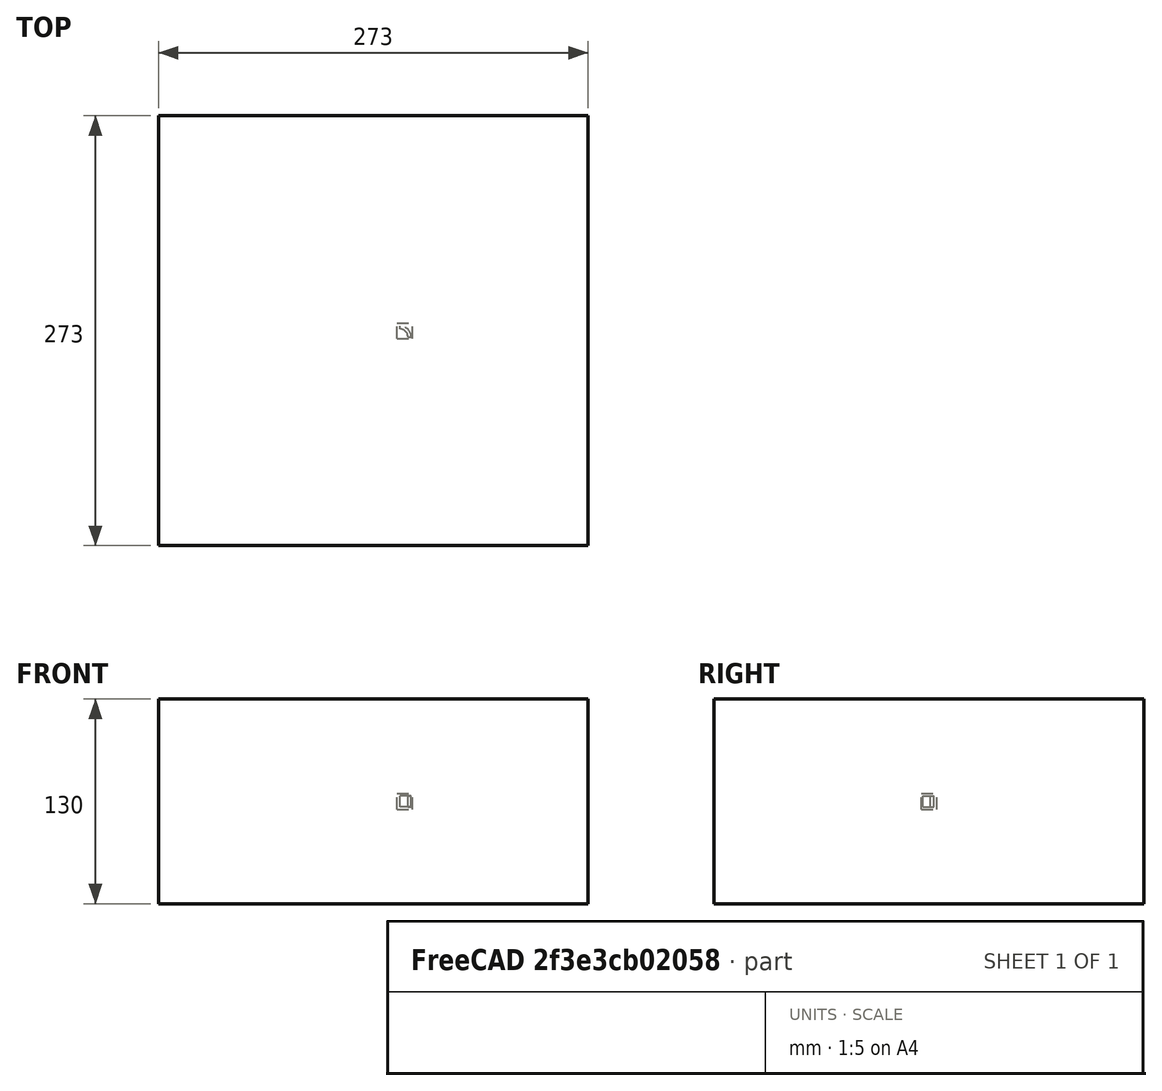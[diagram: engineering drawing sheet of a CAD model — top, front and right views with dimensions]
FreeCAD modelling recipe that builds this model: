
FCSTD DOCUMENT  (FreeCAD 1.0R39109 (Git))
Label: polarArray-of-Part
License: All rights reserved
LicenseURL: http://en.wikipedia.org/wiki/All_rights_reserved
objects: App::DocumentObjectGroupPython×1251, Part::FeaturePython×4, App::Part×4
note: 3 computed .brp shape members not serialized (recipe doc carries the construction recipe); baked Part::Feature solids carry a one-line shape summary decoded from their .brp

FEATURE [App::DocumentObjectGroupPython] HALFPI  # scripted group (container) (typed FeaturePython)
  name = HALFPI
  value = pi/2.
FEATURE [App::DocumentObjectGroupPython] PI  # scripted group (container) (typed FeaturePython)
  name = PI
  value = 1.*pi
FEATURE [App::DocumentObjectGroupPython] TWOPI  # scripted group (container) (typed FeaturePython)
  name = TWOPI
  value = 2.*pi
FEATURE [App::DocumentObjectGroupPython] Constants  # scripted group (container) (typed FeaturePython)
  Group = -> [HALFPI,PI,TWOPI]
FEATURE [App::DocumentObjectGroupPython] Variables  # scripted group (container) (typed FeaturePython)
FEATURE [App::DocumentObjectGroupPython] Quantities  # scripted group (container) (typed FeaturePython)
FEATURE [App::DocumentObjectGroupPython] Isotopes  # scripted group (container) (typed FeaturePython)
FEATURE [App::DocumentObjectGroupPython] Elements  # scripted group (container) (typed FeaturePython)
FEATURE [App::DocumentObjectGroupPython] Matrix  # scripted group (container) (typed FeaturePython)
FEATURE [App::DocumentObjectGroupPython] Surfaces  # scripted group (container) (typed FeaturePython)
FEATURE [App::DocumentObjectGroupPython] Opticals  # scripted group (container) (typed FeaturePython)
  Group = -> [Matrix,Surfaces]
FEATURE [App::DocumentObjectGroupPython] G4Isotopes  # scripted group (container) (typed FeaturePython)
FEATURE [App::DocumentObjectGroupPython] H_element  # scripted group (container) (typed FeaturePython)
  Z = 1
  atom_value = 1.008
  formula = H
  name = H_element
FEATURE [App::DocumentObjectGroupPython] He_element  # scripted group (container) (typed FeaturePython)
  Z = 2
  atom_value = 4.0026
  formula = He
  name = He_element
FEATURE [App::DocumentObjectGroupPython] Li_element  # scripted group (container) (typed FeaturePython)
  Z = 3
  atom_value = 6.94
  formula = Li
  name = Li_element
FEATURE [App::DocumentObjectGroupPython] Be_element  # scripted group (container) (typed FeaturePython)
  Z = 4
  atom_value = 9.01218
  formula = Be
  name = Be_element
FEATURE [App::DocumentObjectGroupPython] B_element  # scripted group (container) (typed FeaturePython)
  Z = 5
  atom_value = 10.81
  formula = B
  name = B_element
FEATURE [App::DocumentObjectGroupPython] C_element  # scripted group (container) (typed FeaturePython)
  Z = 6
  atom_value = 12.011
  formula = C
  name = C_element
FEATURE [App::DocumentObjectGroupPython] N_element  # scripted group (container) (typed FeaturePython)
  Z = 7
  atom_value = 14.007
  formula = N
  name = N_element
FEATURE [App::DocumentObjectGroupPython] O_element  # scripted group (container) (typed FeaturePython)
  Z = 8
  atom_value = 15.999
  formula = O
  name = O_element
FEATURE [App::DocumentObjectGroupPython] F_element  # scripted group (container) (typed FeaturePython)
  Z = 9
  atom_value = 18.9984
  formula = F
  name = F_element
FEATURE [App::DocumentObjectGroupPython] Ne_element  # scripted group (container) (typed FeaturePython)
  Z = 10
  atom_value = 20.1797
  formula = Ne
  name = Ne_element
FEATURE [App::DocumentObjectGroupPython] Na_element  # scripted group (container) (typed FeaturePython)
  Z = 11
  atom_value = 22.9898
  formula = Na
  name = Na_element
FEATURE [App::DocumentObjectGroupPython] Mg_element  # scripted group (container) (typed FeaturePython)
  Z = 12
  atom_value = 24.305
  formula = Mg
  name = Mg_element
FEATURE [App::DocumentObjectGroupPython] Al_element  # scripted group (container) (typed FeaturePython)
  Z = 13
  atom_value = 26.9815
  formula = Al
  name = Al_element
FEATURE [App::DocumentObjectGroupPython] Si_element  # scripted group (container) (typed FeaturePython)
  Z = 14
  atom_value = 28.085
  formula = Si
  name = Si_element
FEATURE [App::DocumentObjectGroupPython] P_element  # scripted group (container) (typed FeaturePython)
  Z = 15
  atom_value = 30.9738
  formula = P
  name = P_element
FEATURE [App::DocumentObjectGroupPython] S_element  # scripted group (container) (typed FeaturePython)
  Z = 16
  atom_value = 32.06
  formula = S
  name = S_element
FEATURE [App::DocumentObjectGroupPython] Cl_element  # scripted group (container) (typed FeaturePython)
  Z = 17
  atom_value = 35.45
  formula = Cl
  name = Cl_element
FEATURE [App::DocumentObjectGroupPython] Ar_element  # scripted group (container) (typed FeaturePython)
  Z = 18
  atom_value = 39.95
  formula = Ar
  name = Ar_element
FEATURE [App::DocumentObjectGroupPython] K_element  # scripted group (container) (typed FeaturePython)
  Z = 19
  atom_value = 39.0983
  formula = K
  name = K_element
FEATURE [App::DocumentObjectGroupPython] Ca_element  # scripted group (container) (typed FeaturePython)
  Z = 20
  atom_value = 40.078
  formula = Ca
  name = Ca_element
FEATURE [App::DocumentObjectGroupPython] Sc_element  # scripted group (container) (typed FeaturePython)
  Z = 21
  atom_value = 44.9559
  formula = Sc
  name = Sc_element
FEATURE [App::DocumentObjectGroupPython] Ti_element  # scripted group (container) (typed FeaturePython)
  Z = 22
  atom_value = 47.867
  formula = Ti
  name = Ti_element
FEATURE [App::DocumentObjectGroupPython] V_element  # scripted group (container) (typed FeaturePython)
  Z = 23
  atom_value = 50.9415
  formula = V
  name = V_element
FEATURE [App::DocumentObjectGroupPython] Cr_element  # scripted group (container) (typed FeaturePython)
  Z = 24
  atom_value = 51.9961
  formula = Cr
  name = Cr_element
FEATURE [App::DocumentObjectGroupPython] Mn_element  # scripted group (container) (typed FeaturePython)
  Z = 25
  atom_value = 54.938
  formula = Mn
  name = Mn_element
FEATURE [App::DocumentObjectGroupPython] Fe_element  # scripted group (container) (typed FeaturePython)
  Z = 26
  atom_value = 55.845
  formula = Fe
  name = Fe_element
FEATURE [App::DocumentObjectGroupPython] Co_element  # scripted group (container) (typed FeaturePython)
  Z = 27
  atom_value = 58.9332
  formula = Co
  name = Co_element
FEATURE [App::DocumentObjectGroupPython] Ni_element  # scripted group (container) (typed FeaturePython)
  Z = 28
  atom_value = 58.6934
  formula = Ni
  name = Ni_element
FEATURE [App::DocumentObjectGroupPython] Cu_element  # scripted group (container) (typed FeaturePython)
  Z = 29
  atom_value = 63.546
  formula = Cu
  name = Cu_element
FEATURE [App::DocumentObjectGroupPython] Zn_element  # scripted group (container) (typed FeaturePython)
  Z = 30
  atom_value = 65.38
  formula = Zn
  name = Zn_element
FEATURE [App::DocumentObjectGroupPython] Ga_element  # scripted group (container) (typed FeaturePython)
  Z = 31
  atom_value = 69.723
  formula = Ga
  name = Ga_element
FEATURE [App::DocumentObjectGroupPython] Ge_element  # scripted group (container) (typed FeaturePython)
  Z = 32
  atom_value = 72.63
  formula = Ge
  name = Ge_element
FEATURE [App::DocumentObjectGroupPython] As_element  # scripted group (container) (typed FeaturePython)
  Z = 33
  atom_value = 74.9216
  formula = As
  name = As_element
FEATURE [App::DocumentObjectGroupPython] Se_element  # scripted group (container) (typed FeaturePython)
  Z = 34
  atom_value = 78.971
  formula = Se
  name = Se_element
FEATURE [App::DocumentObjectGroupPython] Br_element  # scripted group (container) (typed FeaturePython)
  Z = 35
  atom_value = 79.904
  formula = Br
  name = Br_element
FEATURE [App::DocumentObjectGroupPython] Kr_element  # scripted group (container) (typed FeaturePython)
  Z = 36
  atom_value = 83.798
  formula = Kr
  name = Kr_element
FEATURE [App::DocumentObjectGroupPython] Rb_element  # scripted group (container) (typed FeaturePython)
  Z = 37
  atom_value = 85.4678
  formula = Rb
  name = Rb_element
FEATURE [App::DocumentObjectGroupPython] Sr_element  # scripted group (container) (typed FeaturePython)
  Z = 38
  atom_value = 87.62
  formula = Sr
  name = Sr_element
FEATURE [App::DocumentObjectGroupPython] Y_element  # scripted group (container) (typed FeaturePython)
  Z = 39
  atom_value = 88.9058
  formula = Y
  name = Y_element
FEATURE [App::DocumentObjectGroupPython] Zr_element  # scripted group (container) (typed FeaturePython)
  Z = 40
  atom_value = 91.224
  formula = Zr
  name = Zr_element
FEATURE [App::DocumentObjectGroupPython] Nb_element  # scripted group (container) (typed FeaturePython)
  Z = 41
  atom_value = 92.9064
  formula = Nb
  name = Nb_element
FEATURE [App::DocumentObjectGroupPython] Mo_element  # scripted group (container) (typed FeaturePython)
  Z = 42
  atom_value = 95.95
  formula = Mo
  name = Mo_element
FEATURE [App::DocumentObjectGroupPython] Tc_element  # scripted group (container) (typed FeaturePython)
  Z = 43
  atom_value = 97
  formula = Tc
  name = Tc_element
FEATURE [App::DocumentObjectGroupPython] Ru_element  # scripted group (container) (typed FeaturePython)
  Z = 44
  atom_value = 101.07
  formula = Ru
  name = Ru_element
FEATURE [App::DocumentObjectGroupPython] Rh_element  # scripted group (container) (typed FeaturePython)
  Z = 45
  atom_value = 102.905
  formula = Rh
  name = Rh_element
FEATURE [App::DocumentObjectGroupPython] Pd_element  # scripted group (container) (typed FeaturePython)
  Z = 46
  atom_value = 106.42
  formula = Pd
  name = Pd_element
FEATURE [App::DocumentObjectGroupPython] Ag_element  # scripted group (container) (typed FeaturePython)
  Z = 47
  atom_value = 107.868
  formula = Ag
  name = Ag_element
FEATURE [App::DocumentObjectGroupPython] Cd_element  # scripted group (container) (typed FeaturePython)
  Z = 48
  atom_value = 112.414
  formula = Cd
  name = Cd_element
FEATURE [App::DocumentObjectGroupPython] In_element  # scripted group (container) (typed FeaturePython)
  Z = 49
  atom_value = 114.818
  formula = In
  name = In_element
FEATURE [App::DocumentObjectGroupPython] Sn_element  # scripted group (container) (typed FeaturePython)
  Z = 50
  atom_value = 118.71
  formula = Sn
  name = Sn_element
FEATURE [App::DocumentObjectGroupPython] Sb_element  # scripted group (container) (typed FeaturePython)
  Z = 51
  atom_value = 121.76
  formula = Sb
  name = Sb_element
FEATURE [App::DocumentObjectGroupPython] Te_element  # scripted group (container) (typed FeaturePython)
  Z = 52
  atom_value = 127.6
  formula = Te
  name = Te_element
FEATURE [App::DocumentObjectGroupPython] I_element  # scripted group (container) (typed FeaturePython)
  Z = 53
  atom_value = 126.904
  formula = I
  name = I_element
FEATURE [App::DocumentObjectGroupPython] Xe_element  # scripted group (container) (typed FeaturePython)
  Z = 54
  atom_value = 131.293
  formula = Xe
  name = Xe_element
FEATURE [App::DocumentObjectGroupPython] Cs_element  # scripted group (container) (typed FeaturePython)
  Z = 55
  atom_value = 132.905
  formula = Cs
  name = Cs_element
FEATURE [App::DocumentObjectGroupPython] Ba_element  # scripted group (container) (typed FeaturePython)
  Z = 56
  atom_value = 137.327
  formula = Ba
  name = Ba_element
FEATURE [App::DocumentObjectGroupPython] La_element  # scripted group (container) (typed FeaturePython)
  Z = 57
  atom_value = 138.905
  formula = La
  name = La_element
FEATURE [App::DocumentObjectGroupPython] Ce_element  # scripted group (container) (typed FeaturePython)
  Z = 58
  atom_value = 140.116
  formula = Ce
  name = Ce_element
FEATURE [App::DocumentObjectGroupPython] Pr_element  # scripted group (container) (typed FeaturePython)
  Z = 59
  atom_value = 140.908
  formula = Pr
  name = Pr_element
FEATURE [App::DocumentObjectGroupPython] Nd_element  # scripted group (container) (typed FeaturePython)
  Z = 60
  atom_value = 144.242
  formula = Nd
  name = Nd_element
FEATURE [App::DocumentObjectGroupPython] Pm_element  # scripted group (container) (typed FeaturePython)
  Z = 61
  atom_value = 145
  formula = Pm
  name = Pm_element
FEATURE [App::DocumentObjectGroupPython] Sm_element  # scripted group (container) (typed FeaturePython)
  Z = 62
  atom_value = 150.36
  formula = Sm
  name = Sm_element
FEATURE [App::DocumentObjectGroupPython] Eu_element  # scripted group (container) (typed FeaturePython)
  Z = 63
  atom_value = 151.964
  formula = Eu
  name = Eu_element
FEATURE [App::DocumentObjectGroupPython] Gd_element  # scripted group (container) (typed FeaturePython)
  Z = 64
  atom_value = 157.25
  formula = Gd
  name = Gd_element
FEATURE [App::DocumentObjectGroupPython] Tb_element  # scripted group (container) (typed FeaturePython)
  Z = 65
  atom_value = 158.925
  formula = Tb
  name = Tb_element
FEATURE [App::DocumentObjectGroupPython] Dy_element  # scripted group (container) (typed FeaturePython)
  Z = 66
  atom_value = 162.5
  formula = Dy
  name = Dy_element
FEATURE [App::DocumentObjectGroupPython] Ho_element  # scripted group (container) (typed FeaturePython)
  Z = 67
  atom_value = 164.93
  formula = Ho
  name = Ho_element
FEATURE [App::DocumentObjectGroupPython] Er_element  # scripted group (container) (typed FeaturePython)
  Z = 68
  atom_value = 167.259
  formula = Er
  name = Er_element
FEATURE [App::DocumentObjectGroupPython] Tm_element  # scripted group (container) (typed FeaturePython)
  Z = 69
  atom_value = 168.934
  formula = Tm
  name = Tm_element
FEATURE [App::DocumentObjectGroupPython] Yb_element  # scripted group (container) (typed FeaturePython)
  Z = 70
  atom_value = 173.045
  formula = Yb
  name = Yb_element
FEATURE [App::DocumentObjectGroupPython] Lu_element  # scripted group (container) (typed FeaturePython)
  Z = 71
  atom_value = 174.967
  formula = Lu
  name = Lu_element
FEATURE [App::DocumentObjectGroupPython] Hf_element  # scripted group (container) (typed FeaturePython)
  Z = 72
  atom_value = 178.49
  formula = Hf
  name = Hf_element
FEATURE [App::DocumentObjectGroupPython] Ta_element  # scripted group (container) (typed FeaturePython)
  Z = 73
  atom_value = 180.948
  formula = Ta
  name = Ta_element
FEATURE [App::DocumentObjectGroupPython] W_element  # scripted group (container) (typed FeaturePython)
  Z = 74
  atom_value = 183.84
  formula = W
  name = W_element
FEATURE [App::DocumentObjectGroupPython] Re_element  # scripted group (container) (typed FeaturePython)
  Z = 75
  atom_value = 186.207
  formula = Re
  name = Re_element
FEATURE [App::DocumentObjectGroupPython] Os_element  # scripted group (container) (typed FeaturePython)
  Z = 76
  atom_value = 190.23
  formula = Os
  name = Os_element
FEATURE [App::DocumentObjectGroupPython] Ir_element  # scripted group (container) (typed FeaturePython)
  Z = 77
  atom_value = 192.217
  formula = Ir
  name = Ir_element
FEATURE [App::DocumentObjectGroupPython] Pt_element  # scripted group (container) (typed FeaturePython)
  Z = 78
  atom_value = 195.084
  formula = Pt
  name = Pt_element
FEATURE [App::DocumentObjectGroupPython] Au_element  # scripted group (container) (typed FeaturePython)
  Z = 79
  atom_value = 196.967
  formula = Au
  name = Au_element
FEATURE [App::DocumentObjectGroupPython] Hg_element  # scripted group (container) (typed FeaturePython)
  Z = 80
  atom_value = 200.592
  formula = Hg
  name = Hg_element
FEATURE [App::DocumentObjectGroupPython] Tl_element  # scripted group (container) (typed FeaturePython)
  Z = 81
  atom_value = 204.38
  formula = Tl
  name = Tl_element
FEATURE [App::DocumentObjectGroupPython] Pb_element  # scripted group (container) (typed FeaturePython)
  Z = 82
  atom_value = 207.2
  formula = Pb
  name = Pb_element
FEATURE [App::DocumentObjectGroupPython] Bi_element  # scripted group (container) (typed FeaturePython)
  Z = 83
  atom_value = 208.98
  formula = Bi
  name = Bi_element
FEATURE [App::DocumentObjectGroupPython] Po_element  # scripted group (container) (typed FeaturePython)
  Z = 84
  atom_value = 209
  formula = Po
  name = Po_element
FEATURE [App::DocumentObjectGroupPython] At_element  # scripted group (container) (typed FeaturePython)
  Z = 85
  atom_value = 210
  formula = At
  name = At_element
FEATURE [App::DocumentObjectGroupPython] Rn_element  # scripted group (container) (typed FeaturePython)
  Z = 86
  atom_value = 222
  formula = Rn
  name = Rn_element
FEATURE [App::DocumentObjectGroupPython] Fr_element  # scripted group (container) (typed FeaturePython)
  Z = 87
  atom_value = 223
  formula = Fr
  name = Fr_element
FEATURE [App::DocumentObjectGroupPython] Ra_element  # scripted group (container) (typed FeaturePython)
  Z = 88
  atom_value = 226
  formula = Ra
  name = Ra_element
FEATURE [App::DocumentObjectGroupPython] Ac_element  # scripted group (container) (typed FeaturePython)
  Z = 89
  atom_value = 227
  formula = Ac
  name = Ac_element
FEATURE [App::DocumentObjectGroupPython] Th_element  # scripted group (container) (typed FeaturePython)
  Z = 90
  atom_value = 232.038
  formula = Th
  name = Th_element
FEATURE [App::DocumentObjectGroupPython] Pa_element  # scripted group (container) (typed FeaturePython)
  Z = 91
  atom_value = 231.036
  formula = Pa
  name = Pa_element
FEATURE [App::DocumentObjectGroupPython] U_element  # scripted group (container) (typed FeaturePython)
  Z = 92
  atom_value = 238.029
  formula = U
  name = U_element
FEATURE [App::DocumentObjectGroupPython] Np_element  # scripted group (container) (typed FeaturePython)
  Z = 93
  atom_value = 237
  formula = Np
  name = Np_element
FEATURE [App::DocumentObjectGroupPython] Pu_element  # scripted group (container) (typed FeaturePython)
  Z = 94
  atom_value = 244
  formula = Pu
  name = Pu_element
FEATURE [App::DocumentObjectGroupPython] Am_element  # scripted group (container) (typed FeaturePython)
  Z = 95
  atom_value = 243
  formula = Am
  name = Am_element
FEATURE [App::DocumentObjectGroupPython] Cm_element  # scripted group (container) (typed FeaturePython)
  Z = 96
  atom_value = 247
  formula = Cm
  name = Cm_element
FEATURE [App::DocumentObjectGroupPython] Bk_element  # scripted group (container) (typed FeaturePython)
  Z = 97
  atom_value = 247
  formula = Bk
  name = Bk_element
FEATURE [App::DocumentObjectGroupPython] Cf_element  # scripted group (container) (typed FeaturePython)
  Z = 98
  atom_value = 251
  formula = Cf
  name = Cf_element
FEATURE [App::DocumentObjectGroupPython] G4Elements  # scripted group (container) (typed FeaturePython)
  Group = -> [H_element,He_element,Li_element,Be_element,B_element,C_element,N_element,O_element,F_element,Ne_element,Na_element,Mg_element,Al_element,Si_element,P_element,S_element,Cl_element,Ar_element,K_element,Ca_element,Sc_element,Ti_element,V_element,Cr_element,Mn_element,Fe_element,Co_element,Ni_element,Cu_element,Zn_element,Ga_element,Ge_element,As_element,Se_element,Br_element,Kr_element,Rb_element,+61 more]
FEATURE [App::DocumentObjectGroupPython] H_element001  label="H_element : 0.101"  # scripted group (container) (typed FeaturePython)
  n = 0.101327
FEATURE [App::DocumentObjectGroupPython] C_element001  label="C_element : 0.775"  # scripted group (container) (typed FeaturePython)
  n = 0.7755
FEATURE [App::DocumentObjectGroupPython] N_element001  label="N_element : 0.035"  # scripted group (container) (typed FeaturePython)
  n = 0.035057
FEATURE [App::DocumentObjectGroupPython] O_element001  label="O_element : 0.052"  # scripted group (container) (typed FeaturePython)
  n = 0.0523159
FEATURE [App::DocumentObjectGroupPython] F_element001  label="F_element : 0.017"  # scripted group (container) (typed FeaturePython)
  n = 0.017422
FEATURE [App::DocumentObjectGroupPython] Ca_element001  label="Ca_element : 0.018"  # scripted group (container) (typed FeaturePython)
  n = 0.018378
FEATURE [App::DocumentObjectGroupPython] G4_A_150_TISSUE  label="G4_A-150_TISSUE"  # scripted group (container) (typed FeaturePython)
  Dunit = g/cm3
  Dvalue = 1.127
  Group = -> [H_element001,C_element001,N_element001,O_element001,F_element001,Ca_element001]
  conduct = 2
  density = 1
  expand = 3
  formula = G4_A-150_TISSUE
  name = G4_A-150_TISSUE
  specific = 4
FEATURE [App::DocumentObjectGroupPython] C_element002  label="C_element : 3"  # scripted group (container) (typed FeaturePython)
  n = 3
  ref = C_element
FEATURE [App::DocumentObjectGroupPython] H_element002  label="H_element : 6"  # scripted group (container) (typed FeaturePython)
  n = 6
  ref = H_element
FEATURE [App::DocumentObjectGroupPython] O_element002  label="O_element : 1"  # scripted group (container) (typed FeaturePython)
  n = 1
  ref = O_element
FEATURE [App::DocumentObjectGroupPython] G4_ACETONE  # scripted group (container) (typed FeaturePython)
  Dunit = g/cm3
  Dvalue = 0.7899
  Group = -> [C_element002,H_element002,O_element002]
  conduct = 2
  density = 1
  expand = 3
  formula = G4_ACETONE
  name = G4_ACETONE
  specific = 4
FEATURE [App::DocumentObjectGroupPython] C_element003  label="C_element : 2"  # scripted group (container) (typed FeaturePython)
  n = 2
  ref = C_element
FEATURE [App::DocumentObjectGroupPython] H_element003  label="H_element : 2"  # scripted group (container) (typed FeaturePython)
  n = 2
  ref = H_element
FEATURE [App::DocumentObjectGroupPython] G4_ACETYLENE  # scripted group (container) (typed FeaturePython)
  Dunit = g/cm3
  Dvalue = 0.0010967
  Group = -> [C_element003,H_element003]
  conduct = 2
  density = 1
  expand = 3
  formula = G4_ACETYLENE
  name = G4_ACETYLENE
  specific = 4
FEATURE [App::DocumentObjectGroupPython] C_element004  label="C_element : 5"  # scripted group (container) (typed FeaturePython)
  n = 5
  ref = C_element
FEATURE [App::DocumentObjectGroupPython] H_element004  label="H_element : 5"  # scripted group (container) (typed FeaturePython)
  n = 5
  ref = H_element
FEATURE [App::DocumentObjectGroupPython] N_element002  label="N_element : 5"  # scripted group (container) (typed FeaturePython)
  n = 5
  ref = N_element
FEATURE [App::DocumentObjectGroupPython] G4_ADENINE  # scripted group (container) (typed FeaturePython)
  Dunit = g/cm3
  Dvalue = 1.6
  Group = -> [C_element004,H_element004,N_element002]
  conduct = 2
  density = 1
  expand = 3
  formula = G4_ADENINE
  name = G4_ADENINE
  specific = 4
FEATURE [App::DocumentObjectGroupPython] H_element005  label="H_element : 0.114"  # scripted group (container) (typed FeaturePython)
  n = 0.114
FEATURE [App::DocumentObjectGroupPython] C_element005  label="C_element : 0.598"  # scripted group (container) (typed FeaturePython)
  n = 0.598
FEATURE [App::DocumentObjectGroupPython] N_element003  label="N_element : 0.007"  # scripted group (container) (typed FeaturePython)
  n = 0.007
FEATURE [App::DocumentObjectGroupPython] O_element003  label="O_element : 0.278"  # scripted group (container) (typed FeaturePython)
  n = 0.278
FEATURE [App::DocumentObjectGroupPython] Na_element001  label="Na_element : 0.001"  # scripted group (container) (typed FeaturePython)
  n = 0.001
FEATURE [App::DocumentObjectGroupPython] S_element001  label="S_element : 0.001"  # scripted group (container) (typed FeaturePython)
  n = 0.001
FEATURE [App::DocumentObjectGroupPython] Cl_element001  label="Cl_element : 0.001"  # scripted group (container) (typed FeaturePython)
  n = 0.001
FEATURE [App::DocumentObjectGroupPython] G4_ADIPOSE_TISSUE_ICRP  # scripted group (container) (typed FeaturePython)
  Dunit = g/cm3
  Dvalue = 0.95
  Group = -> [H_element005,C_element005,N_element003,O_element003,Na_element001,S_element001,Cl_element001]
  conduct = 2
  density = 1
  expand = 3
  formula = G4_ADIPOSE_TISSUE_ICRP
  name = G4_ADIPOSE_TISSUE_ICRP
  specific = 4
FEATURE [App::DocumentObjectGroupPython] C_element006  label="C_element : 0.000"  # scripted group (container) (typed FeaturePython)
  n = 0.000124
FEATURE [App::DocumentObjectGroupPython] N_element004  label="N_element : 0.755"  # scripted group (container) (typed FeaturePython)
  n = 0.755268
FEATURE [App::DocumentObjectGroupPython] O_element004  label="O_element : 0.232"  # scripted group (container) (typed FeaturePython)
  n = 0.231781
FEATURE [App::DocumentObjectGroupPython] Ar_element001  label="Ar_element : 0.013"  # scripted group (container) (typed FeaturePython)
  n = 0.012827
FEATURE [App::DocumentObjectGroupPython] G4_AIR  # scripted group (container) (typed FeaturePython)
  Dunit = g/cm3
  Dvalue = 0.00120479
  Group = -> [C_element006,N_element004,O_element004,Ar_element001]
  conduct = 2
  density = 1
  expand = 3
  formula = G4_AIR
  name = G4_AIR
  specific = 4
FEATURE [App::DocumentObjectGroupPython] C_element007  label="C_element : 006"  # scripted group (container) (typed FeaturePython)
  n = 3
  ref = C_element
FEATURE [App::DocumentObjectGroupPython] H_element006  label="H_element : 7"  # scripted group (container) (typed FeaturePython)
  n = 7
  ref = H_element
FEATURE [App::DocumentObjectGroupPython] N_element005  label="N_element : 1"  # scripted group (container) (typed FeaturePython)
  n = 1
  ref = N_element
FEATURE [App::DocumentObjectGroupPython] O_element005  label="O_element : 2"  # scripted group (container) (typed FeaturePython)
  n = 2
  ref = O_element
FEATURE [App::DocumentObjectGroupPython] G4_ALANINE  # scripted group (container) (typed FeaturePython)
  Dunit = g/cm3
  Dvalue = 1.42
  Group = -> [C_element007,H_element006,N_element005,O_element005]
  conduct = 2
  density = 1
  expand = 3
  formula = G4_ALANINE
  name = G4_ALANINE
  specific = 4
FEATURE [App::DocumentObjectGroupPython] Al_element001  label="Al_element : 2"  # scripted group (container) (typed FeaturePython)
  n = 2
  ref = Al_element
FEATURE [App::DocumentObjectGroupPython] O_element006  label="O_element : 3"  # scripted group (container) (typed FeaturePython)
  n = 3
  ref = O_element
FEATURE [App::DocumentObjectGroupPython] G4_ALUMINUM_OXIDE  # scripted group (container) (typed FeaturePython)
  Dunit = g/cm3
  Dvalue = 3.97
  Group = -> [Al_element001,O_element006]
  conduct = 2
  density = 1
  expand = 3
  formula = G4_ALUMINUM_OXIDE
  name = G4_ALUMINUM_OXIDE
  specific = 4
FEATURE [App::DocumentObjectGroupPython] H_element007  label="H_element : 0.106"  # scripted group (container) (typed FeaturePython)
  n = 0.10593
FEATURE [App::DocumentObjectGroupPython] C_element008  label="C_element : 0.789"  # scripted group (container) (typed FeaturePython)
  n = 0.788974
FEATURE [App::DocumentObjectGroupPython] O_element007  label="O_element : 0.105"  # scripted group (container) (typed FeaturePython)
  n = 0.105096
FEATURE [App::DocumentObjectGroupPython] G4_AMBER  # scripted group (container) (typed FeaturePython)
  Dunit = g/cm3
  Dvalue = 1.1
  Group = -> [H_element007,C_element008,O_element007]
  conduct = 2
  density = 1
  expand = 3
  formula = G4_AMBER
  name = G4_AMBER
  specific = 4
FEATURE [App::DocumentObjectGroupPython] N_element006  label="N_element : 006"  # scripted group (container) (typed FeaturePython)
  n = 1
  ref = N_element
FEATURE [App::DocumentObjectGroupPython] H_element008  label="H_element : 3"  # scripted group (container) (typed FeaturePython)
  n = 3
  ref = H_element
FEATURE [App::DocumentObjectGroupPython] G4_AMMONIA  # scripted group (container) (typed FeaturePython)
  Dunit = g/cm3
  Dvalue = 0.000826019
  Group = -> [N_element006,H_element008]
  conduct = 2
  density = 1
  expand = 3
  formula = G4_AMMONIA
  name = G4_AMMONIA
  specific = 4
FEATURE [App::DocumentObjectGroupPython] C_element009  label="C_element : 6"  # scripted group (container) (typed FeaturePython)
  n = 6
  ref = C_element
FEATURE [App::DocumentObjectGroupPython] H_element009  label="H_element : 008"  # scripted group (container) (typed FeaturePython)
  n = 7
  ref = H_element
FEATURE [App::DocumentObjectGroupPython] N_element007  label="N_element : 007"  # scripted group (container) (typed FeaturePython)
  n = 1
  ref = N_element
FEATURE [App::DocumentObjectGroupPython] G4_ANILINE  # scripted group (container) (typed FeaturePython)
  Dunit = g/cm3
  Dvalue = 1.0235
  Group = -> [C_element009,H_element009,N_element007]
  conduct = 2
  density = 1
  expand = 3
  formula = G4_ANILINE
  name = G4_ANILINE
  specific = 4
FEATURE [App::DocumentObjectGroupPython] C_element010  label="C_element : 14"  # scripted group (container) (typed FeaturePython)
  n = 14
  ref = C_element
FEATURE [App::DocumentObjectGroupPython] H_element010  label="H_element : 10"  # scripted group (container) (typed FeaturePython)
  n = 10
  ref = H_element
FEATURE [App::DocumentObjectGroupPython] G4_ANTHRACENE  # scripted group (container) (typed FeaturePython)
  Dunit = g/cm3
  Dvalue = 1.283
  Group = -> [C_element010,H_element010]
  conduct = 2
  density = 1
  expand = 3
  formula = G4_ANTHRACENE
  name = G4_ANTHRACENE
  specific = 4
FEATURE [App::DocumentObjectGroupPython] H_element011  label="H_element : 0.065"  # scripted group (container) (typed FeaturePython)
  n = 0.0654709
FEATURE [App::DocumentObjectGroupPython] C_element011  label="C_element : 0.537"  # scripted group (container) (typed FeaturePython)
  n = 0.536944
FEATURE [App::DocumentObjectGroupPython] N_element008  label="N_element : 0.021"  # scripted group (container) (typed FeaturePython)
  n = 0.0215
FEATURE [App::DocumentObjectGroupPython] O_element008  label="O_element : 0.032"  # scripted group (container) (typed FeaturePython)
  n = 0.032085
FEATURE [App::DocumentObjectGroupPython] F_element002  label="F_element : 0.167"  # scripted group (container) (typed FeaturePython)
  n = 0.167411
FEATURE [App::DocumentObjectGroupPython] Ca_element002  label="Ca_element : 0.177"  # scripted group (container) (typed FeaturePython)
  n = 0.176589
FEATURE [App::DocumentObjectGroupPython] G4_B_100_BONE  label="G4_B-100_BONE"  # scripted group (container) (typed FeaturePython)
  Dunit = g/cm3
  Dvalue = 1.45
  Group = -> [H_element011,C_element011,N_element008,O_element008,F_element002,Ca_element002]
  conduct = 2
  density = 1
  expand = 3
  formula = G4_B-100_BONE
  name = G4_B-100_BONE
  specific = 4
FEATURE [App::DocumentObjectGroupPython] H_element012  label="H_element : 0.057"  # scripted group (container) (typed FeaturePython)
  n = 0.057441
FEATURE [App::DocumentObjectGroupPython] C_element012  label="C_element : 0.790"  # scripted group (container) (typed FeaturePython)
  n = 0.774591
FEATURE [App::DocumentObjectGroupPython] O_element009  label="O_element : 0.168"  # scripted group (container) (typed FeaturePython)
  n = 0.167968
FEATURE [App::DocumentObjectGroupPython] G4_BAKELITE  # scripted group (container) (typed FeaturePython)
  Dunit = g/cm3
  Dvalue = 1.25
  Group = -> [H_element012,C_element012,O_element009]
  conduct = 2
  density = 1
  expand = 3
  formula = G4_BAKELITE
  name = G4_BAKELITE
  specific = 4
FEATURE [App::DocumentObjectGroupPython] Ba_element001  label="Ba_element : 1"  # scripted group (container) (typed FeaturePython)
  n = 1
  ref = Ba_element
FEATURE [App::DocumentObjectGroupPython] F_element003  label="F_element : 2"  # scripted group (container) (typed FeaturePython)
  n = 2
  ref = F_element
FEATURE [App::DocumentObjectGroupPython] G4_BARIUM_FLUORIDE  # scripted group (container) (typed FeaturePython)
  Dunit = g/cm3
  Dvalue = 4.89
  Group = -> [Ba_element001,F_element003]
  conduct = 2
  density = 1
  expand = 3
  formula = G4_BARIUM_FLUORIDE
  name = G4_BARIUM_FLUORIDE
  specific = 4
FEATURE [App::DocumentObjectGroupPython] Ba_element002  label="Ba_element : 002"  # scripted group (container) (typed FeaturePython)
  n = 1
  ref = Ba_element
FEATURE [App::DocumentObjectGroupPython] S_element002  label="S_element : 1"  # scripted group (container) (typed FeaturePython)
  n = 1
  ref = S_element
FEATURE [App::DocumentObjectGroupPython] O_element010  label="O_element : 4"  # scripted group (container) (typed FeaturePython)
  n = 4
  ref = O_element
FEATURE [App::DocumentObjectGroupPython] G4_BARIUM_SULFATE  # scripted group (container) (typed FeaturePython)
  Dunit = g/cm3
  Dvalue = 4.5
  Group = -> [Ba_element002,S_element002,O_element010]
  conduct = 2
  density = 1
  expand = 3
  formula = G4_BARIUM_SULFATE
  name = G4_BARIUM_SULFATE
  specific = 4
FEATURE [App::DocumentObjectGroupPython] C_element013  label="C_element : 007"  # scripted group (container) (typed FeaturePython)
  n = 6
  ref = C_element
FEATURE [App::DocumentObjectGroupPython] H_element013  label="H_element : 009"  # scripted group (container) (typed FeaturePython)
  n = 6
  ref = H_element
FEATURE [App::DocumentObjectGroupPython] G4_BENZENE  # scripted group (container) (typed FeaturePython)
  Dunit = g/cm3
  Dvalue = 0.87865
  Group = -> [C_element013,H_element013]
  conduct = 2
  density = 1
  expand = 3
  formula = G4_BENZENE
  name = G4_BENZENE
  specific = 4
FEATURE [App::DocumentObjectGroupPython] Be_element001  label="Be_element : 1"  # scripted group (container) (typed FeaturePython)
  n = 1
  ref = Be_element
FEATURE [App::DocumentObjectGroupPython] O_element011  label="O_element : 005"  # scripted group (container) (typed FeaturePython)
  n = 1
  ref = O_element
FEATURE [App::DocumentObjectGroupPython] G4_BERYLLIUM_OXIDE  # scripted group (container) (typed FeaturePython)
  Dunit = g/cm3
  Dvalue = 3.01
  Group = -> [Be_element001,O_element011]
  conduct = 2
  density = 1
  expand = 3
  formula = G4_BERYLLIUM_OXIDE
  name = G4_BERYLLIUM_OXIDE
  specific = 4
FEATURE [App::DocumentObjectGroupPython] Bi_element001  label="Bi_element : 4"  # scripted group (container) (typed FeaturePython)
  n = 4
  ref = Bi_element
FEATURE [App::DocumentObjectGroupPython] Ge_element001  label="Ge_element : 3"  # scripted group (container) (typed FeaturePython)
  n = 3
  ref = Ge_element
FEATURE [App::DocumentObjectGroupPython] O_element012  label="O_element : 12"  # scripted group (container) (typed FeaturePython)
  n = 12
  ref = O_element
FEATURE [App::DocumentObjectGroupPython] G4_BGO  # scripted group (container) (typed FeaturePython)
  Dunit = g/cm3
  Dvalue = 7.13
  Group = -> [Bi_element001,Ge_element001,O_element012]
  conduct = 2
  density = 1
  expand = 3
  formula = G4_BGO
  name = G4_BGO
  specific = 4
FEATURE [App::DocumentObjectGroupPython] H_element014  label="H_element : 0.102"  # scripted group (container) (typed FeaturePython)
  n = 0.102
FEATURE [App::DocumentObjectGroupPython] C_element014  label="C_element : 0.110"  # scripted group (container) (typed FeaturePython)
  n = 0.11
FEATURE [App::DocumentObjectGroupPython] N_element009  label="N_element : 0.033"  # scripted group (container) (typed FeaturePython)
  n = 0.033
FEATURE [App::DocumentObjectGroupPython] O_element013  label="O_element : 0.745"  # scripted group (container) (typed FeaturePython)
  n = 0.745
FEATURE [App::DocumentObjectGroupPython] Na_element002  label="Na_element : 0.002"  # scripted group (container) (typed FeaturePython)
  n = 0.001
FEATURE [App::DocumentObjectGroupPython] P_element001  label="P_element : 0.001"  # scripted group (container) (typed FeaturePython)
  n = 0.001
FEATURE [App::DocumentObjectGroupPython] S_element003  label="S_element : 0.002"  # scripted group (container) (typed FeaturePython)
  n = 0.002
FEATURE [App::DocumentObjectGroupPython] Cl_element002  label="Cl_element : 0.003"  # scripted group (container) (typed FeaturePython)
  n = 0.003
FEATURE [App::DocumentObjectGroupPython] K_element001  label="K_element : 0.002"  # scripted group (container) (typed FeaturePython)
  n = 0.002
FEATURE [App::DocumentObjectGroupPython] Fe_element001  label="Fe_element : 0.001"  # scripted group (container) (typed FeaturePython)
  n = 0.001
FEATURE [App::DocumentObjectGroupPython] G4_BLOOD_ICRP  # scripted group (container) (typed FeaturePython)
  Dunit = g/cm3
  Dvalue = 1.06
  Group = -> [H_element014,C_element014,N_element009,O_element013,Na_element002,P_element001,S_element003,Cl_element002,K_element001,Fe_element001]
  conduct = 2
  density = 1
  expand = 3
  formula = G4_BLOOD_ICRP
  name = G4_BLOOD_ICRP
  specific = 4
FEATURE [App::DocumentObjectGroupPython] H_element015  label="H_element : 0.064"  # scripted group (container) (typed FeaturePython)
  n = 0.064
FEATURE [App::DocumentObjectGroupPython] C_element015  label="C_element : 0.278"  # scripted group (container) (typed FeaturePython)
  n = 0.278
FEATURE [App::DocumentObjectGroupPython] N_element010  label="N_element : 0.027"  # scripted group (container) (typed FeaturePython)
  n = 0.027
FEATURE [App::DocumentObjectGroupPython] O_element014  label="O_element : 0.410"  # scripted group (container) (typed FeaturePython)
  n = 0.41
FEATURE [App::DocumentObjectGroupPython] Mg_element001  label="Mg_element : 0.002"  # scripted group (container) (typed FeaturePython)
  n = 0.002
FEATURE [App::DocumentObjectGroupPython] P_element002  label="P_element : 0.070"  # scripted group (container) (typed FeaturePython)
  n = 0.07
FEATURE [App::DocumentObjectGroupPython] S_element004  label="S_element : 0.003"  # scripted group (container) (typed FeaturePython)
  n = 0.002
FEATURE [App::DocumentObjectGroupPython] Ca_element003  label="Ca_element : 0.147"  # scripted group (container) (typed FeaturePython)
  n = 0.147
FEATURE [App::DocumentObjectGroupPython] G4_BONE_COMPACT_ICRU  # scripted group (container) (typed FeaturePython)
  Dunit = g/cm3
  Dvalue = 1.85
  Group = -> [H_element015,C_element015,N_element010,O_element014,Mg_element001,P_element002,S_element004,Ca_element003]
  conduct = 2
  density = 1
  expand = 3
  formula = G4_BONE_COMPACT_ICRU
  name = G4_BONE_COMPACT_ICRU
  specific = 4
FEATURE [App::DocumentObjectGroupPython] H_element016  label="H_element : 0.034"  # scripted group (container) (typed FeaturePython)
  n = 0.034
FEATURE [App::DocumentObjectGroupPython] C_element016  label="C_element : 0.155"  # scripted group (container) (typed FeaturePython)
  n = 0.155
FEATURE [App::DocumentObjectGroupPython] N_element011  label="N_element : 0.042"  # scripted group (container) (typed FeaturePython)
  n = 0.042
FEATURE [App::DocumentObjectGroupPython] O_element015  label="O_element : 0.435"  # scripted group (container) (typed FeaturePython)
  n = 0.435
FEATURE [App::DocumentObjectGroupPython] Na_element003  label="Na_element : 0.003"  # scripted group (container) (typed FeaturePython)
  n = 0.001
FEATURE [App::DocumentObjectGroupPython] Mg_element002  label="Mg_element : 0.003"  # scripted group (container) (typed FeaturePython)
  n = 0.002
FEATURE [App::DocumentObjectGroupPython] P_element003  label="P_element : 0.103"  # scripted group (container) (typed FeaturePython)
  n = 0.103
FEATURE [App::DocumentObjectGroupPython] S_element005  label="S_element : 0.004"  # scripted group (container) (typed FeaturePython)
  n = 0.003
FEATURE [App::DocumentObjectGroupPython] Ca_element004  label="Ca_element : 0.225"  # scripted group (container) (typed FeaturePython)
  n = 0.225
FEATURE [App::DocumentObjectGroupPython] G4_BONE_CORTICAL_ICRP  # scripted group (container) (typed FeaturePython)
  Dunit = g/cm3
  Dvalue = 1.92
  Group = -> [H_element016,C_element016,N_element011,O_element015,Na_element003,Mg_element002,P_element003,S_element005,Ca_element004]
  conduct = 2
  density = 1
  expand = 3
  formula = G4_BONE_CORTICAL_ICRP
  name = G4_BONE_CORTICAL_ICRP
  specific = 4
FEATURE [App::DocumentObjectGroupPython] B_element001  label="B_element : 4"  # scripted group (container) (typed FeaturePython)
  n = 4
  ref = B_element
FEATURE [App::DocumentObjectGroupPython] C_element017  label="C_element : 1"  # scripted group (container) (typed FeaturePython)
  n = 1
  ref = C_element
FEATURE [App::DocumentObjectGroupPython] G4_BORON_CARBIDE  # scripted group (container) (typed FeaturePython)
  Dunit = g/cm3
  Dvalue = 2.52
  Group = -> [B_element001,C_element017]
  conduct = 2
  density = 1
  expand = 3
  formula = G4_BORON_CARBIDE
  name = G4_BORON_CARBIDE
  specific = 4
FEATURE [App::DocumentObjectGroupPython] B_element002  label="B_element : 2"  # scripted group (container) (typed FeaturePython)
  n = 2
  ref = B_element
FEATURE [App::DocumentObjectGroupPython] O_element016  label="O_element : 006"  # scripted group (container) (typed FeaturePython)
  n = 3
  ref = O_element
FEATURE [App::DocumentObjectGroupPython] G4_BORON_OXIDE  # scripted group (container) (typed FeaturePython)
  Dunit = g/cm3
  Dvalue = 1.812
  Group = -> [B_element002,O_element016]
  conduct = 2
  density = 1
  expand = 3
  formula = G4_BORON_OXIDE
  name = G4_BORON_OXIDE
  specific = 4
FEATURE [App::DocumentObjectGroupPython] H_element017  label="H_element : 0.107"  # scripted group (container) (typed FeaturePython)
  n = 0.107
FEATURE [App::DocumentObjectGroupPython] C_element018  label="C_element : 0.145"  # scripted group (container) (typed FeaturePython)
  n = 0.145
FEATURE [App::DocumentObjectGroupPython] N_element012  label="N_element : 0.022"  # scripted group (container) (typed FeaturePython)
  n = 0.022
FEATURE [App::DocumentObjectGroupPython] O_element017  label="O_element : 0.712"  # scripted group (container) (typed FeaturePython)
  n = 0.712
FEATURE [App::DocumentObjectGroupPython] Na_element004  label="Na_element : 0.004"  # scripted group (container) (typed FeaturePython)
  n = 0.002
FEATURE [App::DocumentObjectGroupPython] P_element004  label="P_element : 0.004"  # scripted group (container) (typed FeaturePython)
  n = 0.004
FEATURE [App::DocumentObjectGroupPython] S_element006  label="S_element : 0.005"  # scripted group (container) (typed FeaturePython)
  n = 0.002
FEATURE [App::DocumentObjectGroupPython] Cl_element003  label="Cl_element : 0.004"  # scripted group (container) (typed FeaturePython)
  n = 0.003
FEATURE [App::DocumentObjectGroupPython] K_element002  label="K_element : 0.003"  # scripted group (container) (typed FeaturePython)
  n = 0.003
FEATURE [App::DocumentObjectGroupPython] G4_BRAIN_ICRP  # scripted group (container) (typed FeaturePython)
  Dunit = g/cm3
  Dvalue = 1.04
  Group = -> [H_element017,C_element018,N_element012,O_element017,Na_element004,P_element004,S_element006,Cl_element003,K_element002]
  conduct = 2
  density = 1
  expand = 3
  formula = G4_BRAIN_ICRP
  name = G4_BRAIN_ICRP
  specific = 4
FEATURE [App::DocumentObjectGroupPython] C_element019  label="C_element : 4"  # scripted group (container) (typed FeaturePython)
  n = 4
  ref = C_element
FEATURE [App::DocumentObjectGroupPython] H_element018  label="H_element : 010"  # scripted group (container) (typed FeaturePython)
  n = 10
  ref = H_element
FEATURE [App::DocumentObjectGroupPython] G4_BUTANE  # scripted group (container) (typed FeaturePython)
  Dunit = g/cm3
  Dvalue = 0.00249343
  Group = -> [C_element019,H_element018]
  conduct = 2
  density = 1
  expand = 3
  formula = G4_BUTANE
  name = G4_BUTANE
  specific = 4
FEATURE [App::DocumentObjectGroupPython] C_element020  label="C_element : 008"  # scripted group (container) (typed FeaturePython)
  n = 4
  ref = C_element
FEATURE [App::DocumentObjectGroupPython] H_element019  label="H_element : 011"  # scripted group (container) (typed FeaturePython)
  n = 10
  ref = H_element
FEATURE [App::DocumentObjectGroupPython] O_element018  label="O_element : 007"  # scripted group (container) (typed FeaturePython)
  n = 1
  ref = O_element
FEATURE [App::DocumentObjectGroupPython] G4_N_BUTYL_ALCOHOL  label="G4_N-BUTYL_ALCOHOL"  # scripted group (container) (typed FeaturePython)
  Dunit = g/cm3
  Dvalue = 0.8098
  Group = -> [C_element020,H_element019,O_element018]
  conduct = 2
  density = 1
  expand = 3
  formula = G4_N-BUTYL_ALCOHOL
  name = G4_N-BUTYL_ALCOHOL
  specific = 4
FEATURE [App::DocumentObjectGroupPython] H_element020  label="H_element : 0.025"  # scripted group (container) (typed FeaturePython)
  n = 0.02468
FEATURE [App::DocumentObjectGroupPython] C_element021  label="C_element : 0.502"  # scripted group (container) (typed FeaturePython)
  n = 0.501611
FEATURE [App::DocumentObjectGroupPython] O_element019  label="O_element : 0.005"  # scripted group (container) (typed FeaturePython)
  n = 0.004527
FEATURE [App::DocumentObjectGroupPython] F_element004  label="F_element : 0.465"  # scripted group (container) (typed FeaturePython)
  n = 0.465209
FEATURE [App::DocumentObjectGroupPython] Si_element001  label="Si_element : 0.004"  # scripted group (container) (typed FeaturePython)
  n = 0.003973
FEATURE [App::DocumentObjectGroupPython] G4_C_552  label="G4_C-552"  # scripted group (container) (typed FeaturePython)
  Dunit = g/cm3
  Dvalue = 1.76
  Group = -> [H_element020,C_element021,O_element019,F_element004,Si_element001]
  conduct = 2
  density = 1
  expand = 3
  formula = G4_C-552
  name = G4_C-552
  specific = 4
FEATURE [App::DocumentObjectGroupPython] Cd_element001  label="Cd_element : 1"  # scripted group (container) (typed FeaturePython)
  n = 1
  ref = Cd_element
FEATURE [App::DocumentObjectGroupPython] Te_element001  label="Te_element : 1"  # scripted group (container) (typed FeaturePython)
  n = 1
  ref = Te_element
FEATURE [App::DocumentObjectGroupPython] G4_CADMIUM_TELLURIDE  # scripted group (container) (typed FeaturePython)
  Dunit = g/cm3
  Dvalue = 6.2
  Group = -> [Cd_element001,Te_element001]
  conduct = 2
  density = 1
  expand = 3
  formula = G4_CADMIUM_TELLURIDE
  name = G4_CADMIUM_TELLURIDE
  specific = 4
FEATURE [App::DocumentObjectGroupPython] Cd_element002  label="Cd_element : 002"  # scripted group (container) (typed FeaturePython)
  n = 1
  ref = Cd_element
FEATURE [App::DocumentObjectGroupPython] W_element001  label="W_element : 1"  # scripted group (container) (typed FeaturePython)
  n = 1
  ref = W_element
FEATURE [App::DocumentObjectGroupPython] O_element020  label="O_element : 008"  # scripted group (container) (typed FeaturePython)
  n = 4
  ref = O_element
FEATURE [App::DocumentObjectGroupPython] G4_CADMIUM_TUNGSTATE  # scripted group (container) (typed FeaturePython)
  Dunit = g/cm3
  Dvalue = 7.9
  Group = -> [Cd_element002,W_element001,O_element020]
  conduct = 2
  density = 1
  expand = 3
  formula = G4_CADMIUM_TUNGSTATE
  name = G4_CADMIUM_TUNGSTATE
  specific = 4
FEATURE [App::DocumentObjectGroupPython] Ca_element005  label="Ca_element : 1"  # scripted group (container) (typed FeaturePython)
  n = 1
  ref = Ca_element
FEATURE [App::DocumentObjectGroupPython] C_element022  label="C_element : 009"  # scripted group (container) (typed FeaturePython)
  n = 1
  ref = C_element
FEATURE [App::DocumentObjectGroupPython] O_element021  label="O_element : 009"  # scripted group (container) (typed FeaturePython)
  n = 3
  ref = O_element
FEATURE [App::DocumentObjectGroupPython] G4_CALCIUM_CARBONATE  # scripted group (container) (typed FeaturePython)
  Dunit = g/cm3
  Dvalue = 2.8
  Group = -> [Ca_element005,C_element022,O_element021]
  conduct = 2
  density = 1
  expand = 3
  formula = G4_CALCIUM_CARBONATE
  name = G4_CALCIUM_CARBONATE
  specific = 4
FEATURE [App::DocumentObjectGroupPython] Ca_element006  label="Ca_element : 002"  # scripted group (container) (typed FeaturePython)
  n = 1
  ref = Ca_element
FEATURE [App::DocumentObjectGroupPython] F_element005  label="F_element : 003"  # scripted group (container) (typed FeaturePython)
  n = 2
  ref = F_element
FEATURE [App::DocumentObjectGroupPython] G4_CALCIUM_FLUORIDE  # scripted group (container) (typed FeaturePython)
  Dunit = g/cm3
  Dvalue = 3.18
  Group = -> [Ca_element006,F_element005]
  conduct = 2
  density = 1
  expand = 3
  formula = G4_CALCIUM_FLUORIDE
  name = G4_CALCIUM_FLUORIDE
  specific = 4
FEATURE [App::DocumentObjectGroupPython] Ca_element007  label="Ca_element : 003"  # scripted group (container) (typed FeaturePython)
  n = 1
  ref = Ca_element
FEATURE [App::DocumentObjectGroupPython] O_element022  label="O_element : 010"  # scripted group (container) (typed FeaturePython)
  n = 1
  ref = O_element
FEATURE [App::DocumentObjectGroupPython] G4_CALCIUM_OXIDE  # scripted group (container) (typed FeaturePython)
  Dunit = g/cm3
  Dvalue = 3.3
  Group = -> [Ca_element007,O_element022]
  conduct = 2
  density = 1
  expand = 3
  formula = G4_CALCIUM_OXIDE
  name = G4_CALCIUM_OXIDE
  specific = 4
FEATURE [App::DocumentObjectGroupPython] Ca_element008  label="Ca_element : 004"  # scripted group (container) (typed FeaturePython)
  n = 1
  ref = Ca_element
FEATURE [App::DocumentObjectGroupPython] S_element007  label="S_element : 002"  # scripted group (container) (typed FeaturePython)
  n = 1
  ref = S_element
FEATURE [App::DocumentObjectGroupPython] O_element023  label="O_element : 011"  # scripted group (container) (typed FeaturePython)
  n = 4
  ref = O_element
FEATURE [App::DocumentObjectGroupPython] G4_CALCIUM_SULFATE  # scripted group (container) (typed FeaturePython)
  Dunit = g/cm3
  Dvalue = 2.96
  Group = -> [Ca_element008,S_element007,O_element023]
  conduct = 2
  density = 1
  expand = 3
  formula = G4_CALCIUM_SULFATE
  name = G4_CALCIUM_SULFATE
  specific = 4
FEATURE [App::DocumentObjectGroupPython] Ca_element009  label="Ca_element : 005"  # scripted group (container) (typed FeaturePython)
  n = 1
  ref = Ca_element
FEATURE [App::DocumentObjectGroupPython] W_element002  label="W_element : 002"  # scripted group (container) (typed FeaturePython)
  n = 1
  ref = W_element
FEATURE [App::DocumentObjectGroupPython] O_element024  label="O_element : 012"  # scripted group (container) (typed FeaturePython)
  n = 4
  ref = O_element
FEATURE [App::DocumentObjectGroupPython] G4_CALCIUM_TUNGSTATE  # scripted group (container) (typed FeaturePython)
  Dunit = g/cm3
  Dvalue = 6.062
  Group = -> [Ca_element009,W_element002,O_element024]
  conduct = 2
  density = 1
  expand = 3
  formula = G4_CALCIUM_TUNGSTATE
  name = G4_CALCIUM_TUNGSTATE
  specific = 4
FEATURE [App::DocumentObjectGroupPython] C_element023  label="C_element : 010"  # scripted group (container) (typed FeaturePython)
  n = 1
  ref = C_element
FEATURE [App::DocumentObjectGroupPython] O_element025  label="O_element : 013"  # scripted group (container) (typed FeaturePython)
  n = 2
  ref = O_element
FEATURE [App::DocumentObjectGroupPython] G4_CARBON_DIOXIDE  # scripted group (container) (typed FeaturePython)
  Dunit = g/cm3
  Dvalue = 0.00184212
  Group = -> [C_element023,O_element025]
  conduct = 2
  density = 1
  expand = 3
  formula = G4_CARBON_DIOXIDE
  name = G4_CARBON_DIOXIDE
  specific = 4
FEATURE [App::DocumentObjectGroupPython] C_element024  label="C_element : 011"  # scripted group (container) (typed FeaturePython)
  n = 1
  ref = C_element
FEATURE [App::DocumentObjectGroupPython] Cl_element004  label="Cl_element : 4"  # scripted group (container) (typed FeaturePython)
  n = 4
  ref = Cl_element
FEATURE [App::DocumentObjectGroupPython] G4_CARBON_TETRACHLORIDE  # scripted group (container) (typed FeaturePython)
  Dunit = g/cm3
  Dvalue = 1.594
  Group = -> [C_element024,Cl_element004]
  conduct = 2
  density = 1
  expand = 3
  formula = G4_CARBON_TETRACHLORIDE
  name = G4_CARBON_TETRACHLORIDE
  specific = 4
FEATURE [App::DocumentObjectGroupPython] C_element025  label="C_element : 012"  # scripted group (container) (typed FeaturePython)
  n = 6
  ref = C_element
FEATURE [App::DocumentObjectGroupPython] H_element021  label="H_element : 012"  # scripted group (container) (typed FeaturePython)
  n = 10
  ref = H_element
FEATURE [App::DocumentObjectGroupPython] O_element026  label="O_element : 5"  # scripted group (container) (typed FeaturePython)
  n = 5
  ref = O_element
FEATURE [App::DocumentObjectGroupPython] G4_CELLULOSE_CELLOPHANE  # scripted group (container) (typed FeaturePython)
  Dunit = g/cm3
  Dvalue = 1.42
  Group = -> [C_element025,H_element021,O_element026]
  conduct = 2
  density = 1
  expand = 3
  formula = G4_CELLULOSE_CELLOPHANE
  name = G4_CELLULOSE_CELLOPHANE
  specific = 4
FEATURE [App::DocumentObjectGroupPython] H_element022  label="H_element : 0.067"  # scripted group (container) (typed FeaturePython)
  n = 0.067125
FEATURE [App::DocumentObjectGroupPython] C_element026  label="C_element : 0.545"  # scripted group (container) (typed FeaturePython)
  n = 0.545403
FEATURE [App::DocumentObjectGroupPython] O_element027  label="O_element : 0.387"  # scripted group (container) (typed FeaturePython)
  n = 0.387472
FEATURE [App::DocumentObjectGroupPython] G4_CELLULOSE_BUTYRATE  # scripted group (container) (typed FeaturePython)
  Dunit = g/cm3
  Dvalue = 1.2
  Group = -> [H_element022,C_element026,O_element027]
  conduct = 2
  density = 1
  expand = 3
  formula = G4_CELLULOSE_BUTYRATE
  name = G4_CELLULOSE_BUTYRATE
  specific = 4
FEATURE [App::DocumentObjectGroupPython] H_element023  label="H_element : 0.029"  # scripted group (container) (typed FeaturePython)
  n = 0.029216
FEATURE [App::DocumentObjectGroupPython] C_element027  label="C_element : 0.271"  # scripted group (container) (typed FeaturePython)
  n = 0.271296
FEATURE [App::DocumentObjectGroupPython] N_element013  label="N_element : 0.121"  # scripted group (container) (typed FeaturePython)
  n = 0.121276
FEATURE [App::DocumentObjectGroupPython] O_element028  label="O_element : 0.578"  # scripted group (container) (typed FeaturePython)
  n = 0.578212
FEATURE [App::DocumentObjectGroupPython] G4_CELLULOSE_NITRATE  # scripted group (container) (typed FeaturePython)
  Dunit = g/cm3
  Dvalue = 1.49
  Group = -> [H_element023,C_element027,N_element013,O_element028]
  conduct = 2
  density = 1
  expand = 3
  formula = G4_CELLULOSE_NITRATE
  name = G4_CELLULOSE_NITRATE
  specific = 4
FEATURE [App::DocumentObjectGroupPython] H_element024  label="H_element : 0.108"  # scripted group (container) (typed FeaturePython)
  n = 0.107596
FEATURE [App::DocumentObjectGroupPython] N_element014  label="N_element : 0.001"  # scripted group (container) (typed FeaturePython)
  n = 0.0008
FEATURE [App::DocumentObjectGroupPython] O_element029  label="O_element : 0.875"  # scripted group (container) (typed FeaturePython)
  n = 0.874976
FEATURE [App::DocumentObjectGroupPython] S_element008  label="S_element : 0.015"  # scripted group (container) (typed FeaturePython)
  n = 0.014627
FEATURE [App::DocumentObjectGroupPython] Ce_element001  label="Ce_element : 0.002"  # scripted group (container) (typed FeaturePython)
  n = 0.002001
FEATURE [App::DocumentObjectGroupPython] G4_CERIC_SULFATE  # scripted group (container) (typed FeaturePython)
  Dunit = g/cm3
  Dvalue = 1.03
  Group = -> [H_element024,N_element014,O_element029,S_element008,Ce_element001]
  conduct = 2
  density = 1
  expand = 3
  formula = G4_CERIC_SULFATE
  name = G4_CERIC_SULFATE
  specific = 4
FEATURE [App::DocumentObjectGroupPython] Cs_element001  label="Cs_element : 1"  # scripted group (container) (typed FeaturePython)
  n = 1
  ref = Cs_element
FEATURE [App::DocumentObjectGroupPython] F_element006  label="F_element : 1"  # scripted group (container) (typed FeaturePython)
  n = 1
  ref = F_element
FEATURE [App::DocumentObjectGroupPython] G4_CESIUM_FLUORIDE  # scripted group (container) (typed FeaturePython)
  Dunit = g/cm3
  Dvalue = 4.115
  Group = -> [Cs_element001,F_element006]
  conduct = 2
  density = 1
  expand = 3
  formula = G4_CESIUM_FLUORIDE
  name = G4_CESIUM_FLUORIDE
  specific = 4
FEATURE [App::DocumentObjectGroupPython] Cs_element002  label="Cs_element : 002"  # scripted group (container) (typed FeaturePython)
  n = 1
  ref = Cs_element
FEATURE [App::DocumentObjectGroupPython] I_element001  label="I_element : 1"  # scripted group (container) (typed FeaturePython)
  n = 1
  ref = I_element
FEATURE [App::DocumentObjectGroupPython] G4_CESIUM_IODIDE  # scripted group (container) (typed FeaturePython)
  Dunit = g/cm3
  Dvalue = 4.51
  Group = -> [Cs_element002,I_element001]
  conduct = 2
  density = 1
  expand = 3
  formula = G4_CESIUM_IODIDE
  name = G4_CESIUM_IODIDE
  specific = 4
FEATURE [App::DocumentObjectGroupPython] C_element028  label="C_element : 013"  # scripted group (container) (typed FeaturePython)
  n = 6
  ref = C_element
FEATURE [App::DocumentObjectGroupPython] H_element025  label="H_element : 013"  # scripted group (container) (typed FeaturePython)
  n = 5
  ref = H_element
FEATURE [App::DocumentObjectGroupPython] Cl_element005  label="Cl_element : 1"  # scripted group (container) (typed FeaturePython)
  n = 1
  ref = Cl_element
FEATURE [App::DocumentObjectGroupPython] G4_CHLOROBENZENE  # scripted group (container) (typed FeaturePython)
  Dunit = g/cm3
  Dvalue = 1.1058
  Group = -> [C_element028,H_element025,Cl_element005]
  conduct = 2
  density = 1
  expand = 3
  formula = G4_CHLOROBENZENE
  name = G4_CHLOROBENZENE
  specific = 4
FEATURE [App::DocumentObjectGroupPython] C_element029  label="C_element : 014"  # scripted group (container) (typed FeaturePython)
  n = 1
  ref = C_element
FEATURE [App::DocumentObjectGroupPython] H_element026  label="H_element : 1"  # scripted group (container) (typed FeaturePython)
  n = 1
  ref = H_element
FEATURE [App::DocumentObjectGroupPython] Cl_element006  label="Cl_element : 3"  # scripted group (container) (typed FeaturePython)
  n = 3
  ref = Cl_element
FEATURE [App::DocumentObjectGroupPython] G4_CHLOROFORM  # scripted group (container) (typed FeaturePython)
  Dunit = g/cm3
  Dvalue = 1.4832
  Group = -> [C_element029,H_element026,Cl_element006]
  conduct = 2
  density = 1
  expand = 3
  formula = G4_CHLOROFORM
  name = G4_CHLOROFORM
  specific = 4
FEATURE [App::DocumentObjectGroupPython] H_element027  label="H_element : 0.010"  # scripted group (container) (typed FeaturePython)
  n = 0.01
FEATURE [App::DocumentObjectGroupPython] C_element030  label="C_element : 0.001"  # scripted group (container) (typed FeaturePython)
  n = 0.001
FEATURE [App::DocumentObjectGroupPython] O_element030  label="O_element : 0.529"  # scripted group (container) (typed FeaturePython)
  n = 0.529107
FEATURE [App::DocumentObjectGroupPython] Na_element005  label="Na_element : 0.016"  # scripted group (container) (typed FeaturePython)
  n = 0.016
FEATURE [App::DocumentObjectGroupPython] Mg_element003  label="Mg_element : 0.004"  # scripted group (container) (typed FeaturePython)
  n = 0.002
FEATURE [App::DocumentObjectGroupPython] Al_element002  label="Al_element : 0.034"  # scripted group (container) (typed FeaturePython)
  n = 0.033872
FEATURE [App::DocumentObjectGroupPython] Si_element002  label="Si_element : 0.337"  # scripted group (container) (typed FeaturePython)
  n = 0.337021
FEATURE [App::DocumentObjectGroupPython] K_element003  label="K_element : 0.013"  # scripted group (container) (typed FeaturePython)
  n = 0.013
FEATURE [App::DocumentObjectGroupPython] Ca_element010  label="Ca_element : 0.044"  # scripted group (container) (typed FeaturePython)
  n = 0.044
FEATURE [App::DocumentObjectGroupPython] Fe_element002  label="Fe_element : 0.014"  # scripted group (container) (typed FeaturePython)
  n = 0.014
FEATURE [App::DocumentObjectGroupPython] G4_CONCRETE  # scripted group (container) (typed FeaturePython)
  Dunit = g/cm3
  Dvalue = 2.3
  Group = -> [H_element027,C_element030,O_element030,Na_element005,Mg_element003,Al_element002,Si_element002,K_element003,Ca_element010,Fe_element002]
  conduct = 2
  density = 1
  expand = 3
  formula = G4_CONCRETE
  name = G4_CONCRETE
  specific = 4
FEATURE [App::DocumentObjectGroupPython] C_element031  label="C_element : 015"  # scripted group (container) (typed FeaturePython)
  n = 6
  ref = C_element
FEATURE [App::DocumentObjectGroupPython] H_element028  label="H_element : 12"  # scripted group (container) (typed FeaturePython)
  n = 12
  ref = H_element
FEATURE [App::DocumentObjectGroupPython] G4_CYCLOHEXANE  # scripted group (container) (typed FeaturePython)
  Dunit = g/cm3
  Dvalue = 0.779
  Group = -> [C_element031,H_element028]
  conduct = 2
  density = 1
  expand = 3
  formula = G4_CYCLOHEXANE
  name = G4_CYCLOHEXANE
  specific = 4
FEATURE [App::DocumentObjectGroupPython] C_element032  label="C_element : 016"  # scripted group (container) (typed FeaturePython)
  n = 6
  ref = C_element
FEATURE [App::DocumentObjectGroupPython] H_element029  label="H_element : 4"  # scripted group (container) (typed FeaturePython)
  n = 4
  ref = H_element
FEATURE [App::DocumentObjectGroupPython] Cl_element007  label="Cl_element : 2"  # scripted group (container) (typed FeaturePython)
  n = 2
  ref = Cl_element
FEATURE [App::DocumentObjectGroupPython] G4_1_2_DICHLOROBENZENE  label="G4_1.2-DICHLOROBENZENE"  # scripted group (container) (typed FeaturePython)
  Dunit = g/cm3
  Dvalue = 1.3048
  Group = -> [C_element032,H_element029,Cl_element007]
  conduct = 2
  density = 1
  expand = 3
  formula = G4_1.2-DICHLOROBENZENE
  name = G4_1.2-DICHLOROBENZENE
  specific = 4
FEATURE [App::DocumentObjectGroupPython] C_element033  label="C_element : 017"  # scripted group (container) (typed FeaturePython)
  n = 4
  ref = C_element
FEATURE [App::DocumentObjectGroupPython] H_element030  label="H_element : 8"  # scripted group (container) (typed FeaturePython)
  n = 8
  ref = H_element
FEATURE [App::DocumentObjectGroupPython] O_element031  label="O_element : 014"  # scripted group (container) (typed FeaturePython)
  n = 1
  ref = O_element
FEATURE [App::DocumentObjectGroupPython] Cl_element008  label="Cl_element : 005"  # scripted group (container) (typed FeaturePython)
  n = 2
  ref = Cl_element
FEATURE [App::DocumentObjectGroupPython] G4_DICHLORODIETHYL_ETHER  # scripted group (container) (typed FeaturePython)
  Dunit = g/cm3
  Dvalue = 1.2199
  Group = -> [C_element033,H_element030,O_element031,Cl_element008]
  conduct = 2
  density = 1
  expand = 3
  formula = G4_DICHLORODIETHYL_ETHER
  name = G4_DICHLORODIETHYL_ETHER
  specific = 4
FEATURE [App::DocumentObjectGroupPython] C_element034  label="C_element : 018"  # scripted group (container) (typed FeaturePython)
  n = 2
  ref = C_element
FEATURE [App::DocumentObjectGroupPython] H_element031  label="H_element : 014"  # scripted group (container) (typed FeaturePython)
  n = 4
  ref = H_element
FEATURE [App::DocumentObjectGroupPython] Cl_element009  label="Cl_element : 006"  # scripted group (container) (typed FeaturePython)
  n = 2
  ref = Cl_element
FEATURE [App::DocumentObjectGroupPython] G4_1_2_DICHLOROETHANE  label="G4_1.2-DICHLOROETHANE"  # scripted group (container) (typed FeaturePython)
  Dunit = g/cm3
  Dvalue = 1.2351
  Group = -> [C_element034,H_element031,Cl_element009]
  conduct = 2
  density = 1
  expand = 3
  formula = G4_1.2-DICHLOROETHANE
  name = G4_1.2-DICHLOROETHANE
  specific = 4
FEATURE [App::DocumentObjectGroupPython] C_element035  label="C_element : 019"  # scripted group (container) (typed FeaturePython)
  n = 4
  ref = C_element
FEATURE [App::DocumentObjectGroupPython] H_element032  label="H_element : 015"  # scripted group (container) (typed FeaturePython)
  n = 10
  ref = H_element
FEATURE [App::DocumentObjectGroupPython] O_element032  label="O_element : 015"  # scripted group (container) (typed FeaturePython)
  n = 1
  ref = O_element
FEATURE [App::DocumentObjectGroupPython] G4_DIETHYL_ETHER  # scripted group (container) (typed FeaturePython)
  Dunit = g/cm3
  Dvalue = 0.71378
  Group = -> [C_element035,H_element032,O_element032]
  conduct = 2
  density = 1
  expand = 3
  formula = G4_DIETHYL_ETHER
  name = G4_DIETHYL_ETHER
  specific = 4
FEATURE [App::DocumentObjectGroupPython] C_element036  label="C_element : 020"  # scripted group (container) (typed FeaturePython)
  n = 3
  ref = C_element
FEATURE [App::DocumentObjectGroupPython] H_element033  label="H_element : 016"  # scripted group (container) (typed FeaturePython)
  n = 7
  ref = H_element
FEATURE [App::DocumentObjectGroupPython] N_element015  label="N_element : 008"  # scripted group (container) (typed FeaturePython)
  n = 1
  ref = N_element
FEATURE [App::DocumentObjectGroupPython] O_element033  label="O_element : 016"  # scripted group (container) (typed FeaturePython)
  n = 1
  ref = O_element
FEATURE [App::DocumentObjectGroupPython] G4_N_N_DIMETHYL_FORMAMIDE  label="G4_N.N-DIMETHYL_FORMAMIDE"  # scripted group (container) (typed FeaturePython)
  Dunit = g/cm3
  Dvalue = 0.9487
  Group = -> [C_element036,H_element033,N_element015,O_element033]
  conduct = 2
  density = 1
  expand = 3
  formula = G4_N.N-DIMETHYL_FORMAMIDE
  name = G4_N.N-DIMETHYL_FORMAMIDE
  specific = 4
FEATURE [App::DocumentObjectGroupPython] C_element037  label="C_element : 021"  # scripted group (container) (typed FeaturePython)
  n = 2
  ref = C_element
FEATURE [App::DocumentObjectGroupPython] H_element034  label="H_element : 017"  # scripted group (container) (typed FeaturePython)
  n = 6
  ref = H_element
FEATURE [App::DocumentObjectGroupPython] O_element034  label="O_element : 017"  # scripted group (container) (typed FeaturePython)
  n = 1
  ref = O_element
FEATURE [App::DocumentObjectGroupPython] S_element009  label="S_element : 003"  # scripted group (container) (typed FeaturePython)
  n = 1
  ref = S_element
FEATURE [App::DocumentObjectGroupPython] G4_DIMETHYL_SULFOXIDE  # scripted group (container) (typed FeaturePython)
  Dunit = g/cm3
  Dvalue = 1.1014
  Group = -> [C_element037,H_element034,O_element034,S_element009]
  conduct = 2
  density = 1
  expand = 3
  formula = G4_DIMETHYL_SULFOXIDE
  name = G4_DIMETHYL_SULFOXIDE
  specific = 4
FEATURE [App::DocumentObjectGroupPython] C_element038  label="C_element : 022"  # scripted group (container) (typed FeaturePython)
  n = 2
  ref = C_element
FEATURE [App::DocumentObjectGroupPython] H_element035  label="H_element : 018"  # scripted group (container) (typed FeaturePython)
  n = 6
  ref = H_element
FEATURE [App::DocumentObjectGroupPython] G4_ETHANE  # scripted group (container) (typed FeaturePython)
  Dunit = g/cm3
  Dvalue = 0.00125324
  Group = -> [C_element038,H_element035]
  conduct = 2
  density = 1
  expand = 3
  formula = G4_ETHANE
  name = G4_ETHANE
  specific = 4
FEATURE [App::DocumentObjectGroupPython] C_element039  label="C_element : 023"  # scripted group (container) (typed FeaturePython)
  n = 2
  ref = C_element
FEATURE [App::DocumentObjectGroupPython] H_element036  label="H_element : 019"  # scripted group (container) (typed FeaturePython)
  n = 6
  ref = H_element
FEATURE [App::DocumentObjectGroupPython] O_element035  label="O_element : 018"  # scripted group (container) (typed FeaturePython)
  n = 1
  ref = O_element
FEATURE [App::DocumentObjectGroupPython] G4_ETHYL_ALCOHOL  # scripted group (container) (typed FeaturePython)
  Dunit = g/cm3
  Dvalue = 0.7893
  Group = -> [C_element039,H_element036,O_element035]
  conduct = 2
  density = 1
  expand = 3
  formula = G4_ETHYL_ALCOHOL
  name = G4_ETHYL_ALCOHOL
  specific = 4
FEATURE [App::DocumentObjectGroupPython] H_element037  label="H_element : 0.090"  # scripted group (container) (typed FeaturePython)
  n = 0.090027
FEATURE [App::DocumentObjectGroupPython] C_element040  label="C_element : 0.585"  # scripted group (container) (typed FeaturePython)
  n = 0.585182
FEATURE [App::DocumentObjectGroupPython] O_element036  label="O_element : 0.325"  # scripted group (container) (typed FeaturePython)
  n = 0.324791
FEATURE [App::DocumentObjectGroupPython] G4_ETHYL_CELLULOSE  # scripted group (container) (typed FeaturePython)
  Dunit = g/cm3
  Dvalue = 1.13
  Group = -> [H_element037,C_element040,O_element036]
  conduct = 2
  density = 1
  expand = 3
  formula = G4_ETHYL_CELLULOSE
  name = G4_ETHYL_CELLULOSE
  specific = 4
FEATURE [App::DocumentObjectGroupPython] C_element041  label="C_element : 024"  # scripted group (container) (typed FeaturePython)
  n = 2
  ref = C_element
FEATURE [App::DocumentObjectGroupPython] H_element038  label="H_element : 020"  # scripted group (container) (typed FeaturePython)
  n = 4
  ref = H_element
FEATURE [App::DocumentObjectGroupPython] G4_ETHYLENE  # scripted group (container) (typed FeaturePython)
  Dunit = g/cm3
  Dvalue = 0.00117497
  Group = -> [C_element041,H_element038]
  conduct = 2
  density = 1
  expand = 3
  formula = G4_ETHYLENE
  name = G4_ETHYLENE
  specific = 4
FEATURE [App::DocumentObjectGroupPython] H_element039  label="H_element : 0.096"  # scripted group (container) (typed FeaturePython)
  n = 0.096
FEATURE [App::DocumentObjectGroupPython] C_element042  label="C_element : 0.195"  # scripted group (container) (typed FeaturePython)
  n = 0.195
FEATURE [App::DocumentObjectGroupPython] N_element016  label="N_element : 0.057"  # scripted group (container) (typed FeaturePython)
  n = 0.057
FEATURE [App::DocumentObjectGroupPython] O_element037  label="O_element : 0.646"  # scripted group (container) (typed FeaturePython)
  n = 0.646
FEATURE [App::DocumentObjectGroupPython] Na_element006  label="Na_element : 0.017"  # scripted group (container) (typed FeaturePython)
  n = 0.001
FEATURE [App::DocumentObjectGroupPython] P_element005  label="P_element : 0.104"  # scripted group (container) (typed FeaturePython)
  n = 0.001
FEATURE [App::DocumentObjectGroupPython] S_element010  label="S_element : 0.016"  # scripted group (container) (typed FeaturePython)
  n = 0.003
FEATURE [App::DocumentObjectGroupPython] Cl_element010  label="Cl_element : 0.005"  # scripted group (container) (typed FeaturePython)
  n = 0.001
FEATURE [App::DocumentObjectGroupPython] G4_EYE_LENS_ICRP  # scripted group (container) (typed FeaturePython)
  Dunit = g/cm3
  Dvalue = 1.07
  Group = -> [H_element039,C_element042,N_element016,O_element037,Na_element006,P_element005,S_element010,Cl_element010]
  conduct = 2
  density = 1
  expand = 3
  formula = G4_EYE_LENS_ICRP
  name = G4_EYE_LENS_ICRP
  specific = 4
FEATURE [App::DocumentObjectGroupPython] Fe_element003  label="Fe_element : 2"  # scripted group (container) (typed FeaturePython)
  n = 2
  ref = Fe_element
FEATURE [App::DocumentObjectGroupPython] O_element038  label="O_element : 019"  # scripted group (container) (typed FeaturePython)
  n = 3
  ref = O_element
FEATURE [App::DocumentObjectGroupPython] G4_FERRIC_OXIDE  # scripted group (container) (typed FeaturePython)
  Dunit = g/cm3
  Dvalue = 5.2
  Group = -> [Fe_element003,O_element038]
  conduct = 2
  density = 1
  expand = 3
  formula = G4_FERRIC_OXIDE
  name = G4_FERRIC_OXIDE
  specific = 4
FEATURE [App::DocumentObjectGroupPython] Fe_element004  label="Fe_element : 1"  # scripted group (container) (typed FeaturePython)
  n = 1
  ref = Fe_element
FEATURE [App::DocumentObjectGroupPython] B_element003  label="B_element : 1"  # scripted group (container) (typed FeaturePython)
  n = 1
  ref = B_element
FEATURE [App::DocumentObjectGroupPython] G4_FERROBORIDE  # scripted group (container) (typed FeaturePython)
  Dunit = g/cm3
  Dvalue = 7.15
  Group = -> [Fe_element004,B_element003]
  conduct = 2
  density = 1
  expand = 3
  formula = G4_FERROBORIDE
  name = G4_FERROBORIDE
  specific = 4
FEATURE [App::DocumentObjectGroupPython] Fe_element005  label="Fe_element : 003"  # scripted group (container) (typed FeaturePython)
  n = 1
  ref = Fe_element
FEATURE [App::DocumentObjectGroupPython] O_element039  label="O_element : 020"  # scripted group (container) (typed FeaturePython)
  n = 1
  ref = O_element
FEATURE [App::DocumentObjectGroupPython] G4_FERROUS_OXIDE  # scripted group (container) (typed FeaturePython)
  Dunit = g/cm3
  Dvalue = 5.7
  Group = -> [Fe_element005,O_element039]
  conduct = 2
  density = 1
  expand = 3
  formula = G4_FERROUS_OXIDE
  name = G4_FERROUS_OXIDE
  specific = 4
FEATURE [App::DocumentObjectGroupPython] H_element040  label="H_element : 0.115"  # scripted group (container) (typed FeaturePython)
  n = 0.108259
FEATURE [App::DocumentObjectGroupPython] N_element017  label="N_element : 0.000"  # scripted group (container) (typed FeaturePython)
  n = 2.7e-05
FEATURE [App::DocumentObjectGroupPython] O_element040  label="O_element : 0.879"  # scripted group (container) (typed FeaturePython)
  n = 0.878636
FEATURE [App::DocumentObjectGroupPython] Na_element007  label="Na_element : 0.000"  # scripted group (container) (typed FeaturePython)
  n = 2.2e-05
FEATURE [App::DocumentObjectGroupPython] S_element011  label="S_element : 0.013"  # scripted group (container) (typed FeaturePython)
  n = 0.012968
FEATURE [App::DocumentObjectGroupPython] Cl_element011  label="Cl_element : 0.000"  # scripted group (container) (typed FeaturePython)
  n = 3.4e-05
FEATURE [App::DocumentObjectGroupPython] Fe_element006  label="Fe_element : 0.000"  # scripted group (container) (typed FeaturePython)
  n = 5.4e-05
FEATURE [App::DocumentObjectGroupPython] G4_FERROUS_SULFATE  # scripted group (container) (typed FeaturePython)
  Dunit = g/cm3
  Dvalue = 1.024
  Group = -> [H_element040,N_element017,O_element040,Na_element007,S_element011,Cl_element011,Fe_element006]
  conduct = 2
  density = 1
  expand = 3
  formula = G4_FERROUS_SULFATE
  name = G4_FERROUS_SULFATE
  specific = 4
FEATURE [App::DocumentObjectGroupPython] C_element043  label="C_element : 0.099"  # scripted group (container) (typed FeaturePython)
  n = 0.099335
FEATURE [App::DocumentObjectGroupPython] F_element007  label="F_element : 0.314"  # scripted group (container) (typed FeaturePython)
  n = 0.314247
FEATURE [App::DocumentObjectGroupPython] Cl_element012  label="Cl_element : 0.586"  # scripted group (container) (typed FeaturePython)
  n = 0.586418
FEATURE [App::DocumentObjectGroupPython] G4_FREON_12  label="G4_FREON-12"  # scripted group (container) (typed FeaturePython)
  Dunit = g/cm3
  Dvalue = 1.12
  Group = -> [C_element043,F_element007,Cl_element012]
  conduct = 2
  density = 1
  expand = 3
  formula = G4_FREON-12
  name = G4_FREON-12
  specific = 4
FEATURE [App::DocumentObjectGroupPython] C_element044  label="C_element : 0.057"  # scripted group (container) (typed FeaturePython)
  n = 0.057245
FEATURE [App::DocumentObjectGroupPython] F_element008  label="F_element : 0.181"  # scripted group (container) (typed FeaturePython)
  n = 0.181096
FEATURE [App::DocumentObjectGroupPython] Br_element001  label="Br_element : 0.762"  # scripted group (container) (typed FeaturePython)
  n = 0.761659
FEATURE [App::DocumentObjectGroupPython] G4_FREON_12B2  label="G4_FREON-12B2"  # scripted group (container) (typed FeaturePython)
  Dunit = g/cm3
  Dvalue = 1.8
  Group = -> [C_element044,F_element008,Br_element001]
  conduct = 2
  density = 1
  expand = 3
  formula = G4_FREON-12B2
  name = G4_FREON-12B2
  specific = 4
FEATURE [App::DocumentObjectGroupPython] C_element045  label="C_element : 0.115"  # scripted group (container) (typed FeaturePython)
  n = 0.114983
FEATURE [App::DocumentObjectGroupPython] F_element009  label="F_element : 0.546"  # scripted group (container) (typed FeaturePython)
  n = 0.545621
FEATURE [App::DocumentObjectGroupPython] Cl_element013  label="Cl_element : 0.339"  # scripted group (container) (typed FeaturePython)
  n = 0.339396
FEATURE [App::DocumentObjectGroupPython] G4_FREON_13  label="G4_FREON-13"  # scripted group (container) (typed FeaturePython)
  Dunit = g/cm3
  Dvalue = 0.95
  Group = -> [C_element045,F_element009,Cl_element013]
  conduct = 2
  density = 1
  expand = 3
  formula = G4_FREON-13
  name = G4_FREON-13
  specific = 4
FEATURE [App::DocumentObjectGroupPython] C_element046  label="C_element : 025"  # scripted group (container) (typed FeaturePython)
  n = 1
  ref = C_element
FEATURE [App::DocumentObjectGroupPython] F_element010  label="F_element : 3"  # scripted group (container) (typed FeaturePython)
  n = 3
  ref = F_element
FEATURE [App::DocumentObjectGroupPython] Br_element002  label="Br_element : 1"  # scripted group (container) (typed FeaturePython)
  n = 1
  ref = Br_element
FEATURE [App::DocumentObjectGroupPython] G4_FREON_13B1  label="G4_FREON-13B1"  # scripted group (container) (typed FeaturePython)
  Dunit = g/cm3
  Dvalue = 1.5
  Group = -> [C_element046,F_element010,Br_element002]
  conduct = 2
  density = 1
  expand = 3
  formula = G4_FREON-13B1
  name = G4_FREON-13B1
  specific = 4
FEATURE [App::DocumentObjectGroupPython] C_element047  label="C_element : 0.061"  # scripted group (container) (typed FeaturePython)
  n = 0.061309
FEATURE [App::DocumentObjectGroupPython] F_element011  label="F_element : 0.291"  # scripted group (container) (typed FeaturePython)
  n = 0.290924
FEATURE [App::DocumentObjectGroupPython] I_element002  label="I_element : 0.648"  # scripted group (container) (typed FeaturePython)
  n = 0.647767
FEATURE [App::DocumentObjectGroupPython] G4_FREON_13I1  label="G4_FREON-13I1"  # scripted group (container) (typed FeaturePython)
  Dunit = g/cm3
  Dvalue = 1.8
  Group = -> [C_element047,F_element011,I_element002]
  conduct = 2
  density = 1
  expand = 3
  formula = G4_FREON-13I1
  name = G4_FREON-13I1
  specific = 4
FEATURE [App::DocumentObjectGroupPython] Gd_element001  label="Gd_element : 2"  # scripted group (container) (typed FeaturePython)
  n = 2
  ref = Gd_element
FEATURE [App::DocumentObjectGroupPython] O_element041  label="O_element : 021"  # scripted group (container) (typed FeaturePython)
  n = 2
  ref = O_element
FEATURE [App::DocumentObjectGroupPython] S_element012  label="S_element : 004"  # scripted group (container) (typed FeaturePython)
  n = 1
  ref = S_element
FEATURE [App::DocumentObjectGroupPython] G4_GADOLINIUM_OXYSULFIDE  # scripted group (container) (typed FeaturePython)
  Dunit = g/cm3
  Dvalue = 7.44
  Group = -> [Gd_element001,O_element041,S_element012]
  conduct = 2
  density = 1
  expand = 3
  formula = G4_GADOLINIUM_OXYSULFIDE
  name = G4_GADOLINIUM_OXYSULFIDE
  specific = 4
FEATURE [App::DocumentObjectGroupPython] Ga_element001  label="Ga_element : 1"  # scripted group (container) (typed FeaturePython)
  n = 1
  ref = Ga_element
FEATURE [App::DocumentObjectGroupPython] As_element001  label="As_element : 1"  # scripted group (container) (typed FeaturePython)
  n = 1
  ref = As_element
FEATURE [App::DocumentObjectGroupPython] G4_GALLIUM_ARSENIDE  # scripted group (container) (typed FeaturePython)
  Dunit = g/cm3
  Dvalue = 5.31
  Group = -> [Ga_element001,As_element001]
  conduct = 2
  density = 1
  expand = 3
  formula = G4_GALLIUM_ARSENIDE
  name = G4_GALLIUM_ARSENIDE
  specific = 4
FEATURE [App::DocumentObjectGroupPython] H_element041  label="H_element : 0.081"  # scripted group (container) (typed FeaturePython)
  n = 0.08118
FEATURE [App::DocumentObjectGroupPython] C_element048  label="C_element : 0.416"  # scripted group (container) (typed FeaturePython)
  n = 0.41606
FEATURE [App::DocumentObjectGroupPython] N_element018  label="N_element : 0.111"  # scripted group (container) (typed FeaturePython)
  n = 0.11124
FEATURE [App::DocumentObjectGroupPython] O_element042  label="O_element : 0.381"  # scripted group (container) (typed FeaturePython)
  n = 0.38064
FEATURE [App::DocumentObjectGroupPython] S_element013  label="S_element : 0.011"  # scripted group (container) (typed FeaturePython)
  n = 0.01088
FEATURE [App::DocumentObjectGroupPython] G4_GEL_PHOTO_EMULSION  # scripted group (container) (typed FeaturePython)
  Dunit = g/cm3
  Dvalue = 1.2914
  Group = -> [H_element041,C_element048,N_element018,O_element042,S_element013]
  conduct = 2
  density = 1
  expand = 3
  formula = G4_GEL_PHOTO_EMULSION
  name = G4_GEL_PHOTO_EMULSION
  specific = 4
FEATURE [App::DocumentObjectGroupPython] B_element004  label="B_element : 0.040"  # scripted group (container) (typed FeaturePython)
  n = 0.0400639
FEATURE [App::DocumentObjectGroupPython] O_element043  label="O_element : 0.540"  # scripted group (container) (typed FeaturePython)
  n = 0.539561
FEATURE [App::DocumentObjectGroupPython] Na_element008  label="Na_element : 0.028"  # scripted group (container) (typed FeaturePython)
  n = 0.0281909
FEATURE [App::DocumentObjectGroupPython] Al_element003  label="Al_element : 0.012"  # scripted group (container) (typed FeaturePython)
  n = 0.011644
FEATURE [App::DocumentObjectGroupPython] Si_element003  label="Si_element : 0.377"  # scripted group (container) (typed FeaturePython)
  n = 0.377219
FEATURE [App::DocumentObjectGroupPython] K_element004  label="K_element : 0.014"  # scripted group (container) (typed FeaturePython)
  n = 0.00332099
FEATURE [App::DocumentObjectGroupPython] G4_Pyrex_Glass  # scripted group (container) (typed FeaturePython)
  Dunit = g/cm3
  Dvalue = 2.23
  Group = -> [B_element004,O_element043,Na_element008,Al_element003,Si_element003,K_element004]
  conduct = 2
  density = 1
  expand = 3
  formula = G4_Pyrex_Glass
  name = G4_Pyrex_Glass
  specific = 4
FEATURE [App::DocumentObjectGroupPython] O_element044  label="O_element : 0.156"  # scripted group (container) (typed FeaturePython)
  n = 0.156453
FEATURE [App::DocumentObjectGroupPython] Si_element004  label="Si_element : 0.081"  # scripted group (container) (typed FeaturePython)
  n = 0.080866
FEATURE [App::DocumentObjectGroupPython] Ti_element001  label="Ti_element : 0.008"  # scripted group (container) (typed FeaturePython)
  n = 0.008092
FEATURE [App::DocumentObjectGroupPython] As_element002  label="As_element : 0.003"  # scripted group (container) (typed FeaturePython)
  n = 0.002651
FEATURE [App::DocumentObjectGroupPython] Pb_element001  label="Pb_element : 0.752"  # scripted group (container) (typed FeaturePython)
  n = 0.751938
FEATURE [App::DocumentObjectGroupPython] G4_GLASS_LEAD  # scripted group (container) (typed FeaturePython)
  Dunit = g/cm3
  Dvalue = 6.22
  Group = -> [O_element044,Si_element004,Ti_element001,As_element002,Pb_element001]
  conduct = 2
  density = 1
  expand = 3
  formula = G4_GLASS_LEAD
  name = G4_GLASS_LEAD
  specific = 4
FEATURE [App::DocumentObjectGroupPython] O_element045  label="O_element : 0.460"  # scripted group (container) (typed FeaturePython)
  n = 0.4598
FEATURE [App::DocumentObjectGroupPython] Na_element009  label="Na_element : 0.096"  # scripted group (container) (typed FeaturePython)
  n = 0.0964411
FEATURE [App::DocumentObjectGroupPython] Si_element005  label="Si_element : 0.378"  # scripted group (container) (typed FeaturePython)
  n = 0.336553
FEATURE [App::DocumentObjectGroupPython] Ca_element011  label="Ca_element : 0.107"  # scripted group (container) (typed FeaturePython)
  n = 0.107205
FEATURE [App::DocumentObjectGroupPython] G4_GLASS_PLATE  # scripted group (container) (typed FeaturePython)
  Dunit = g/cm3
  Dvalue = 2.4
  Group = -> [O_element045,Na_element009,Si_element005,Ca_element011]
  conduct = 2
  density = 1
  expand = 3
  formula = G4_GLASS_PLATE
  name = G4_GLASS_PLATE
  specific = 4
FEATURE [App::DocumentObjectGroupPython] C_element049  label="C_element : 026"  # scripted group (container) (typed FeaturePython)
  n = 5
  ref = C_element
FEATURE [App::DocumentObjectGroupPython] H_element042  label="H_element : 021"  # scripted group (container) (typed FeaturePython)
  n = 10
  ref = H_element
FEATURE [App::DocumentObjectGroupPython] N_element019  label="N_element : 2"  # scripted group (container) (typed FeaturePython)
  n = 2
  ref = N_element
FEATURE [App::DocumentObjectGroupPython] O_element046  label="O_element : 022"  # scripted group (container) (typed FeaturePython)
  n = 3
  ref = O_element
FEATURE [App::DocumentObjectGroupPython] G4_GLUTAMINE  # scripted group (container) (typed FeaturePython)
  Dunit = g/cm3
  Dvalue = 1.46
  Group = -> [C_element049,H_element042,N_element019,O_element046]
  conduct = 2
  density = 1
  expand = 3
  formula = G4_GLUTAMINE
  name = G4_GLUTAMINE
  specific = 4
FEATURE [App::DocumentObjectGroupPython] C_element050  label="C_element : 027"  # scripted group (container) (typed FeaturePython)
  n = 3
  ref = C_element
FEATURE [App::DocumentObjectGroupPython] H_element043  label="H_element : 022"  # scripted group (container) (typed FeaturePython)
  n = 8
  ref = H_element
FEATURE [App::DocumentObjectGroupPython] O_element047  label="O_element : 023"  # scripted group (container) (typed FeaturePython)
  n = 3
  ref = O_element
FEATURE [App::DocumentObjectGroupPython] G4_GLYCEROL  # scripted group (container) (typed FeaturePython)
  Dunit = g/cm3
  Dvalue = 1.2613
  Group = -> [C_element050,H_element043,O_element047]
  conduct = 2
  density = 1
  expand = 3
  formula = G4_GLYCEROL
  name = G4_GLYCEROL
  specific = 4
FEATURE [App::DocumentObjectGroupPython] C_element051  label="C_element : 028"  # scripted group (container) (typed FeaturePython)
  n = 5
  ref = C_element
FEATURE [App::DocumentObjectGroupPython] H_element044  label="H_element : 023"  # scripted group (container) (typed FeaturePython)
  n = 5
  ref = H_element
FEATURE [App::DocumentObjectGroupPython] N_element020  label="N_element : 009"  # scripted group (container) (typed FeaturePython)
  n = 5
  ref = N_element
FEATURE [App::DocumentObjectGroupPython] O_element048  label="O_element : 024"  # scripted group (container) (typed FeaturePython)
  n = 1
  ref = O_element
FEATURE [App::DocumentObjectGroupPython] G4_GUANINE  # scripted group (container) (typed FeaturePython)
  Dunit = g/cm3
  Dvalue = 2.2
  Group = -> [C_element051,H_element044,N_element020,O_element048]
  conduct = 2
  density = 1
  expand = 3
  formula = G4_GUANINE
  name = G4_GUANINE
  specific = 4
FEATURE [App::DocumentObjectGroupPython] Ca_element012  label="Ca_element : 006"  # scripted group (container) (typed FeaturePython)
  n = 1
  ref = Ca_element
FEATURE [App::DocumentObjectGroupPython] S_element014  label="S_element : 005"  # scripted group (container) (typed FeaturePython)
  n = 1
  ref = S_element
FEATURE [App::DocumentObjectGroupPython] O_element049  label="O_element : 6"  # scripted group (container) (typed FeaturePython)
  n = 6
  ref = O_element
FEATURE [App::DocumentObjectGroupPython] H_element045  label="H_element : 024"  # scripted group (container) (typed FeaturePython)
  n = 4
  ref = H_element
FEATURE [App::DocumentObjectGroupPython] G4_GYPSUM  # scripted group (container) (typed FeaturePython)
  Dunit = g/cm3
  Dvalue = 2.32
  Group = -> [Ca_element012,S_element014,O_element049,H_element045]
  conduct = 2
  density = 1
  expand = 3
  formula = G4_GYPSUM
  name = G4_GYPSUM
  specific = 4
FEATURE [App::DocumentObjectGroupPython] C_element052  label="C_element : 7"  # scripted group (container) (typed FeaturePython)
  n = 7
  ref = C_element
FEATURE [App::DocumentObjectGroupPython] H_element046  label="H_element : 16"  # scripted group (container) (typed FeaturePython)
  n = 16
  ref = H_element
FEATURE [App::DocumentObjectGroupPython] G4_N_HEPTANE  label="G4_N-HEPTANE"  # scripted group (container) (typed FeaturePython)
  Dunit = g/cm3
  Dvalue = 0.68376
  Group = -> [C_element052,H_element046]
  conduct = 2
  density = 1
  expand = 3
  formula = G4_N-HEPTANE
  name = G4_N-HEPTANE
  specific = 4
FEATURE [App::DocumentObjectGroupPython] C_element053  label="C_element : 029"  # scripted group (container) (typed FeaturePython)
  n = 6
  ref = C_element
FEATURE [App::DocumentObjectGroupPython] H_element047  label="H_element : 14"  # scripted group (container) (typed FeaturePython)
  n = 14
  ref = H_element
FEATURE [App::DocumentObjectGroupPython] G4_N_HEXANE  label="G4_N-HEXANE"  # scripted group (container) (typed FeaturePython)
  Dunit = g/cm3
  Dvalue = 0.6603
  Group = -> [C_element053,H_element047]
  conduct = 2
  density = 1
  expand = 3
  formula = G4_N-HEXANE
  name = G4_N-HEXANE
  specific = 4
FEATURE [App::DocumentObjectGroupPython] C_element054  label="C_element : 22"  # scripted group (container) (typed FeaturePython)
  n = 22
  ref = C_element
FEATURE [App::DocumentObjectGroupPython] H_element048  label="H_element : 025"  # scripted group (container) (typed FeaturePython)
  n = 10
  ref = H_element
FEATURE [App::DocumentObjectGroupPython] N_element021  label="N_element : 010"  # scripted group (container) (typed FeaturePython)
  n = 2
  ref = N_element
FEATURE [App::DocumentObjectGroupPython] O_element050  label="O_element : 025"  # scripted group (container) (typed FeaturePython)
  n = 5
  ref = O_element
FEATURE [App::DocumentObjectGroupPython] G4_KAPTON  # scripted group (container) (typed FeaturePython)
  Dunit = g/cm3
  Dvalue = 1.42
  Group = -> [C_element054,H_element048,N_element021,O_element050]
  conduct = 2
  density = 1
  expand = 3
  formula = G4_KAPTON
  name = G4_KAPTON
  specific = 4
FEATURE [App::DocumentObjectGroupPython] La_element001  label="La_element : 1"  # scripted group (container) (typed FeaturePython)
  n = 1
  ref = La_element
FEATURE [App::DocumentObjectGroupPython] Br_element003  label="Br_element : 002"  # scripted group (container) (typed FeaturePython)
  n = 1
  ref = Br_element
FEATURE [App::DocumentObjectGroupPython] O_element051  label="O_element : 026"  # scripted group (container) (typed FeaturePython)
  n = 1
  ref = O_element
FEATURE [App::DocumentObjectGroupPython] G4_LANTHANUM_OXYBROMIDE  # scripted group (container) (typed FeaturePython)
  Dunit = g/cm3
  Dvalue = 6.28
  Group = -> [La_element001,Br_element003,O_element051]
  conduct = 2
  density = 1
  expand = 3
  formula = G4_LANTHANUM_OXYBROMIDE
  name = G4_LANTHANUM_OXYBROMIDE
  specific = 4
FEATURE [App::DocumentObjectGroupPython] La_element002  label="La_element : 2"  # scripted group (container) (typed FeaturePython)
  n = 2
  ref = La_element
FEATURE [App::DocumentObjectGroupPython] O_element052  label="O_element : 027"  # scripted group (container) (typed FeaturePython)
  n = 2
  ref = O_element
FEATURE [App::DocumentObjectGroupPython] S_element015  label="S_element : 006"  # scripted group (container) (typed FeaturePython)
  n = 1
  ref = S_element
FEATURE [App::DocumentObjectGroupPython] G4_LANTHANUM_OXYSULFIDE  # scripted group (container) (typed FeaturePython)
  Dunit = g/cm3
  Dvalue = 5.86
  Group = -> [La_element002,O_element052,S_element015]
  conduct = 2
  density = 1
  expand = 3
  formula = G4_LANTHANUM_OXYSULFIDE
  name = G4_LANTHANUM_OXYSULFIDE
  specific = 4
FEATURE [App::DocumentObjectGroupPython] O_element053  label="O_element : 0.072"  # scripted group (container) (typed FeaturePython)
  n = 0.071682
FEATURE [App::DocumentObjectGroupPython] Pb_element002  label="Pb_element : 0.928"  # scripted group (container) (typed FeaturePython)
  n = 0.928318
FEATURE [App::DocumentObjectGroupPython] G4_LEAD_OXIDE  # scripted group (container) (typed FeaturePython)
  Dunit = g/cm3
  Dvalue = 9.53
  Group = -> [O_element053,Pb_element002]
  conduct = 2
  density = 1
  expand = 3
  formula = G4_LEAD_OXIDE
  name = G4_LEAD_OXIDE
  specific = 4
FEATURE [App::DocumentObjectGroupPython] Li_element001  label="Li_element : 1"  # scripted group (container) (typed FeaturePython)
  n = 1
  ref = Li_element
FEATURE [App::DocumentObjectGroupPython] N_element022  label="N_element : 011"  # scripted group (container) (typed FeaturePython)
  n = 1
  ref = N_element
FEATURE [App::DocumentObjectGroupPython] H_element049  label="H_element : 026"  # scripted group (container) (typed FeaturePython)
  n = 2
  ref = H_element
FEATURE [App::DocumentObjectGroupPython] G4_LITHIUM_AMIDE  # scripted group (container) (typed FeaturePython)
  Dunit = g/cm3
  Dvalue = 1.178
  Group = -> [Li_element001,N_element022,H_element049]
  conduct = 2
  density = 1
  expand = 3
  formula = G4_LITHIUM_AMIDE
  name = G4_LITHIUM_AMIDE
  specific = 4
FEATURE [App::DocumentObjectGroupPython] Li_element002  label="Li_element : 2"  # scripted group (container) (typed FeaturePython)
  n = 2
  ref = Li_element
FEATURE [App::DocumentObjectGroupPython] C_element055  label="C_element : 030"  # scripted group (container) (typed FeaturePython)
  n = 1
  ref = C_element
FEATURE [App::DocumentObjectGroupPython] O_element054  label="O_element : 028"  # scripted group (container) (typed FeaturePython)
  n = 3
  ref = O_element
FEATURE [App::DocumentObjectGroupPython] G4_LITHIUM_CARBONATE  # scripted group (container) (typed FeaturePython)
  Dunit = g/cm3
  Dvalue = 2.11
  Group = -> [Li_element002,C_element055,O_element054]
  conduct = 2
  density = 1
  expand = 3
  formula = G4_LITHIUM_CARBONATE
  name = G4_LITHIUM_CARBONATE
  specific = 4
FEATURE [App::DocumentObjectGroupPython] Li_element003  label="Li_element : 003"  # scripted group (container) (typed FeaturePython)
  n = 1
  ref = Li_element
FEATURE [App::DocumentObjectGroupPython] F_element012  label="F_element : 004"  # scripted group (container) (typed FeaturePython)
  n = 1
  ref = F_element
FEATURE [App::DocumentObjectGroupPython] G4_LITHIUM_FLUORIDE  # scripted group (container) (typed FeaturePython)
  Dunit = g/cm3
  Dvalue = 2.635
  Group = -> [Li_element003,F_element012]
  conduct = 2
  density = 1
  expand = 3
  formula = G4_LITHIUM_FLUORIDE
  name = G4_LITHIUM_FLUORIDE
  specific = 4
FEATURE [App::DocumentObjectGroupPython] Li_element004  label="Li_element : 004"  # scripted group (container) (typed FeaturePython)
  n = 1
  ref = Li_element
FEATURE [App::DocumentObjectGroupPython] H_element050  label="H_element : 027"  # scripted group (container) (typed FeaturePython)
  n = 1
  ref = H_element
FEATURE [App::DocumentObjectGroupPython] G4_LITHIUM_HYDRIDE  # scripted group (container) (typed FeaturePython)
  Dunit = g/cm3
  Dvalue = 0.82
  Group = -> [Li_element004,H_element050]
  conduct = 2
  density = 1
  expand = 3
  formula = G4_LITHIUM_HYDRIDE
  name = G4_LITHIUM_HYDRIDE
  specific = 4
FEATURE [App::DocumentObjectGroupPython] Li_element005  label="Li_element : 005"  # scripted group (container) (typed FeaturePython)
  n = 1
  ref = Li_element
FEATURE [App::DocumentObjectGroupPython] I_element003  label="I_element : 002"  # scripted group (container) (typed FeaturePython)
  n = 1
  ref = I_element
FEATURE [App::DocumentObjectGroupPython] G4_LITHIUM_IODIDE  # scripted group (container) (typed FeaturePython)
  Dunit = g/cm3
  Dvalue = 3.494
  Group = -> [Li_element005,I_element003]
  conduct = 2
  density = 1
  expand = 3
  formula = G4_LITHIUM_IODIDE
  name = G4_LITHIUM_IODIDE
  specific = 4
FEATURE [App::DocumentObjectGroupPython] Li_element006  label="Li_element : 006"  # scripted group (container) (typed FeaturePython)
  n = 2
  ref = Li_element
FEATURE [App::DocumentObjectGroupPython] O_element055  label="O_element : 029"  # scripted group (container) (typed FeaturePython)
  n = 1
  ref = O_element
FEATURE [App::DocumentObjectGroupPython] G4_LITHIUM_OXIDE  # scripted group (container) (typed FeaturePython)
  Dunit = g/cm3
  Dvalue = 2.013
  Group = -> [Li_element006,O_element055]
  conduct = 2
  density = 1
  expand = 3
  formula = G4_LITHIUM_OXIDE
  name = G4_LITHIUM_OXIDE
  specific = 4
FEATURE [App::DocumentObjectGroupPython] Li_element007  label="Li_element : 007"  # scripted group (container) (typed FeaturePython)
  n = 2
  ref = Li_element
FEATURE [App::DocumentObjectGroupPython] B_element005  label="B_element : 005"  # scripted group (container) (typed FeaturePython)
  n = 4
  ref = B_element
FEATURE [App::DocumentObjectGroupPython] O_element056  label="O_element : 7"  # scripted group (container) (typed FeaturePython)
  n = 7
  ref = O_element
FEATURE [App::DocumentObjectGroupPython] G4_LITHIUM_TETRABORATE  # scripted group (container) (typed FeaturePython)
  Dunit = g/cm3
  Dvalue = 2.44
  Group = -> [Li_element007,B_element005,O_element056]
  conduct = 2
  density = 1
  expand = 3
  formula = G4_LITHIUM_TETRABORATE
  name = G4_LITHIUM_TETRABORATE
  specific = 4
FEATURE [App::DocumentObjectGroupPython] H_element051  label="H_element : 0.105"  # scripted group (container) (typed FeaturePython)
  n = 0.105
FEATURE [App::DocumentObjectGroupPython] C_element056  label="C_element : 0.083"  # scripted group (container) (typed FeaturePython)
  n = 0.083
FEATURE [App::DocumentObjectGroupPython] N_element023  label="N_element : 0.023"  # scripted group (container) (typed FeaturePython)
  n = 0.023
FEATURE [App::DocumentObjectGroupPython] O_element057  label="O_element : 0.779"  # scripted group (container) (typed FeaturePython)
  n = 0.779
FEATURE [App::DocumentObjectGroupPython] Na_element010  label="Na_element : 0.097"  # scripted group (container) (typed FeaturePython)
  n = 0.002
FEATURE [App::DocumentObjectGroupPython] P_element006  label="P_element : 0.105"  # scripted group (container) (typed FeaturePython)
  n = 0.001
FEATURE [App::DocumentObjectGroupPython] S_element016  label="S_element : 0.017"  # scripted group (container) (typed FeaturePython)
  n = 0.002
FEATURE [App::DocumentObjectGroupPython] Cl_element014  label="Cl_element : 0.587"  # scripted group (container) (typed FeaturePython)
  n = 0.003
FEATURE [App::DocumentObjectGroupPython] K_element005  label="K_element : 0.015"  # scripted group (container) (typed FeaturePython)
  n = 0.002
FEATURE [App::DocumentObjectGroupPython] G4_LUNG_ICRP  # scripted group (container) (typed FeaturePython)
  Dunit = g/cm3
  Dvalue = 1.04
  Group = -> [H_element051,C_element056,N_element023,O_element057,Na_element010,P_element006,S_element016,Cl_element014,K_element005]
  conduct = 2
  density = 1
  expand = 3
  formula = G4_LUNG_ICRP
  name = G4_LUNG_ICRP
  specific = 4
FEATURE [App::DocumentObjectGroupPython] H_element052  label="H_element : 0.116"  # scripted group (container) (typed FeaturePython)
  n = 0.114318
FEATURE [App::DocumentObjectGroupPython] C_element057  label="C_element : 0.656"  # scripted group (container) (typed FeaturePython)
  n = 0.655824
FEATURE [App::DocumentObjectGroupPython] O_element058  label="O_element : 0.092"  # scripted group (container) (typed FeaturePython)
  n = 0.0921831
FEATURE [App::DocumentObjectGroupPython] Mg_element004  label="Mg_element : 0.135"  # scripted group (container) (typed FeaturePython)
  n = 0.134792
FEATURE [App::DocumentObjectGroupPython] Ca_element013  label="Ca_element : 0.003"  # scripted group (container) (typed FeaturePython)
  n = 0.002883
FEATURE [App::DocumentObjectGroupPython] G4_M3_WAX  # scripted group (container) (typed FeaturePython)
  Dunit = g/cm3
  Dvalue = 1.05
  Group = -> [H_element052,C_element057,O_element058,Mg_element004,Ca_element013]
  conduct = 2
  density = 1
  expand = 3
  formula = G4_M3_WAX
  name = G4_M3_WAX
  specific = 4
FEATURE [App::DocumentObjectGroupPython] Mg_element005  label="Mg_element : 1"  # scripted group (container) (typed FeaturePython)
  n = 1
  ref = Mg_element
FEATURE [App::DocumentObjectGroupPython] C_element058  label="C_element : 031"  # scripted group (container) (typed FeaturePython)
  n = 1
  ref = C_element
FEATURE [App::DocumentObjectGroupPython] O_element059  label="O_element : 030"  # scripted group (container) (typed FeaturePython)
  n = 3
  ref = O_element
FEATURE [App::DocumentObjectGroupPython] G4_MAGNESIUM_CARBONATE  # scripted group (container) (typed FeaturePython)
  Dunit = g/cm3
  Dvalue = 2.958
  Group = -> [Mg_element005,C_element058,O_element059]
  conduct = 2
  density = 1
  expand = 3
  formula = G4_MAGNESIUM_CARBONATE
  name = G4_MAGNESIUM_CARBONATE
  specific = 4
FEATURE [App::DocumentObjectGroupPython] Mg_element006  label="Mg_element : 002"  # scripted group (container) (typed FeaturePython)
  n = 1
  ref = Mg_element
FEATURE [App::DocumentObjectGroupPython] F_element013  label="F_element : 005"  # scripted group (container) (typed FeaturePython)
  n = 2
  ref = F_element
FEATURE [App::DocumentObjectGroupPython] G4_MAGNESIUM_FLUORIDE  # scripted group (container) (typed FeaturePython)
  Dunit = g/cm3
  Dvalue = 3
  Group = -> [Mg_element006,F_element013]
  conduct = 2
  density = 1
  expand = 3
  formula = G4_MAGNESIUM_FLUORIDE
  name = G4_MAGNESIUM_FLUORIDE
  specific = 4
FEATURE [App::DocumentObjectGroupPython] Mg_element007  label="Mg_element : 003"  # scripted group (container) (typed FeaturePython)
  n = 1
  ref = Mg_element
FEATURE [App::DocumentObjectGroupPython] O_element060  label="O_element : 031"  # scripted group (container) (typed FeaturePython)
  n = 1
  ref = O_element
FEATURE [App::DocumentObjectGroupPython] G4_MAGNESIUM_OXIDE  # scripted group (container) (typed FeaturePython)
  Dunit = g/cm3
  Dvalue = 3.58
  Group = -> [Mg_element007,O_element060]
  conduct = 2
  density = 1
  expand = 3
  formula = G4_MAGNESIUM_OXIDE
  name = G4_MAGNESIUM_OXIDE
  specific = 4
FEATURE [App::DocumentObjectGroupPython] Mg_element008  label="Mg_element : 004"  # scripted group (container) (typed FeaturePython)
  n = 1
  ref = Mg_element
FEATURE [App::DocumentObjectGroupPython] B_element006  label="B_element : 006"  # scripted group (container) (typed FeaturePython)
  n = 4
  ref = B_element
FEATURE [App::DocumentObjectGroupPython] O_element061  label="O_element : 032"  # scripted group (container) (typed FeaturePython)
  n = 7
  ref = O_element
FEATURE [App::DocumentObjectGroupPython] G4_MAGNESIUM_TETRABORATE  # scripted group (container) (typed FeaturePython)
  Dunit = g/cm3
  Dvalue = 2.53
  Group = -> [Mg_element008,B_element006,O_element061]
  conduct = 2
  density = 1
  expand = 3
  formula = G4_MAGNESIUM_TETRABORATE
  name = G4_MAGNESIUM_TETRABORATE
  specific = 4
FEATURE [App::DocumentObjectGroupPython] Hg_element001  label="Hg_element : 1"  # scripted group (container) (typed FeaturePython)
  n = 1
  ref = Hg_element
FEATURE [App::DocumentObjectGroupPython] I_element004  label="I_element : 2"  # scripted group (container) (typed FeaturePython)
  n = 2
  ref = I_element
FEATURE [App::DocumentObjectGroupPython] G4_MERCURIC_IODIDE  # scripted group (container) (typed FeaturePython)
  Dunit = g/cm3
  Dvalue = 6.36
  Group = -> [Hg_element001,I_element004]
  conduct = 2
  density = 1
  expand = 3
  formula = G4_MERCURIC_IODIDE
  name = G4_MERCURIC_IODIDE
  specific = 4
FEATURE [App::DocumentObjectGroupPython] C_element059  label="C_element : 032"  # scripted group (container) (typed FeaturePython)
  n = 1
  ref = C_element
FEATURE [App::DocumentObjectGroupPython] H_element053  label="H_element : 028"  # scripted group (container) (typed FeaturePython)
  n = 4
  ref = H_element
FEATURE [App::DocumentObjectGroupPython] G4_METHANE  # scripted group (container) (typed FeaturePython)
  Dunit = g/cm3
  Dvalue = 0.000667151
  Group = -> [C_element059,H_element053]
  conduct = 2
  density = 1
  expand = 3
  formula = G4_METHANE
  name = G4_METHANE
  specific = 4
FEATURE [App::DocumentObjectGroupPython] C_element060  label="C_element : 033"  # scripted group (container) (typed FeaturePython)
  n = 1
  ref = C_element
FEATURE [App::DocumentObjectGroupPython] H_element054  label="H_element : 029"  # scripted group (container) (typed FeaturePython)
  n = 4
  ref = H_element
FEATURE [App::DocumentObjectGroupPython] O_element062  label="O_element : 033"  # scripted group (container) (typed FeaturePython)
  n = 1
  ref = O_element
FEATURE [App::DocumentObjectGroupPython] G4_METHANOL  # scripted group (container) (typed FeaturePython)
  Dunit = g/cm3
  Dvalue = 0.7914
  Group = -> [C_element060,H_element054,O_element062]
  conduct = 2
  density = 1
  expand = 3
  formula = G4_METHANOL
  name = G4_METHANOL
  specific = 4
FEATURE [App::DocumentObjectGroupPython] H_element055  label="H_element : 0.134"  # scripted group (container) (typed FeaturePython)
  n = 0.13404
FEATURE [App::DocumentObjectGroupPython] C_element061  label="C_element : 0.778"  # scripted group (container) (typed FeaturePython)
  n = 0.77796
FEATURE [App::DocumentObjectGroupPython] O_element063  label="O_element : 0.035"  # scripted group (container) (typed FeaturePython)
  n = 0.03502
FEATURE [App::DocumentObjectGroupPython] Mg_element009  label="Mg_element : 0.039"  # scripted group (container) (typed FeaturePython)
  n = 0.038594
FEATURE [App::DocumentObjectGroupPython] Ti_element002  label="Ti_element : 0.014"  # scripted group (container) (typed FeaturePython)
  n = 0.014386
FEATURE [App::DocumentObjectGroupPython] G4_MIX_D_WAX  # scripted group (container) (typed FeaturePython)
  Dunit = g/cm3
  Dvalue = 0.99
  Group = -> [H_element055,C_element061,O_element063,Mg_element009,Ti_element002]
  conduct = 2
  density = 1
  expand = 3
  formula = G4_MIX_D_WAX
  name = G4_MIX_D_WAX
  specific = 4
FEATURE [App::DocumentObjectGroupPython] H_element056  label="H_element : 0.135"  # scripted group (container) (typed FeaturePython)
  n = 0.081192
FEATURE [App::DocumentObjectGroupPython] C_element062  label="C_element : 0.583"  # scripted group (container) (typed FeaturePython)
  n = 0.583442
FEATURE [App::DocumentObjectGroupPython] N_element024  label="N_element : 0.018"  # scripted group (container) (typed FeaturePython)
  n = 0.017798
FEATURE [App::DocumentObjectGroupPython] O_element064  label="O_element : 0.186"  # scripted group (container) (typed FeaturePython)
  n = 0.186381
FEATURE [App::DocumentObjectGroupPython] Mg_element010  label="Mg_element : 0.130"  # scripted group (container) (typed FeaturePython)
  n = 0.130287
FEATURE [App::DocumentObjectGroupPython] Cl_element015  label="Cl_element : 0.588"  # scripted group (container) (typed FeaturePython)
  n = 0.0009
FEATURE [App::DocumentObjectGroupPython] G4_MS20_TISSUE  # scripted group (container) (typed FeaturePython)
  Dunit = g/cm3
  Dvalue = 1
  Group = -> [H_element056,C_element062,N_element024,O_element064,Mg_element010,Cl_element015]
  conduct = 2
  density = 1
  expand = 3
  formula = G4_MS20_TISSUE
  name = G4_MS20_TISSUE
  specific = 4
FEATURE [App::DocumentObjectGroupPython] H_element057  label="H_element : 0.136"  # scripted group (container) (typed FeaturePython)
  n = 0.102
FEATURE [App::DocumentObjectGroupPython] C_element063  label="C_element : 0.143"  # scripted group (container) (typed FeaturePython)
  n = 0.143
FEATURE [App::DocumentObjectGroupPython] N_element025  label="N_element : 0.034"  # scripted group (container) (typed FeaturePython)
  n = 0.034
FEATURE [App::DocumentObjectGroupPython] O_element065  label="O_element : 0.710"  # scripted group (container) (typed FeaturePython)
  n = 0.71
FEATURE [App::DocumentObjectGroupPython] Na_element011  label="Na_element : 0.098"  # scripted group (container) (typed FeaturePython)
  n = 0.001
FEATURE [App::DocumentObjectGroupPython] P_element007  label="P_element : 0.002"  # scripted group (container) (typed FeaturePython)
  n = 0.002
FEATURE [App::DocumentObjectGroupPython] S_element017  label="S_element : 0.018"  # scripted group (container) (typed FeaturePython)
  n = 0.003
FEATURE [App::DocumentObjectGroupPython] Cl_element016  label="Cl_element : 0.589"  # scripted group (container) (typed FeaturePython)
  n = 0.001
FEATURE [App::DocumentObjectGroupPython] K_element006  label="K_element : 0.004"  # scripted group (container) (typed FeaturePython)
  n = 0.004
FEATURE [App::DocumentObjectGroupPython] G4_MUSCLE_SKELETAL_ICRP  # scripted group (container) (typed FeaturePython)
  Dunit = g/cm3
  Dvalue = 1.05
  Group = -> [H_element057,C_element063,N_element025,O_element065,Na_element011,P_element007,S_element017,Cl_element016,K_element006]
  conduct = 2
  density = 1
  expand = 3
  formula = G4_MUSCLE_SKELETAL_ICRP
  name = G4_MUSCLE_SKELETAL_ICRP
  specific = 4
FEATURE [App::DocumentObjectGroupPython] H_element058  label="H_element : 0.137"  # scripted group (container) (typed FeaturePython)
  n = 0.102102
FEATURE [App::DocumentObjectGroupPython] C_element064  label="C_element : 0.123"  # scripted group (container) (typed FeaturePython)
  n = 0.123123
FEATURE [App::DocumentObjectGroupPython] N_element026  label="N_element : 0.756"  # scripted group (container) (typed FeaturePython)
  n = 0.035035
FEATURE [App::DocumentObjectGroupPython] O_element066  label="O_element : 0.730"  # scripted group (container) (typed FeaturePython)
  n = 0.72973
FEATURE [App::DocumentObjectGroupPython] Na_element012  label="Na_element : 0.099"  # scripted group (container) (typed FeaturePython)
  n = 0.001001
FEATURE [App::DocumentObjectGroupPython] P_element008  label="P_element : 0.106"  # scripted group (container) (typed FeaturePython)
  n = 0.002002
FEATURE [App::DocumentObjectGroupPython] S_element018  label="S_element : 0.019"  # scripted group (container) (typed FeaturePython)
  n = 0.004004
FEATURE [App::DocumentObjectGroupPython] K_element007  label="K_element : 0.016"  # scripted group (container) (typed FeaturePython)
  n = 0.003003
FEATURE [App::DocumentObjectGroupPython] G4_MUSCLE_STRIATED_ICRU  # scripted group (container) (typed FeaturePython)
  Dunit = g/cm3
  Dvalue = 1.04
  Group = -> [H_element058,C_element064,N_element026,O_element066,Na_element012,P_element008,S_element018,K_element007]
  conduct = 2
  density = 1
  expand = 3
  formula = G4_MUSCLE_STRIATED_ICRU
  name = G4_MUSCLE_STRIATED_ICRU
  specific = 4
FEATURE [App::DocumentObjectGroupPython] H_element059  label="H_element : 0.098"  # scripted group (container) (typed FeaturePython)
  n = 0.0982341
FEATURE [App::DocumentObjectGroupPython] C_element065  label="C_element : 0.156"  # scripted group (container) (typed FeaturePython)
  n = 0.156214
FEATURE [App::DocumentObjectGroupPython] N_element027  label="N_element : 0.757"  # scripted group (container) (typed FeaturePython)
  n = 0.035451
FEATURE [App::DocumentObjectGroupPython] O_element067  label="O_element : 0.880"  # scripted group (container) (typed FeaturePython)
  n = 0.710101
FEATURE [App::DocumentObjectGroupPython] G4_MUSCLE_WITH_SUCROSE  # scripted group (container) (typed FeaturePython)
  Dunit = g/cm3
  Dvalue = 1.11
  Group = -> [H_element059,C_element065,N_element027,O_element067]
  conduct = 2
  density = 1
  expand = 3
  formula = G4_MUSCLE_WITH_SUCROSE
  name = G4_MUSCLE_WITH_SUCROSE
  specific = 4
FEATURE [App::DocumentObjectGroupPython] H_element060  label="H_element : 0.138"  # scripted group (container) (typed FeaturePython)
  n = 0.101969
FEATURE [App::DocumentObjectGroupPython] C_element066  label="C_element : 0.120"  # scripted group (container) (typed FeaturePython)
  n = 0.120058
FEATURE [App::DocumentObjectGroupPython] N_element028  label="N_element : 0.758"  # scripted group (container) (typed FeaturePython)
  n = 0.035451
FEATURE [App::DocumentObjectGroupPython] O_element068  label="O_element : 0.743"  # scripted group (container) (typed FeaturePython)
  n = 0.742522
FEATURE [App::DocumentObjectGroupPython] G4_MUSCLE_WITHOUT_SUCROSE  # scripted group (container) (typed FeaturePython)
  Dunit = g/cm3
  Dvalue = 1.07
  Group = -> [H_element060,C_element066,N_element028,O_element068]
  conduct = 2
  density = 1
  expand = 3
  formula = G4_MUSCLE_WITHOUT_SUCROSE
  name = G4_MUSCLE_WITHOUT_SUCROSE
  specific = 4
FEATURE [App::DocumentObjectGroupPython] C_element067  label="C_element : 10"  # scripted group (container) (typed FeaturePython)
  n = 10
  ref = C_element
FEATURE [App::DocumentObjectGroupPython] H_element061  label="H_element : 030"  # scripted group (container) (typed FeaturePython)
  n = 8
  ref = H_element
FEATURE [App::DocumentObjectGroupPython] G4_NAPHTHALENE  # scripted group (container) (typed FeaturePython)
  Dunit = g/cm3
  Dvalue = 1.145
  Group = -> [C_element067,H_element061]
  conduct = 2
  density = 1
  expand = 3
  formula = G4_NAPHTHALENE
  name = G4_NAPHTHALENE
  specific = 4
FEATURE [App::DocumentObjectGroupPython] C_element068  label="C_element : 034"  # scripted group (container) (typed FeaturePython)
  n = 6
  ref = C_element
FEATURE [App::DocumentObjectGroupPython] H_element062  label="H_element : 031"  # scripted group (container) (typed FeaturePython)
  n = 5
  ref = H_element
FEATURE [App::DocumentObjectGroupPython] N_element029  label="N_element : 012"  # scripted group (container) (typed FeaturePython)
  n = 1
  ref = N_element
FEATURE [App::DocumentObjectGroupPython] O_element069  label="O_element : 034"  # scripted group (container) (typed FeaturePython)
  n = 2
  ref = O_element
FEATURE [App::DocumentObjectGroupPython] G4_NITROBENZENE  # scripted group (container) (typed FeaturePython)
  Dunit = g/cm3
  Dvalue = 1.19867
  Group = -> [C_element068,H_element062,N_element029,O_element069]
  conduct = 2
  density = 1
  expand = 3
  formula = G4_NITROBENZENE
  name = G4_NITROBENZENE
  specific = 4
FEATURE [App::DocumentObjectGroupPython] N_element030  label="N_element : 013"  # scripted group (container) (typed FeaturePython)
  n = 2
  ref = N_element
FEATURE [App::DocumentObjectGroupPython] O_element070  label="O_element : 035"  # scripted group (container) (typed FeaturePython)
  n = 1
  ref = O_element
FEATURE [App::DocumentObjectGroupPython] G4_NITROUS_OXIDE  # scripted group (container) (typed FeaturePython)
  Dunit = g/cm3
  Dvalue = 0.00183094
  Group = -> [N_element030,O_element070]
  conduct = 2
  density = 1
  expand = 3
  formula = G4_NITROUS_OXIDE
  name = G4_NITROUS_OXIDE
  specific = 4
FEATURE [App::DocumentObjectGroupPython] H_element063  label="H_element : 0.104"  # scripted group (container) (typed FeaturePython)
  n = 0.103509
FEATURE [App::DocumentObjectGroupPython] C_element069  label="C_element : 0.648"  # scripted group (container) (typed FeaturePython)
  n = 0.648416
FEATURE [App::DocumentObjectGroupPython] N_element031  label="N_element : 0.100"  # scripted group (container) (typed FeaturePython)
  n = 0.0995361
FEATURE [App::DocumentObjectGroupPython] O_element071  label="O_element : 0.149"  # scripted group (container) (typed FeaturePython)
  n = 0.148539
FEATURE [App::DocumentObjectGroupPython] G4_NYLON_8062  label="G4_NYLON-8062"  # scripted group (container) (typed FeaturePython)
  Dunit = g/cm3
  Dvalue = 1.08
  Group = -> [H_element063,C_element069,N_element031,O_element071]
  conduct = 2
  density = 1
  expand = 3
  formula = G4_NYLON-8062
  name = G4_NYLON-8062
  specific = 4
FEATURE [App::DocumentObjectGroupPython] C_element070  label="C_element : 035"  # scripted group (container) (typed FeaturePython)
  n = 6
  ref = C_element
FEATURE [App::DocumentObjectGroupPython] H_element064  label="H_element : 11"  # scripted group (container) (typed FeaturePython)
  n = 11
  ref = H_element
FEATURE [App::DocumentObjectGroupPython] N_element032  label="N_element : 014"  # scripted group (container) (typed FeaturePython)
  n = 1
  ref = N_element
FEATURE [App::DocumentObjectGroupPython] O_element072  label="O_element : 036"  # scripted group (container) (typed FeaturePython)
  n = 1
  ref = O_element
FEATURE [App::DocumentObjectGroupPython] G4_NYLON_6_6  label="G4_NYLON-6-6"  # scripted group (container) (typed FeaturePython)
  Dunit = g/cm3
  Dvalue = 1.14
  Group = -> [C_element070,H_element064,N_element032,O_element072]
  conduct = 2
  density = 1
  expand = 3
  formula = G4_NYLON-6-6
  name = G4_NYLON-6-6
  specific = 4
FEATURE [App::DocumentObjectGroupPython] H_element065  label="H_element : 0.139"  # scripted group (container) (typed FeaturePython)
  n = 0.107062
FEATURE [App::DocumentObjectGroupPython] C_element071  label="C_element : 0.680"  # scripted group (container) (typed FeaturePython)
  n = 0.680449
FEATURE [App::DocumentObjectGroupPython] N_element033  label="N_element : 0.099"  # scripted group (container) (typed FeaturePython)
  n = 0.099189
FEATURE [App::DocumentObjectGroupPython] O_element073  label="O_element : 0.113"  # scripted group (container) (typed FeaturePython)
  n = 0.1133
FEATURE [App::DocumentObjectGroupPython] G4_NYLON_6_10  label="G4_NYLON-6-10"  # scripted group (container) (typed FeaturePython)
  Dunit = g/cm3
  Dvalue = 1.14
  Group = -> [H_element065,C_element071,N_element033,O_element073]
  conduct = 2
  density = 1
  expand = 3
  formula = G4_NYLON-6-10
  name = G4_NYLON-6-10
  specific = 4
FEATURE [App::DocumentObjectGroupPython] H_element066  label="H_element : 0.140"  # scripted group (container) (typed FeaturePython)
  n = 0.115476
FEATURE [App::DocumentObjectGroupPython] C_element072  label="C_element : 0.721"  # scripted group (container) (typed FeaturePython)
  n = 0.720818
FEATURE [App::DocumentObjectGroupPython] N_element034  label="N_element : 0.076"  # scripted group (container) (typed FeaturePython)
  n = 0.0764169
FEATURE [App::DocumentObjectGroupPython] O_element074  label="O_element : 0.087"  # scripted group (container) (typed FeaturePython)
  n = 0.0872889
FEATURE [App::DocumentObjectGroupPython] G4_NYLON_11_RILSAN  label="G4_NYLON-11_RILSAN"  # scripted group (container) (typed FeaturePython)
  Dunit = g/cm3
  Dvalue = 1.425
  Group = -> [H_element066,C_element072,N_element034,O_element074]
  conduct = 2
  density = 1
  expand = 3
  formula = G4_NYLON-11_RILSAN
  name = G4_NYLON-11_RILSAN
  specific = 4
FEATURE [App::DocumentObjectGroupPython] C_element073  label="C_element : 8"  # scripted group (container) (typed FeaturePython)
  n = 8
  ref = C_element
FEATURE [App::DocumentObjectGroupPython] H_element067  label="H_element : 18"  # scripted group (container) (typed FeaturePython)
  n = 18
  ref = H_element
FEATURE [App::DocumentObjectGroupPython] G4_OCTANE  # scripted group (container) (typed FeaturePython)
  Dunit = g/cm3
  Dvalue = 0.7026
  Group = -> [C_element073,H_element067]
  conduct = 2
  density = 1
  expand = 3
  formula = G4_OCTANE
  name = G4_OCTANE
  specific = 4
FEATURE [App::DocumentObjectGroupPython] C_element074  label="C_element : 25"  # scripted group (container) (typed FeaturePython)
  n = 25
  ref = C_element
FEATURE [App::DocumentObjectGroupPython] H_element068  label="H_element : 52"  # scripted group (container) (typed FeaturePython)
  n = 52
  ref = H_element
FEATURE [App::DocumentObjectGroupPython] G4_PARAFFIN  # scripted group (container) (typed FeaturePython)
  Dunit = g/cm3
  Dvalue = 0.93
  Group = -> [C_element074,H_element068]
  conduct = 2
  density = 1
  expand = 3
  formula = G4_PARAFFIN
  name = G4_PARAFFIN
  specific = 4
FEATURE [App::DocumentObjectGroupPython] C_element075  label="C_element : 036"  # scripted group (container) (typed FeaturePython)
  n = 5
  ref = C_element
FEATURE [App::DocumentObjectGroupPython] H_element069  label="H_element : 032"  # scripted group (container) (typed FeaturePython)
  n = 12
  ref = H_element
FEATURE [App::DocumentObjectGroupPython] G4_N_PENTANE  label="G4_N-PENTANE"  # scripted group (container) (typed FeaturePython)
  Dunit = g/cm3
  Dvalue = 0.6262
  Group = -> [C_element075,H_element069]
  conduct = 2
  density = 1
  expand = 3
  formula = G4_N-PENTANE
  name = G4_N-PENTANE
  specific = 4
FEATURE [App::DocumentObjectGroupPython] H_element070  label="H_element : 0.014"  # scripted group (container) (typed FeaturePython)
  n = 0.0141
FEATURE [App::DocumentObjectGroupPython] C_element076  label="C_element : 0.072"  # scripted group (container) (typed FeaturePython)
  n = 0.072261
FEATURE [App::DocumentObjectGroupPython] N_element035  label="N_element : 0.019"  # scripted group (container) (typed FeaturePython)
  n = 0.01932
FEATURE [App::DocumentObjectGroupPython] O_element075  label="O_element : 0.066"  # scripted group (container) (typed FeaturePython)
  n = 0.066101
FEATURE [App::DocumentObjectGroupPython] S_element019  label="S_element : 0.020"  # scripted group (container) (typed FeaturePython)
  n = 0.00189
FEATURE [App::DocumentObjectGroupPython] Br_element004  label="Br_element : 0.349"  # scripted group (container) (typed FeaturePython)
  n = 0.349103
FEATURE [App::DocumentObjectGroupPython] Ag_element001  label="Ag_element : 0.474"  # scripted group (container) (typed FeaturePython)
  n = 0.474105
FEATURE [App::DocumentObjectGroupPython] I_element005  label="I_element : 0.003"  # scripted group (container) (typed FeaturePython)
  n = 0.00312
FEATURE [App::DocumentObjectGroupPython] G4_PHOTO_EMULSION  # scripted group (container) (typed FeaturePython)
  Dunit = g/cm3
  Dvalue = 3.815
  Group = -> [H_element070,C_element076,N_element035,O_element075,S_element019,Br_element004,Ag_element001,I_element005]
  conduct = 2
  density = 1
  expand = 3
  formula = G4_PHOTO_EMULSION
  name = G4_PHOTO_EMULSION
  specific = 4
FEATURE [App::DocumentObjectGroupPython] C_element077  label="C_element : 9"  # scripted group (container) (typed FeaturePython)
  n = 9
  ref = C_element
FEATURE [App::DocumentObjectGroupPython] H_element071  label="H_element : 033"  # scripted group (container) (typed FeaturePython)
  n = 10
  ref = H_element
FEATURE [App::DocumentObjectGroupPython] G4_PLASTIC_SC_VINYLTOLUENE  # scripted group (container) (typed FeaturePython)
  Dunit = g/cm3
  Dvalue = 1.032
  Group = -> [C_element077,H_element071]
  conduct = 2
  density = 1
  expand = 3
  formula = G4_PLASTIC_SC_VINYLTOLUENE
  name = G4_PLASTIC_SC_VINYLTOLUENE
  specific = 4
FEATURE [App::DocumentObjectGroupPython] Pu_element001  label="Pu_element : 1"  # scripted group (container) (typed FeaturePython)
  n = 1
  ref = Pu_element
FEATURE [App::DocumentObjectGroupPython] O_element076  label="O_element : 037"  # scripted group (container) (typed FeaturePython)
  n = 2
  ref = O_element
FEATURE [App::DocumentObjectGroupPython] G4_PLUTONIUM_DIOXIDE  # scripted group (container) (typed FeaturePython)
  Dunit = g/cm3
  Dvalue = 11.46
  Group = -> [Pu_element001,O_element076]
  conduct = 2
  density = 1
  expand = 3
  formula = G4_PLUTONIUM_DIOXIDE
  name = G4_PLUTONIUM_DIOXIDE
  specific = 4
FEATURE [App::DocumentObjectGroupPython] C_element078  label="C_element : 037"  # scripted group (container) (typed FeaturePython)
  n = 3
  ref = C_element
FEATURE [App::DocumentObjectGroupPython] H_element072  label="H_element : 034"  # scripted group (container) (typed FeaturePython)
  n = 3
  ref = H_element
FEATURE [App::DocumentObjectGroupPython] N_element036  label="N_element : 015"  # scripted group (container) (typed FeaturePython)
  n = 1
  ref = N_element
FEATURE [App::DocumentObjectGroupPython] G4_POLYACRYLONITRILE  # scripted group (container) (typed FeaturePython)
  Dunit = g/cm3
  Dvalue = 1.17
  Group = -> [C_element078,H_element072,N_element036]
  conduct = 2
  density = 1
  expand = 3
  formula = G4_POLYACRYLONITRILE
  name = G4_POLYACRYLONITRILE
  specific = 4
FEATURE [App::DocumentObjectGroupPython] C_element079  label="C_element : 16"  # scripted group (container) (typed FeaturePython)
  n = 16
  ref = C_element
FEATURE [App::DocumentObjectGroupPython] H_element073  label="H_element : 035"  # scripted group (container) (typed FeaturePython)
  n = 14
  ref = H_element
FEATURE [App::DocumentObjectGroupPython] O_element077  label="O_element : 038"  # scripted group (container) (typed FeaturePython)
  n = 3
  ref = O_element
FEATURE [App::DocumentObjectGroupPython] G4_POLYCARBONATE  # scripted group (container) (typed FeaturePython)
  Dunit = g/cm3
  Dvalue = 1.2
  Group = -> [C_element079,H_element073,O_element077]
  conduct = 2
  density = 1
  expand = 3
  formula = G4_POLYCARBONATE
  name = G4_POLYCARBONATE
  specific = 4
FEATURE [App::DocumentObjectGroupPython] C_element080  label="C_element : 038"  # scripted group (container) (typed FeaturePython)
  n = 8
  ref = C_element
FEATURE [App::DocumentObjectGroupPython] H_element074  label="H_element : 036"  # scripted group (container) (typed FeaturePython)
  n = 7
  ref = H_element
FEATURE [App::DocumentObjectGroupPython] Cl_element017  label="Cl_element : 007"  # scripted group (container) (typed FeaturePython)
  n = 1
  ref = Cl_element
FEATURE [App::DocumentObjectGroupPython] G4_POLYCHLOROSTYRENE  # scripted group (container) (typed FeaturePython)
  Dunit = g/cm3
  Dvalue = 1.3
  Group = -> [C_element080,H_element074,Cl_element017]
  conduct = 2
  density = 1
  expand = 3
  formula = G4_POLYCHLOROSTYRENE
  name = G4_POLYCHLOROSTYRENE
  specific = 4
FEATURE [App::DocumentObjectGroupPython] C_element081  label="C_element : 039"  # scripted group (container) (typed FeaturePython)
  n = 1
  ref = C_element
FEATURE [App::DocumentObjectGroupPython] H_element075  label="H_element : 037"  # scripted group (container) (typed FeaturePython)
  n = 2
  ref = H_element
FEATURE [App::DocumentObjectGroupPython] G4_POLYETHYLENE  # scripted group (container) (typed FeaturePython)
  Dunit = g/cm3
  Dvalue = 0.94
  Group = -> [C_element081,H_element075]
  conduct = 2
  density = 1
  expand = 3
  formula = G4_POLYETHYLENE
  name = G4_POLYETHYLENE
  specific = 4
FEATURE [App::DocumentObjectGroupPython] C_element082  label="C_element : 040"  # scripted group (container) (typed FeaturePython)
  n = 10
  ref = C_element
FEATURE [App::DocumentObjectGroupPython] H_element076  label="H_element : 038"  # scripted group (container) (typed FeaturePython)
  n = 8
  ref = H_element
FEATURE [App::DocumentObjectGroupPython] O_element078  label="O_element : 039"  # scripted group (container) (typed FeaturePython)
  n = 4
  ref = O_element
FEATURE [App::DocumentObjectGroupPython] G4_MYLAR  # scripted group (container) (typed FeaturePython)
  Dunit = g/cm3
  Dvalue = 1.4
  Group = -> [C_element082,H_element076,O_element078]
  conduct = 2
  density = 1
  expand = 3
  formula = G4_MYLAR
  name = G4_MYLAR
  specific = 4
FEATURE [App::DocumentObjectGroupPython] C_element083  label="C_element : 041"  # scripted group (container) (typed FeaturePython)
  n = 5
  ref = C_element
FEATURE [App::DocumentObjectGroupPython] H_element077  label="H_element : 039"  # scripted group (container) (typed FeaturePython)
  n = 8
  ref = H_element
FEATURE [App::DocumentObjectGroupPython] O_element079  label="O_element : 040"  # scripted group (container) (typed FeaturePython)
  n = 2
  ref = O_element
FEATURE [App::DocumentObjectGroupPython] G4_PLEXIGLASS  # scripted group (container) (typed FeaturePython)
  Dunit = g/cm3
  Dvalue = 1.19
  Group = -> [C_element083,H_element077,O_element079]
  conduct = 2
  density = 1
  expand = 3
  formula = G4_PLEXIGLASS
  name = G4_PLEXIGLASS
  specific = 4
FEATURE [App::DocumentObjectGroupPython] C_element084  label="C_element : 042"  # scripted group (container) (typed FeaturePython)
  n = 1
  ref = C_element
FEATURE [App::DocumentObjectGroupPython] H_element078  label="H_element : 040"  # scripted group (container) (typed FeaturePython)
  n = 2
  ref = H_element
FEATURE [App::DocumentObjectGroupPython] O_element080  label="O_element : 041"  # scripted group (container) (typed FeaturePython)
  n = 1
  ref = O_element
FEATURE [App::DocumentObjectGroupPython] G4_POLYOXYMETHYLENE  # scripted group (container) (typed FeaturePython)
  Dunit = g/cm3
  Dvalue = 1.425
  Group = -> [C_element084,H_element078,O_element080]
  conduct = 2
  density = 1
  expand = 3
  formula = G4_POLYOXYMETHYLENE
  name = G4_POLYOXYMETHYLENE
  specific = 4
FEATURE [App::DocumentObjectGroupPython] C_element085  label="C_element : 043"  # scripted group (container) (typed FeaturePython)
  n = 2
  ref = C_element
FEATURE [App::DocumentObjectGroupPython] H_element079  label="H_element : 041"  # scripted group (container) (typed FeaturePython)
  n = 4
  ref = H_element
FEATURE [App::DocumentObjectGroupPython] G4_POLYPROPYLENE  # scripted group (container) (typed FeaturePython)
  Dunit = g/cm3
  Dvalue = 0.9
  Group = -> [C_element085,H_element079]
  conduct = 2
  density = 1
  expand = 3
  formula = G4_POLYPROPYLENE
  name = G4_POLYPROPYLENE
  specific = 4
FEATURE [App::DocumentObjectGroupPython] C_element086  label="C_element : 044"  # scripted group (container) (typed FeaturePython)
  n = 8
  ref = C_element
FEATURE [App::DocumentObjectGroupPython] H_element080  label="H_element : 042"  # scripted group (container) (typed FeaturePython)
  n = 8
  ref = H_element
FEATURE [App::DocumentObjectGroupPython] G4_POLYSTYRENE  # scripted group (container) (typed FeaturePython)
  Dunit = g/cm3
  Dvalue = 1.06
  Group = -> [C_element086,H_element080]
  conduct = 2
  density = 1
  expand = 3
  formula = G4_POLYSTYRENE
  name = G4_POLYSTYRENE
  specific = 4
FEATURE [App::DocumentObjectGroupPython] C_element087  label="C_element : 045"  # scripted group (container) (typed FeaturePython)
  n = 2
  ref = C_element
FEATURE [App::DocumentObjectGroupPython] F_element014  label="F_element : 4"  # scripted group (container) (typed FeaturePython)
  n = 4
  ref = F_element
FEATURE [App::DocumentObjectGroupPython] G4_TEFLON  # scripted group (container) (typed FeaturePython)
  Dunit = g/cm3
  Dvalue = 2.2
  Group = -> [C_element087,F_element014]
  conduct = 2
  density = 1
  expand = 3
  formula = G4_TEFLON
  name = G4_TEFLON
  specific = 4
FEATURE [App::DocumentObjectGroupPython] C_element088  label="C_element : 046"  # scripted group (container) (typed FeaturePython)
  n = 2
  ref = C_element
FEATURE [App::DocumentObjectGroupPython] F_element015  label="F_element : 006"  # scripted group (container) (typed FeaturePython)
  n = 3
  ref = F_element
FEATURE [App::DocumentObjectGroupPython] Cl_element018  label="Cl_element : 008"  # scripted group (container) (typed FeaturePython)
  n = 1
  ref = Cl_element
FEATURE [App::DocumentObjectGroupPython] G4_POLYTRIFLUOROCHLOROETHYLENE  # scripted group (container) (typed FeaturePython)
  Dunit = g/cm3
  Dvalue = 2.1
  Group = -> [C_element088,F_element015,Cl_element018]
  conduct = 2
  density = 1
  expand = 3
  formula = G4_POLYTRIFLUOROCHLOROETHYLENE
  name = G4_POLYTRIFLUOROCHLOROETHYLENE
  specific = 4
FEATURE [App::DocumentObjectGroupPython] C_element089  label="C_element : 047"  # scripted group (container) (typed FeaturePython)
  n = 4
  ref = C_element
FEATURE [App::DocumentObjectGroupPython] H_element081  label="H_element : 043"  # scripted group (container) (typed FeaturePython)
  n = 6
  ref = H_element
FEATURE [App::DocumentObjectGroupPython] O_element081  label="O_element : 042"  # scripted group (container) (typed FeaturePython)
  n = 2
  ref = O_element
FEATURE [App::DocumentObjectGroupPython] G4_POLYVINYL_ACETATE  # scripted group (container) (typed FeaturePython)
  Dunit = g/cm3
  Dvalue = 1.19
  Group = -> [C_element089,H_element081,O_element081]
  conduct = 2
  density = 1
  expand = 3
  formula = G4_POLYVINYL_ACETATE
  name = G4_POLYVINYL_ACETATE
  specific = 4
FEATURE [App::DocumentObjectGroupPython] C_element090  label="C_element : 048"  # scripted group (container) (typed FeaturePython)
  n = 2
  ref = C_element
FEATURE [App::DocumentObjectGroupPython] H_element082  label="H_element : 044"  # scripted group (container) (typed FeaturePython)
  n = 4
  ref = H_element
FEATURE [App::DocumentObjectGroupPython] O_element082  label="O_element : 043"  # scripted group (container) (typed FeaturePython)
  n = 1
  ref = O_element
FEATURE [App::DocumentObjectGroupPython] G4_POLYVINYL_ALCOHOL  # scripted group (container) (typed FeaturePython)
  Dunit = g/cm3
  Dvalue = 1.3
  Group = -> [C_element090,H_element082,O_element082]
  conduct = 2
  density = 1
  expand = 3
  formula = G4_POLYVINYL_ALCOHOL
  name = G4_POLYVINYL_ALCOHOL
  specific = 4
FEATURE [App::DocumentObjectGroupPython] C_element091  label="C_element : 049"  # scripted group (container) (typed FeaturePython)
  n = 8
  ref = C_element
FEATURE [App::DocumentObjectGroupPython] H_element083  label="H_element : 045"  # scripted group (container) (typed FeaturePython)
  n = 14
  ref = H_element
FEATURE [App::DocumentObjectGroupPython] O_element083  label="O_element : 044"  # scripted group (container) (typed FeaturePython)
  n = 2
  ref = O_element
FEATURE [App::DocumentObjectGroupPython] G4_POLYVINYL_BUTYRAL  # scripted group (container) (typed FeaturePython)
  Dunit = g/cm3
  Dvalue = 1.12
  Group = -> [C_element091,H_element083,O_element083]
  conduct = 2
  density = 1
  expand = 3
  formula = G4_POLYVINYL_BUTYRAL
  name = G4_POLYVINYL_BUTYRAL
  specific = 4
FEATURE [App::DocumentObjectGroupPython] C_element092  label="C_element : 050"  # scripted group (container) (typed FeaturePython)
  n = 2
  ref = C_element
FEATURE [App::DocumentObjectGroupPython] H_element084  label="H_element : 046"  # scripted group (container) (typed FeaturePython)
  n = 3
  ref = H_element
FEATURE [App::DocumentObjectGroupPython] Cl_element019  label="Cl_element : 009"  # scripted group (container) (typed FeaturePython)
  n = 1
  ref = Cl_element
FEATURE [App::DocumentObjectGroupPython] G4_POLYVINYL_CHLORIDE  # scripted group (container) (typed FeaturePython)
  Dunit = g/cm3
  Dvalue = 1.3
  Group = -> [C_element092,H_element084,Cl_element019]
  conduct = 2
  density = 1
  expand = 3
  formula = G4_POLYVINYL_CHLORIDE
  name = G4_POLYVINYL_CHLORIDE
  specific = 4
FEATURE [App::DocumentObjectGroupPython] C_element093  label="C_element : 051"  # scripted group (container) (typed FeaturePython)
  n = 2
  ref = C_element
FEATURE [App::DocumentObjectGroupPython] H_element085  label="H_element : 047"  # scripted group (container) (typed FeaturePython)
  n = 2
  ref = H_element
FEATURE [App::DocumentObjectGroupPython] Cl_element020  label="Cl_element : 010"  # scripted group (container) (typed FeaturePython)
  n = 2
  ref = Cl_element
FEATURE [App::DocumentObjectGroupPython] G4_POLYVINYLIDENE_CHLORIDE  # scripted group (container) (typed FeaturePython)
  Dunit = g/cm3
  Dvalue = 1.7
  Group = -> [C_element093,H_element085,Cl_element020]
  conduct = 2
  density = 1
  expand = 3
  formula = G4_POLYVINYLIDENE_CHLORIDE
  name = G4_POLYVINYLIDENE_CHLORIDE
  specific = 4
FEATURE [App::DocumentObjectGroupPython] C_element094  label="C_element : 052"  # scripted group (container) (typed FeaturePython)
  n = 2
  ref = C_element
FEATURE [App::DocumentObjectGroupPython] H_element086  label="H_element : 048"  # scripted group (container) (typed FeaturePython)
  n = 2
  ref = H_element
FEATURE [App::DocumentObjectGroupPython] F_element016  label="F_element : 007"  # scripted group (container) (typed FeaturePython)
  n = 2
  ref = F_element
FEATURE [App::DocumentObjectGroupPython] G4_POLYVINYLIDENE_FLUORIDE  # scripted group (container) (typed FeaturePython)
  Dunit = g/cm3
  Dvalue = 1.76
  Group = -> [C_element094,H_element086,F_element016]
  conduct = 2
  density = 1
  expand = 3
  formula = G4_POLYVINYLIDENE_FLUORIDE
  name = G4_POLYVINYLIDENE_FLUORIDE
  specific = 4
FEATURE [App::DocumentObjectGroupPython] C_element095  label="C_element : 053"  # scripted group (container) (typed FeaturePython)
  n = 6
  ref = C_element
FEATURE [App::DocumentObjectGroupPython] H_element087  label="H_element : 9"  # scripted group (container) (typed FeaturePython)
  n = 9
  ref = H_element
FEATURE [App::DocumentObjectGroupPython] N_element037  label="N_element : 016"  # scripted group (container) (typed FeaturePython)
  n = 1
  ref = N_element
FEATURE [App::DocumentObjectGroupPython] O_element084  label="O_element : 045"  # scripted group (container) (typed FeaturePython)
  n = 1
  ref = O_element
FEATURE [App::DocumentObjectGroupPython] G4_POLYVINYL_PYRROLIDONE  # scripted group (container) (typed FeaturePython)
  Dunit = g/cm3
  Dvalue = 1.25
  Group = -> [C_element095,H_element087,N_element037,O_element084]
  conduct = 2
  density = 1
  expand = 3
  formula = G4_POLYVINYL_PYRROLIDONE
  name = G4_POLYVINYL_PYRROLIDONE
  specific = 4
FEATURE [App::DocumentObjectGroupPython] K_element008  label="K_element : 1"  # scripted group (container) (typed FeaturePython)
  n = 1
  ref = K_element
FEATURE [App::DocumentObjectGroupPython] I_element006  label="I_element : 003"  # scripted group (container) (typed FeaturePython)
  n = 1
  ref = I_element
FEATURE [App::DocumentObjectGroupPython] G4_POTASSIUM_IODIDE  # scripted group (container) (typed FeaturePython)
  Dunit = g/cm3
  Dvalue = 3.13
  Group = -> [K_element008,I_element006]
  conduct = 2
  density = 1
  expand = 3
  formula = G4_POTASSIUM_IODIDE
  name = G4_POTASSIUM_IODIDE
  specific = 4
FEATURE [App::DocumentObjectGroupPython] K_element009  label="K_element : 2"  # scripted group (container) (typed FeaturePython)
  n = 2
  ref = K_element
FEATURE [App::DocumentObjectGroupPython] O_element085  label="O_element : 046"  # scripted group (container) (typed FeaturePython)
  n = 1
  ref = O_element
FEATURE [App::DocumentObjectGroupPython] G4_POTASSIUM_OXIDE  # scripted group (container) (typed FeaturePython)
  Dunit = g/cm3
  Dvalue = 2.32
  Group = -> [K_element009,O_element085]
  conduct = 2
  density = 1
  expand = 3
  formula = G4_POTASSIUM_OXIDE
  name = G4_POTASSIUM_OXIDE
  specific = 4
FEATURE [App::DocumentObjectGroupPython] C_element096  label="C_element : 054"  # scripted group (container) (typed FeaturePython)
  n = 3
  ref = C_element
FEATURE [App::DocumentObjectGroupPython] H_element088  label="H_element : 049"  # scripted group (container) (typed FeaturePython)
  n = 8
  ref = H_element
FEATURE [App::DocumentObjectGroupPython] G4_PROPANE  # scripted group (container) (typed FeaturePython)
  Dunit = g/cm3
  Dvalue = 0.00187939
  Group = -> [C_element096,H_element088]
  conduct = 2
  density = 1
  expand = 3
  formula = G4_PROPANE
  name = G4_PROPANE
  specific = 4
FEATURE [App::DocumentObjectGroupPython] C_element097  label="C_element : 055"  # scripted group (container) (typed FeaturePython)
  n = 3
  ref = C_element
FEATURE [App::DocumentObjectGroupPython] H_element089  label="H_element : 050"  # scripted group (container) (typed FeaturePython)
  n = 8
  ref = H_element
FEATURE [App::DocumentObjectGroupPython] G4_lPROPANE  # scripted group (container) (typed FeaturePython)
  Dunit = g/cm3
  Dvalue = 0.43
  Group = -> [C_element097,H_element089]
  conduct = 2
  density = 1
  expand = 3
  formula = G4_lPROPANE
  name = G4_lPROPANE
  specific = 4
FEATURE [App::DocumentObjectGroupPython] C_element098  label="C_element : 056"  # scripted group (container) (typed FeaturePython)
  n = 3
  ref = C_element
FEATURE [App::DocumentObjectGroupPython] H_element090  label="H_element : 051"  # scripted group (container) (typed FeaturePython)
  n = 8
  ref = H_element
FEATURE [App::DocumentObjectGroupPython] O_element086  label="O_element : 047"  # scripted group (container) (typed FeaturePython)
  n = 1
  ref = O_element
FEATURE [App::DocumentObjectGroupPython] G4_N_PROPYL_ALCOHOL  label="G4_N-PROPYL_ALCOHOL"  # scripted group (container) (typed FeaturePython)
  Dunit = g/cm3
  Dvalue = 0.8035
  Group = -> [C_element098,H_element090,O_element086]
  conduct = 2
  density = 1
  expand = 3
  formula = G4_N-PROPYL_ALCOHOL
  name = G4_N-PROPYL_ALCOHOL
  specific = 4
FEATURE [App::DocumentObjectGroupPython] C_element099  label="C_element : 057"  # scripted group (container) (typed FeaturePython)
  n = 5
  ref = C_element
FEATURE [App::DocumentObjectGroupPython] H_element091  label="H_element : 052"  # scripted group (container) (typed FeaturePython)
  n = 5
  ref = H_element
FEATURE [App::DocumentObjectGroupPython] N_element038  label="N_element : 017"  # scripted group (container) (typed FeaturePython)
  n = 1
  ref = N_element
FEATURE [App::DocumentObjectGroupPython] G4_PYRIDINE  # scripted group (container) (typed FeaturePython)
  Dunit = g/cm3
  Dvalue = 0.9819
  Group = -> [C_element099,H_element091,N_element038]
  conduct = 2
  density = 1
  expand = 3
  formula = G4_PYRIDINE
  name = G4_PYRIDINE
  specific = 4
FEATURE [App::DocumentObjectGroupPython] H_element092  label="H_element : 0.144"  # scripted group (container) (typed FeaturePython)
  n = 0.143711
FEATURE [App::DocumentObjectGroupPython] C_element100  label="C_element : 0.856"  # scripted group (container) (typed FeaturePython)
  n = 0.856289
FEATURE [App::DocumentObjectGroupPython] G4_RUBBER_BUTYL  # scripted group (container) (typed FeaturePython)
  Dunit = g/cm3
  Dvalue = 0.92
  Group = -> [H_element092,C_element100]
  conduct = 2
  density = 1
  expand = 3
  formula = G4_RUBBER_BUTYL
  name = G4_RUBBER_BUTYL
  specific = 4
FEATURE [App::DocumentObjectGroupPython] H_element093  label="H_element : 0.118"  # scripted group (container) (typed FeaturePython)
  n = 0.118371
FEATURE [App::DocumentObjectGroupPython] C_element101  label="C_element : 0.882"  # scripted group (container) (typed FeaturePython)
  n = 0.881629
FEATURE [App::DocumentObjectGroupPython] G4_RUBBER_NATURAL  # scripted group (container) (typed FeaturePython)
  Dunit = g/cm3
  Dvalue = 0.92
  Group = -> [H_element093,C_element101]
  conduct = 2
  density = 1
  expand = 3
  formula = G4_RUBBER_NATURAL
  name = G4_RUBBER_NATURAL
  specific = 4
FEATURE [App::DocumentObjectGroupPython] H_element094  label="H_element : 0.145"  # scripted group (container) (typed FeaturePython)
  n = 0.05692
FEATURE [App::DocumentObjectGroupPython] C_element102  label="C_element : 0.543"  # scripted group (container) (typed FeaturePython)
  n = 0.542646
FEATURE [App::DocumentObjectGroupPython] Cl_element021  label="Cl_element : 0.400"  # scripted group (container) (typed FeaturePython)
  n = 0.400434
FEATURE [App::DocumentObjectGroupPython] G4_RUBBER_NEOPRENE  # scripted group (container) (typed FeaturePython)
  Dunit = g/cm3
  Dvalue = 1.23
  Group = -> [H_element094,C_element102,Cl_element021]
  conduct = 2
  density = 1
  expand = 3
  formula = G4_RUBBER_NEOPRENE
  name = G4_RUBBER_NEOPRENE
  specific = 4
FEATURE [App::DocumentObjectGroupPython] Si_element006  label="Si_element : 1"  # scripted group (container) (typed FeaturePython)
  n = 1
  ref = Si_element
FEATURE [App::DocumentObjectGroupPython] O_element087  label="O_element : 048"  # scripted group (container) (typed FeaturePython)
  n = 2
  ref = O_element
FEATURE [App::DocumentObjectGroupPython] G4_SILICON_DIOXIDE  # scripted group (container) (typed FeaturePython)
  Dunit = g/cm3
  Dvalue = 2.32
  Group = -> [Si_element006,O_element087]
  conduct = 2
  density = 1
  expand = 3
  formula = G4_SILICON_DIOXIDE
  name = G4_SILICON_DIOXIDE
  specific = 4
FEATURE [App::DocumentObjectGroupPython] Ag_element002  label="Ag_element : 1"  # scripted group (container) (typed FeaturePython)
  n = 1
  ref = Ag_element
FEATURE [App::DocumentObjectGroupPython] Br_element005  label="Br_element : 003"  # scripted group (container) (typed FeaturePython)
  n = 1
  ref = Br_element
FEATURE [App::DocumentObjectGroupPython] G4_SILVER_BROMIDE  # scripted group (container) (typed FeaturePython)
  Dunit = g/cm3
  Dvalue = 6.473
  Group = -> [Ag_element002,Br_element005]
  conduct = 2
  density = 1
  expand = 3
  formula = G4_SILVER_BROMIDE
  name = G4_SILVER_BROMIDE
  specific = 4
FEATURE [App::DocumentObjectGroupPython] Ag_element003  label="Ag_element : 002"  # scripted group (container) (typed FeaturePython)
  n = 1
  ref = Ag_element
FEATURE [App::DocumentObjectGroupPython] Cl_element022  label="Cl_element : 011"  # scripted group (container) (typed FeaturePython)
  n = 1
  ref = Cl_element
FEATURE [App::DocumentObjectGroupPython] G4_SILVER_CHLORIDE  # scripted group (container) (typed FeaturePython)
  Dunit = g/cm3
  Dvalue = 5.56
  Group = -> [Ag_element003,Cl_element022]
  conduct = 2
  density = 1
  expand = 3
  formula = G4_SILVER_CHLORIDE
  name = G4_SILVER_CHLORIDE
  specific = 4
FEATURE [App::DocumentObjectGroupPython] Br_element006  label="Br_element : 0.423"  # scripted group (container) (typed FeaturePython)
  n = 0.422895
FEATURE [App::DocumentObjectGroupPython] Ag_element004  label="Ag_element : 0.574"  # scripted group (container) (typed FeaturePython)
  n = 0.573748
FEATURE [App::DocumentObjectGroupPython] I_element007  label="I_element : 0.649"  # scripted group (container) (typed FeaturePython)
  n = 0.003357
FEATURE [App::DocumentObjectGroupPython] G4_SILVER_HALIDES  # scripted group (container) (typed FeaturePython)
  Dunit = g/cm3
  Dvalue = 6.47
  Group = -> [Br_element006,Ag_element004,I_element007]
  conduct = 2
  density = 1
  expand = 3
  formula = G4_SILVER_HALIDES
  name = G4_SILVER_HALIDES
  specific = 4
FEATURE [App::DocumentObjectGroupPython] Ag_element005  label="Ag_element : 003"  # scripted group (container) (typed FeaturePython)
  n = 1
  ref = Ag_element
FEATURE [App::DocumentObjectGroupPython] I_element008  label="I_element : 004"  # scripted group (container) (typed FeaturePython)
  n = 1
  ref = I_element
FEATURE [App::DocumentObjectGroupPython] G4_SILVER_IODIDE  # scripted group (container) (typed FeaturePython)
  Dunit = g/cm3
  Dvalue = 6.01
  Group = -> [Ag_element005,I_element008]
  conduct = 2
  density = 1
  expand = 3
  formula = G4_SILVER_IODIDE
  name = G4_SILVER_IODIDE
  specific = 4
FEATURE [App::DocumentObjectGroupPython] H_element095  label="H_element : 0.100"  # scripted group (container) (typed FeaturePython)
  n = 0.1
FEATURE [App::DocumentObjectGroupPython] C_element103  label="C_element : 0.204"  # scripted group (container) (typed FeaturePython)
  n = 0.204
FEATURE [App::DocumentObjectGroupPython] N_element039  label="N_element : 0.759"  # scripted group (container) (typed FeaturePython)
  n = 0.042
FEATURE [App::DocumentObjectGroupPython] O_element088  label="O_element : 0.645"  # scripted group (container) (typed FeaturePython)
  n = 0.645
FEATURE [App::DocumentObjectGroupPython] Na_element013  label="Na_element : 0.100"  # scripted group (container) (typed FeaturePython)
  n = 0.002
FEATURE [App::DocumentObjectGroupPython] P_element009  label="P_element : 0.107"  # scripted group (container) (typed FeaturePython)
  n = 0.001
FEATURE [App::DocumentObjectGroupPython] S_element020  label="S_element : 0.021"  # scripted group (container) (typed FeaturePython)
  n = 0.002
FEATURE [App::DocumentObjectGroupPython] Cl_element023  label="Cl_element : 0.590"  # scripted group (container) (typed FeaturePython)
  n = 0.003
FEATURE [App::DocumentObjectGroupPython] K_element010  label="K_element : 0.001"  # scripted group (container) (typed FeaturePython)
  n = 0.001
FEATURE [App::DocumentObjectGroupPython] G4_SKIN_ICRP  # scripted group (container) (typed FeaturePython)
  Dunit = g/cm3
  Dvalue = 1.09
  Group = -> [H_element095,C_element103,N_element039,O_element088,Na_element013,P_element009,S_element020,Cl_element023,K_element010]
  conduct = 2
  density = 1
  expand = 3
  formula = G4_SKIN_ICRP
  name = G4_SKIN_ICRP
  specific = 4
FEATURE [App::DocumentObjectGroupPython] Na_element014  label="Na_element : 2"  # scripted group (container) (typed FeaturePython)
  n = 2
  ref = Na_element
FEATURE [App::DocumentObjectGroupPython] C_element104  label="C_element : 058"  # scripted group (container) (typed FeaturePython)
  n = 1
  ref = C_element
FEATURE [App::DocumentObjectGroupPython] O_element089  label="O_element : 049"  # scripted group (container) (typed FeaturePython)
  n = 3
  ref = O_element
FEATURE [App::DocumentObjectGroupPython] G4_SODIUM_CARBONATE  # scripted group (container) (typed FeaturePython)
  Dunit = g/cm3
  Dvalue = 2.532
  Group = -> [Na_element014,C_element104,O_element089]
  conduct = 2
  density = 1
  expand = 3
  formula = G4_SODIUM_CARBONATE
  name = G4_SODIUM_CARBONATE
  specific = 4
FEATURE [App::DocumentObjectGroupPython] Na_element015  label="Na_element : 1"  # scripted group (container) (typed FeaturePython)
  n = 1
  ref = Na_element
FEATURE [App::DocumentObjectGroupPython] I_element009  label="I_element : 005"  # scripted group (container) (typed FeaturePython)
  n = 1
  ref = I_element
FEATURE [App::DocumentObjectGroupPython] G4_SODIUM_IODIDE  # scripted group (container) (typed FeaturePython)
  Dunit = g/cm3
  Dvalue = 3.667
  Group = -> [Na_element015,I_element009]
  conduct = 2
  density = 1
  expand = 3
  formula = G4_SODIUM_IODIDE
  name = G4_SODIUM_IODIDE
  specific = 4
FEATURE [App::DocumentObjectGroupPython] Na_element016  label="Na_element : 003"  # scripted group (container) (typed FeaturePython)
  n = 2
  ref = Na_element
FEATURE [App::DocumentObjectGroupPython] O_element090  label="O_element : 050"  # scripted group (container) (typed FeaturePython)
  n = 1
  ref = O_element
FEATURE [App::DocumentObjectGroupPython] G4_SODIUM_MONOXIDE  # scripted group (container) (typed FeaturePython)
  Dunit = g/cm3
  Dvalue = 2.27
  Group = -> [Na_element016,O_element090]
  conduct = 2
  density = 1
  expand = 3
  formula = G4_SODIUM_MONOXIDE
  name = G4_SODIUM_MONOXIDE
  specific = 4
FEATURE [App::DocumentObjectGroupPython] Na_element017  label="Na_element : 004"  # scripted group (container) (typed FeaturePython)
  n = 1
  ref = Na_element
FEATURE [App::DocumentObjectGroupPython] N_element040  label="N_element : 018"  # scripted group (container) (typed FeaturePython)
  n = 1
  ref = N_element
FEATURE [App::DocumentObjectGroupPython] O_element091  label="O_element : 051"  # scripted group (container) (typed FeaturePython)
  n = 3
  ref = O_element
FEATURE [App::DocumentObjectGroupPython] G4_SODIUM_NITRATE  # scripted group (container) (typed FeaturePython)
  Dunit = g/cm3
  Dvalue = 2.261
  Group = -> [Na_element017,N_element040,O_element091]
  conduct = 2
  density = 1
  expand = 3
  formula = G4_SODIUM_NITRATE
  name = G4_SODIUM_NITRATE
  specific = 4
FEATURE [App::DocumentObjectGroupPython] C_element105  label="C_element : 059"  # scripted group (container) (typed FeaturePython)
  n = 14
  ref = C_element
FEATURE [App::DocumentObjectGroupPython] H_element096  label="H_element : 053"  # scripted group (container) (typed FeaturePython)
  n = 12
  ref = H_element
FEATURE [App::DocumentObjectGroupPython] G4_STILBENE  # scripted group (container) (typed FeaturePython)
  Dunit = g/cm3
  Dvalue = 0.9707
  Group = -> [C_element105,H_element096]
  conduct = 2
  density = 1
  expand = 3
  formula = G4_STILBENE
  name = G4_STILBENE
  specific = 4
FEATURE [App::DocumentObjectGroupPython] C_element106  label="C_element : 12"  # scripted group (container) (typed FeaturePython)
  n = 12
  ref = C_element
FEATURE [App::DocumentObjectGroupPython] H_element097  label="H_element : 22"  # scripted group (container) (typed FeaturePython)
  n = 22
  ref = H_element
FEATURE [App::DocumentObjectGroupPython] O_element092  label="O_element : 11"  # scripted group (container) (typed FeaturePython)
  n = 11
  ref = O_element
FEATURE [App::DocumentObjectGroupPython] G4_SUCROSE  # scripted group (container) (typed FeaturePython)
  Dunit = g/cm3
  Dvalue = 1.5805
  Group = -> [C_element106,H_element097,O_element092]
  conduct = 2
  density = 1
  expand = 3
  formula = G4_SUCROSE
  name = G4_SUCROSE
  specific = 4
FEATURE [App::DocumentObjectGroupPython] C_element107  label="C_element : 18"  # scripted group (container) (typed FeaturePython)
  n = 18
  ref = C_element
FEATURE [App::DocumentObjectGroupPython] H_element098  label="H_element : 054"  # scripted group (container) (typed FeaturePython)
  n = 14
  ref = H_element
FEATURE [App::DocumentObjectGroupPython] G4_TERPHENYL  # scripted group (container) (typed FeaturePython)
  Dunit = g/cm3
  Dvalue = 1.24
  Group = -> [C_element107,H_element098]
  conduct = 2
  density = 1
  expand = 3
  formula = G4_TERPHENYL
  name = G4_TERPHENYL
  specific = 4
FEATURE [App::DocumentObjectGroupPython] H_element099  label="H_element : 0.146"  # scripted group (container) (typed FeaturePython)
  n = 0.106
FEATURE [App::DocumentObjectGroupPython] C_element108  label="C_element : 0.883"  # scripted group (container) (typed FeaturePython)
  n = 0.099
FEATURE [App::DocumentObjectGroupPython] N_element041  label="N_element : 0.020"  # scripted group (container) (typed FeaturePython)
  n = 0.02
FEATURE [App::DocumentObjectGroupPython] O_element093  label="O_element : 0.766"  # scripted group (container) (typed FeaturePython)
  n = 0.766
FEATURE [App::DocumentObjectGroupPython] Na_element018  label="Na_element : 0.101"  # scripted group (container) (typed FeaturePython)
  n = 0.002
FEATURE [App::DocumentObjectGroupPython] P_element010  label="P_element : 0.108"  # scripted group (container) (typed FeaturePython)
  n = 0.001
FEATURE [App::DocumentObjectGroupPython] S_element021  label="S_element : 0.022"  # scripted group (container) (typed FeaturePython)
  n = 0.002
FEATURE [App::DocumentObjectGroupPython] Cl_element024  label="Cl_element : 0.002"  # scripted group (container) (typed FeaturePython)
  n = 0.002
FEATURE [App::DocumentObjectGroupPython] K_element011  label="K_element : 0.017"  # scripted group (container) (typed FeaturePython)
  n = 0.002
FEATURE [App::DocumentObjectGroupPython] G4_TESTIS_ICRP  # scripted group (container) (typed FeaturePython)
  Dunit = g/cm3
  Dvalue = 1.04
  Group = -> [H_element099,C_element108,N_element041,O_element093,Na_element018,P_element010,S_element021,Cl_element024,K_element011]
  conduct = 2
  density = 1
  expand = 3
  formula = G4_TESTIS_ICRP
  name = G4_TESTIS_ICRP
  specific = 4
FEATURE [App::DocumentObjectGroupPython] C_element109  label="C_element : 060"  # scripted group (container) (typed FeaturePython)
  n = 2
  ref = C_element
FEATURE [App::DocumentObjectGroupPython] Cl_element025  label="Cl_element : 012"  # scripted group (container) (typed FeaturePython)
  n = 4
  ref = Cl_element
FEATURE [App::DocumentObjectGroupPython] G4_TETRACHLOROETHYLENE  # scripted group (container) (typed FeaturePython)
  Dunit = g/cm3
  Dvalue = 1.625
  Group = -> [C_element109,Cl_element025]
  conduct = 2
  density = 1
  expand = 3
  formula = G4_TETRACHLOROETHYLENE
  name = G4_TETRACHLOROETHYLENE
  specific = 4
FEATURE [App::DocumentObjectGroupPython] Tl_element001  label="Tl_element : 1"  # scripted group (container) (typed FeaturePython)
  n = 1
  ref = Tl_element
FEATURE [App::DocumentObjectGroupPython] Cl_element026  label="Cl_element : 013"  # scripted group (container) (typed FeaturePython)
  n = 1
  ref = Cl_element
FEATURE [App::DocumentObjectGroupPython] G4_THALLIUM_CHLORIDE  # scripted group (container) (typed FeaturePython)
  Dunit = g/cm3
  Dvalue = 7.004
  Group = -> [Tl_element001,Cl_element026]
  conduct = 2
  density = 1
  expand = 3
  formula = G4_THALLIUM_CHLORIDE
  name = G4_THALLIUM_CHLORIDE
  specific = 4
FEATURE [App::DocumentObjectGroupPython] H_element100  label="H_element : 0.147"  # scripted group (container) (typed FeaturePython)
  n = 0.105
FEATURE [App::DocumentObjectGroupPython] C_element110  label="C_element : 0.256"  # scripted group (container) (typed FeaturePython)
  n = 0.256
FEATURE [App::DocumentObjectGroupPython] N_element042  label="N_element : 0.760"  # scripted group (container) (typed FeaturePython)
  n = 0.027
FEATURE [App::DocumentObjectGroupPython] O_element094  label="O_element : 0.602"  # scripted group (container) (typed FeaturePython)
  n = 0.602
FEATURE [App::DocumentObjectGroupPython] Na_element019  label="Na_element : 0.102"  # scripted group (container) (typed FeaturePython)
  n = 0.001
FEATURE [App::DocumentObjectGroupPython] P_element011  label="P_element : 0.109"  # scripted group (container) (typed FeaturePython)
  n = 0.002
FEATURE [App::DocumentObjectGroupPython] S_element022  label="S_element : 0.023"  # scripted group (container) (typed FeaturePython)
  n = 0.003
FEATURE [App::DocumentObjectGroupPython] Cl_element027  label="Cl_element : 0.591"  # scripted group (container) (typed FeaturePython)
  n = 0.002
FEATURE [App::DocumentObjectGroupPython] K_element012  label="K_element : 0.018"  # scripted group (container) (typed FeaturePython)
  n = 0.002
FEATURE [App::DocumentObjectGroupPython] G4_TISSUE_SOFT_ICRP  # scripted group (container) (typed FeaturePython)
  Dunit = g/cm3
  Dvalue = 1.03
  Group = -> [H_element100,C_element110,N_element042,O_element094,Na_element019,P_element011,S_element022,Cl_element027,K_element012]
  conduct = 2
  density = 1
  expand = 3
  formula = G4_TISSUE_SOFT_ICRP
  name = G4_TISSUE_SOFT_ICRP
  specific = 4
FEATURE [App::DocumentObjectGroupPython] H_element101  label="H_element : 0.148"  # scripted group (container) (typed FeaturePython)
  n = 0.101
FEATURE [App::DocumentObjectGroupPython] C_element111  label="C_element : 0.111"  # scripted group (container) (typed FeaturePython)
  n = 0.111
FEATURE [App::DocumentObjectGroupPython] N_element043  label="N_element : 0.026"  # scripted group (container) (typed FeaturePython)
  n = 0.026
FEATURE [App::DocumentObjectGroupPython] O_element095  label="O_element : 0.762"  # scripted group (container) (typed FeaturePython)
  n = 0.762
FEATURE [App::DocumentObjectGroupPython] G4_TISSUE_SOFT_ICRU_4  label="G4_TISSUE_SOFT_ICRU-4"  # scripted group (container) (typed FeaturePython)
  Dunit = g/cm3
  Dvalue = 1
  Group = -> [H_element101,C_element111,N_element043,O_element095]
  conduct = 2
  density = 1
  expand = 3
  formula = G4_TISSUE_SOFT_ICRU-4
  name = G4_TISSUE_SOFT_ICRU-4
  specific = 4
FEATURE [App::DocumentObjectGroupPython] H_element102  label="H_element : 0.149"  # scripted group (container) (typed FeaturePython)
  n = 0.101869
FEATURE [App::DocumentObjectGroupPython] C_element112  label="C_element : 0.456"  # scripted group (container) (typed FeaturePython)
  n = 0.456179
FEATURE [App::DocumentObjectGroupPython] N_element044  label="N_element : 0.761"  # scripted group (container) (typed FeaturePython)
  n = 0.035172
FEATURE [App::DocumentObjectGroupPython] O_element096  label="O_element : 0.407"  # scripted group (container) (typed FeaturePython)
  n = 0.40678
FEATURE [App::DocumentObjectGroupPython] G4_TISSUE_METHANE  label="G4_TISSUE-METHANE"  # scripted group (container) (typed FeaturePython)
  Dunit = g/cm3
  Dvalue = 0.00106409
  Group = -> [H_element102,C_element112,N_element044,O_element096]
  conduct = 2
  density = 1
  expand = 3
  formula = G4_TISSUE-METHANE
  name = G4_TISSUE-METHANE
  specific = 4
FEATURE [App::DocumentObjectGroupPython] H_element103  label="H_element : 0.103"  # scripted group (container) (typed FeaturePython)
  n = 0.102672
FEATURE [App::DocumentObjectGroupPython] C_element113  label="C_element : 0.569"  # scripted group (container) (typed FeaturePython)
  n = 0.56894
FEATURE [App::DocumentObjectGroupPython] N_element045  label="N_element : 0.762"  # scripted group (container) (typed FeaturePython)
  n = 0.035022
FEATURE [App::DocumentObjectGroupPython] O_element097  label="O_element : 0.293"  # scripted group (container) (typed FeaturePython)
  n = 0.293366
FEATURE [App::DocumentObjectGroupPython] G4_TISSUE_PROPANE  label="G4_TISSUE-PROPANE"  # scripted group (container) (typed FeaturePython)
  Dunit = g/cm3
  Dvalue = 0.00182628
  Group = -> [H_element103,C_element113,N_element045,O_element097]
  conduct = 2
  density = 1
  expand = 3
  formula = G4_TISSUE-PROPANE
  name = G4_TISSUE-PROPANE
  specific = 4
FEATURE [App::DocumentObjectGroupPython] Ti_element003  label="Ti_element : 1"  # scripted group (container) (typed FeaturePython)
  n = 1
  ref = Ti_element
FEATURE [App::DocumentObjectGroupPython] O_element098  label="O_element : 052"  # scripted group (container) (typed FeaturePython)
  n = 2
  ref = O_element
FEATURE [App::DocumentObjectGroupPython] G4_TITANIUM_DIOXIDE  # scripted group (container) (typed FeaturePython)
  Dunit = g/cm3
  Dvalue = 4.26
  Group = -> [Ti_element003,O_element098]
  conduct = 2
  density = 1
  expand = 3
  formula = G4_TITANIUM_DIOXIDE
  name = G4_TITANIUM_DIOXIDE
  specific = 4
FEATURE [App::DocumentObjectGroupPython] C_element114  label="C_element : 061"  # scripted group (container) (typed FeaturePython)
  n = 7
  ref = C_element
FEATURE [App::DocumentObjectGroupPython] H_element104  label="H_element : 055"  # scripted group (container) (typed FeaturePython)
  n = 8
  ref = H_element
FEATURE [App::DocumentObjectGroupPython] G4_TOLUENE  # scripted group (container) (typed FeaturePython)
  Dunit = g/cm3
  Dvalue = 0.8669
  Group = -> [C_element114,H_element104]
  conduct = 2
  density = 1
  expand = 3
  formula = G4_TOLUENE
  name = G4_TOLUENE
  specific = 4
FEATURE [App::DocumentObjectGroupPython] C_element115  label="C_element : 062"  # scripted group (container) (typed FeaturePython)
  n = 2
  ref = C_element
FEATURE [App::DocumentObjectGroupPython] H_element105  label="H_element : 056"  # scripted group (container) (typed FeaturePython)
  n = 1
  ref = H_element
FEATURE [App::DocumentObjectGroupPython] Cl_element028  label="Cl_element : 014"  # scripted group (container) (typed FeaturePython)
  n = 3
  ref = Cl_element
FEATURE [App::DocumentObjectGroupPython] G4_TRICHLOROETHYLENE  # scripted group (container) (typed FeaturePython)
  Dunit = g/cm3
  Dvalue = 1.46
  Group = -> [C_element115,H_element105,Cl_element028]
  conduct = 2
  density = 1
  expand = 3
  formula = G4_TRICHLOROETHYLENE
  name = G4_TRICHLOROETHYLENE
  specific = 4
FEATURE [App::DocumentObjectGroupPython] C_element116  label="C_element : 063"  # scripted group (container) (typed FeaturePython)
  n = 6
  ref = C_element
FEATURE [App::DocumentObjectGroupPython] H_element106  label="H_element : 15"  # scripted group (container) (typed FeaturePython)
  n = 15
  ref = H_element
FEATURE [App::DocumentObjectGroupPython] O_element099  label="O_element : 053"  # scripted group (container) (typed FeaturePython)
  n = 4
  ref = O_element
FEATURE [App::DocumentObjectGroupPython] P_element012  label="P_element : 1"  # scripted group (container) (typed FeaturePython)
  n = 1
  ref = P_element
FEATURE [App::DocumentObjectGroupPython] G4_TRIETHYL_PHOSPHATE  # scripted group (container) (typed FeaturePython)
  Dunit = g/cm3
  Dvalue = 1.07
  Group = -> [C_element116,H_element106,O_element099,P_element012]
  conduct = 2
  density = 1
  expand = 3
  formula = G4_TRIETHYL_PHOSPHATE
  name = G4_TRIETHYL_PHOSPHATE
  specific = 4
FEATURE [App::DocumentObjectGroupPython] W_element003  label="W_element : 003"  # scripted group (container) (typed FeaturePython)
  n = 1
  ref = W_element
FEATURE [App::DocumentObjectGroupPython] F_element017  label="F_element : 6"  # scripted group (container) (typed FeaturePython)
  n = 6
  ref = F_element
FEATURE [App::DocumentObjectGroupPython] G4_TUNGSTEN_HEXAFLUORIDE  # scripted group (container) (typed FeaturePython)
  Dunit = g/cm3
  Dvalue = 2.4
  Group = -> [W_element003,F_element017]
  conduct = 2
  density = 1
  expand = 3
  formula = G4_TUNGSTEN_HEXAFLUORIDE
  name = G4_TUNGSTEN_HEXAFLUORIDE
  specific = 4
FEATURE [App::DocumentObjectGroupPython] U_element001  label="U_element : 1"  # scripted group (container) (typed FeaturePython)
  n = 1
  ref = U_element
FEATURE [App::DocumentObjectGroupPython] C_element117  label="C_element : 064"  # scripted group (container) (typed FeaturePython)
  n = 2
  ref = C_element
FEATURE [App::DocumentObjectGroupPython] G4_URANIUM_DICARBIDE  # scripted group (container) (typed FeaturePython)
  Dunit = g/cm3
  Dvalue = 11.28
  Group = -> [U_element001,C_element117]
  conduct = 2
  density = 1
  expand = 3
  formula = G4_URANIUM_DICARBIDE
  name = G4_URANIUM_DICARBIDE
  specific = 4
FEATURE [App::DocumentObjectGroupPython] U_element002  label="U_element : 002"  # scripted group (container) (typed FeaturePython)
  n = 1
  ref = U_element
FEATURE [App::DocumentObjectGroupPython] C_element118  label="C_element : 065"  # scripted group (container) (typed FeaturePython)
  n = 1
  ref = C_element
FEATURE [App::DocumentObjectGroupPython] G4_URANIUM_MONOCARBIDE  # scripted group (container) (typed FeaturePython)
  Dunit = g/cm3
  Dvalue = 13.63
  Group = -> [U_element002,C_element118]
  conduct = 2
  density = 1
  expand = 3
  formula = G4_URANIUM_MONOCARBIDE
  name = G4_URANIUM_MONOCARBIDE
  specific = 4
FEATURE [App::DocumentObjectGroupPython] U_element003  label="U_element : 003"  # scripted group (container) (typed FeaturePython)
  n = 1
  ref = U_element
FEATURE [App::DocumentObjectGroupPython] O_element100  label="O_element : 054"  # scripted group (container) (typed FeaturePython)
  n = 2
  ref = O_element
FEATURE [App::DocumentObjectGroupPython] G4_URANIUM_OXIDE  # scripted group (container) (typed FeaturePython)
  Dunit = g/cm3
  Dvalue = 10.96
  Group = -> [U_element003,O_element100]
  conduct = 2
  density = 1
  expand = 3
  formula = G4_URANIUM_OXIDE
  name = G4_URANIUM_OXIDE
  specific = 4
FEATURE [App::DocumentObjectGroupPython] C_element119  label="C_element : 066"  # scripted group (container) (typed FeaturePython)
  n = 1
  ref = C_element
FEATURE [App::DocumentObjectGroupPython] H_element107  label="H_element : 057"  # scripted group (container) (typed FeaturePython)
  n = 4
  ref = H_element
FEATURE [App::DocumentObjectGroupPython] N_element046  label="N_element : 019"  # scripted group (container) (typed FeaturePython)
  n = 2
  ref = N_element
FEATURE [App::DocumentObjectGroupPython] O_element101  label="O_element : 055"  # scripted group (container) (typed FeaturePython)
  n = 1
  ref = O_element
FEATURE [App::DocumentObjectGroupPython] G4_UREA  # scripted group (container) (typed FeaturePython)
  Dunit = g/cm3
  Dvalue = 1.323
  Group = -> [C_element119,H_element107,N_element046,O_element101]
  conduct = 2
  density = 1
  expand = 3
  formula = G4_UREA
  name = G4_UREA
  specific = 4
FEATURE [App::DocumentObjectGroupPython] C_element120  label="C_element : 067"  # scripted group (container) (typed FeaturePython)
  n = 5
  ref = C_element
FEATURE [App::DocumentObjectGroupPython] H_element108  label="H_element : 058"  # scripted group (container) (typed FeaturePython)
  n = 11
  ref = H_element
FEATURE [App::DocumentObjectGroupPython] N_element047  label="N_element : 020"  # scripted group (container) (typed FeaturePython)
  n = 1
  ref = N_element
FEATURE [App::DocumentObjectGroupPython] O_element102  label="O_element : 056"  # scripted group (container) (typed FeaturePython)
  n = 2
  ref = O_element
FEATURE [App::DocumentObjectGroupPython] G4_VALINE  # scripted group (container) (typed FeaturePython)
  Dunit = g/cm3
  Dvalue = 1.23
  Group = -> [C_element120,H_element108,N_element047,O_element102]
  conduct = 2
  density = 1
  expand = 3
  formula = G4_VALINE
  name = G4_VALINE
  specific = 4
FEATURE [App::DocumentObjectGroupPython] H_element109  label="H_element : 0.009"  # scripted group (container) (typed FeaturePython)
  n = 0.009417
FEATURE [App::DocumentObjectGroupPython] C_element121  label="C_element : 0.281"  # scripted group (container) (typed FeaturePython)
  n = 0.280555
FEATURE [App::DocumentObjectGroupPython] F_element018  label="F_element : 0.710"  # scripted group (container) (typed FeaturePython)
  n = 0.710028
FEATURE [App::DocumentObjectGroupPython] G4_VITON  # scripted group (container) (typed FeaturePython)
  Dunit = g/cm3
  Dvalue = 1.8
  Group = -> [H_element109,C_element121,F_element018]
  conduct = 2
  density = 1
  expand = 3
  formula = G4_VITON
  name = G4_VITON
  specific = 4
FEATURE [App::DocumentObjectGroupPython] H_element110  label="H_element : 059"  # scripted group (container) (typed FeaturePython)
  n = 2
  ref = H_element
FEATURE [App::DocumentObjectGroupPython] O_element103  label="O_element : 057"  # scripted group (container) (typed FeaturePython)
  n = 1
  ref = O_element
FEATURE [App::DocumentObjectGroupPython] G4_WATER  # scripted group (container) (typed FeaturePython)
  Dunit = g/cm3
  Dvalue = 1
  Group = -> [H_element110,O_element103]
  conduct = 2
  density = 1
  expand = 3
  formula = G4_WATER
  name = G4_WATER
  specific = 4
FEATURE [App::DocumentObjectGroupPython] H_element111  label="H_element : 060"  # scripted group (container) (typed FeaturePython)
  n = 2
  ref = H_element
FEATURE [App::DocumentObjectGroupPython] O_element104  label="O_element : 058"  # scripted group (container) (typed FeaturePython)
  n = 1
  ref = O_element
FEATURE [App::DocumentObjectGroupPython] G4_WATER_VAPOR  # scripted group (container) (typed FeaturePython)
  Dunit = g/cm3
  Dvalue = 0.000756182
  Group = -> [H_element111,O_element104]
  conduct = 2
  density = 1
  expand = 3
  formula = G4_WATER_VAPOR
  name = G4_WATER_VAPOR
  specific = 4
FEATURE [App::DocumentObjectGroupPython] C_element122  label="C_element : 068"  # scripted group (container) (typed FeaturePython)
  n = 8
  ref = C_element
FEATURE [App::DocumentObjectGroupPython] H_element112  label="H_element : 061"  # scripted group (container) (typed FeaturePython)
  n = 10
  ref = H_element
FEATURE [App::DocumentObjectGroupPython] G4_XYLENE  # scripted group (container) (typed FeaturePython)
  Dunit = g/cm3
  Dvalue = 0.87
  Group = -> [C_element122,H_element112]
  conduct = 2
  density = 1
  expand = 3
  formula = G4_XYLENE
  name = G4_XYLENE
  specific = 4
FEATURE [App::DocumentObjectGroupPython] C_element123  label="C_element : 069"  # scripted group (container) (typed FeaturePython)
  n = 1
  ref = C_element
FEATURE [App::DocumentObjectGroupPython] G4_GRAPHITE  # scripted group (container) (typed FeaturePython)
  Dunit = g/cm3
  Dvalue = 2.21
  Group = -> [C_element123]
  conduct = 2
  density = 1
  expand = 3
  formula = G4_GRAPHITE
  name = G4_GRAPHITE
  specific = 4
FEATURE [App::DocumentObjectGroupPython] NIST  # scripted group (container) (typed FeaturePython)
  Group = -> [G4_A_150_TISSUE,G4_ACETONE,G4_ACETYLENE,G4_ADENINE,G4_ADIPOSE_TISSUE_ICRP,G4_AIR,G4_ALANINE,G4_ALUMINUM_OXIDE,G4_AMBER,G4_AMMONIA,G4_ANILINE,G4_ANTHRACENE,G4_B_100_BONE,G4_BAKELITE,G4_BARIUM_FLUORIDE,G4_BARIUM_SULFATE,G4_BENZENE,G4_BERYLLIUM_OXIDE,G4_BGO,G4_BLOOD_ICRP,G4_BONE_COMPACT_ICRU,G4_BONE_CORTICAL_ICRP,G4_BORON_CARBIDE,G4_BORON_OXIDE,G4_BRAIN_ICRP,G4_BUTANE,G4_N_BUTYL_ALCOHOL,G4_C_552,+152 more]
FEATURE [App::DocumentObjectGroupPython] H_element113  label="H_element : 062"  # scripted group (container) (typed FeaturePython)
  n = 1
  ref = H_element
FEATURE [App::DocumentObjectGroupPython] G4_H  # scripted group (container) (typed FeaturePython)
  Dunit = g/cm3
  Dvalue = 8.3748e-05
  Group = -> [H_element113]
  conduct = 2
  density = 1
  expand = 3
  formula = H
  name = G4_H
  specific = 4
FEATURE [App::DocumentObjectGroupPython] He_element001  label="He_element : 1"  # scripted group (container) (typed FeaturePython)
  n = 1
  ref = He_element
FEATURE [App::DocumentObjectGroupPython] G4_He  # scripted group (container) (typed FeaturePython)
  Dunit = g/cm3
  Dvalue = 0.000166322
  Group = -> [He_element001]
  conduct = 2
  density = 1
  expand = 3
  formula = He
  name = G4_He
  specific = 4
FEATURE [App::DocumentObjectGroupPython] Li_element008  label="Li_element : 008"  # scripted group (container) (typed FeaturePython)
  n = 1
  ref = Li_element
FEATURE [App::DocumentObjectGroupPython] G4_Li  # scripted group (container) (typed FeaturePython)
  Dunit = g/cm3
  Dvalue = 0.534
  Group = -> [Li_element008]
  conduct = 2
  density = 1
  expand = 3
  formula = Li
  name = G4_Li
  specific = 4
FEATURE [App::DocumentObjectGroupPython] Be_element002  label="Be_element : 002"  # scripted group (container) (typed FeaturePython)
  n = 1
  ref = Be_element
FEATURE [App::DocumentObjectGroupPython] G4_Be  # scripted group (container) (typed FeaturePython)
  Dunit = g/cm3
  Dvalue = 1.848
  Group = -> [Be_element002]
  conduct = 2
  density = 1
  expand = 3
  formula = Be
  name = G4_Be
  specific = 4
FEATURE [App::DocumentObjectGroupPython] B_element007  label="B_element : 007"  # scripted group (container) (typed FeaturePython)
  n = 1
  ref = B_element
FEATURE [App::DocumentObjectGroupPython] G4_B  # scripted group (container) (typed FeaturePython)
  Dunit = g/cm3
  Dvalue = 2.37
  Group = -> [B_element007]
  conduct = 2
  density = 1
  expand = 3
  formula = B
  name = G4_B
  specific = 4
FEATURE [App::DocumentObjectGroupPython] C_element124  label="C_element : 070"  # scripted group (container) (typed FeaturePython)
  n = 1
  ref = C_element
FEATURE [App::DocumentObjectGroupPython] G4_C  # scripted group (container) (typed FeaturePython)
  Dunit = g/cm3
  Dvalue = 2
  Group = -> [C_element124]
  conduct = 2
  density = 1
  expand = 3
  formula = C
  name = G4_C
  specific = 4
FEATURE [App::DocumentObjectGroupPython] N_element048  label="N_element : 021"  # scripted group (container) (typed FeaturePython)
  n = 1
  ref = N_element
FEATURE [App::DocumentObjectGroupPython] G4_N  # scripted group (container) (typed FeaturePython)
  Dunit = g/cm3
  Dvalue = 0.0011652
  Group = -> [N_element048]
  conduct = 2
  density = 1
  expand = 3
  formula = N
  name = G4_N
  specific = 4
FEATURE [App::DocumentObjectGroupPython] O_element105  label="O_element : 059"  # scripted group (container) (typed FeaturePython)
  n = 1
  ref = O_element
FEATURE [App::DocumentObjectGroupPython] G4_O  # scripted group (container) (typed FeaturePython)
  Dunit = g/cm3
  Dvalue = 0.00133151
  Group = -> [O_element105]
  conduct = 2
  density = 1
  expand = 3
  formula = O
  name = G4_O
  specific = 4
FEATURE [App::DocumentObjectGroupPython] F_element019  label="F_element : 008"  # scripted group (container) (typed FeaturePython)
  n = 1
  ref = F_element
FEATURE [App::DocumentObjectGroupPython] G4_F  # scripted group (container) (typed FeaturePython)
  Dunit = g/cm3
  Dvalue = 0.00158029
  Group = -> [F_element019]
  conduct = 2
  density = 1
  expand = 3
  formula = F
  name = G4_F
  specific = 4
FEATURE [App::DocumentObjectGroupPython] Ne_element001  label="Ne_element : 1"  # scripted group (container) (typed FeaturePython)
  n = 1
  ref = Ne_element
FEATURE [App::DocumentObjectGroupPython] G4_Ne  # scripted group (container) (typed FeaturePython)
  Dunit = g/cm3
  Dvalue = 0.000838505
  Group = -> [Ne_element001]
  conduct = 2
  density = 1
  expand = 3
  formula = Ne
  name = G4_Ne
  specific = 4
FEATURE [App::DocumentObjectGroupPython] Na_element020  label="Na_element : 005"  # scripted group (container) (typed FeaturePython)
  n = 1
  ref = Na_element
FEATURE [App::DocumentObjectGroupPython] G4_Na  # scripted group (container) (typed FeaturePython)
  Dunit = g/cm3
  Dvalue = 0.971
  Group = -> [Na_element020]
  conduct = 2
  density = 1
  expand = 3
  formula = Na
  name = G4_Na
  specific = 4
FEATURE [App::DocumentObjectGroupPython] Mg_element011  label="Mg_element : 005"  # scripted group (container) (typed FeaturePython)
  n = 1
  ref = Mg_element
FEATURE [App::DocumentObjectGroupPython] G4_Mg  # scripted group (container) (typed FeaturePython)
  Dunit = g/cm3
  Dvalue = 1.74
  Group = -> [Mg_element011]
  conduct = 2
  density = 1
  expand = 3
  formula = Mg
  name = G4_Mg
  specific = 4
FEATURE [App::DocumentObjectGroupPython] Al_element004  label="Al_element : 1"  # scripted group (container) (typed FeaturePython)
  n = 1
  ref = Al_element
FEATURE [App::DocumentObjectGroupPython] G4_Al  # scripted group (container) (typed FeaturePython)
  Dunit = g/cm3
  Dvalue = 2.699
  Group = -> [Al_element004]
  conduct = 2
  density = 1
  expand = 3
  formula = Al
  name = G4_Al
  specific = 4
FEATURE [App::DocumentObjectGroupPython] Si_element007  label="Si_element : 002"  # scripted group (container) (typed FeaturePython)
  n = 1
  ref = Si_element
FEATURE [App::DocumentObjectGroupPython] G4_Si  # scripted group (container) (typed FeaturePython)
  Dunit = g/cm3
  Dvalue = 2.33
  Group = -> [Si_element007]
  conduct = 2
  density = 1
  expand = 3
  formula = Si
  name = G4_Si
  specific = 4
FEATURE [App::DocumentObjectGroupPython] P_element013  label="P_element : 002"  # scripted group (container) (typed FeaturePython)
  n = 1
  ref = P_element
FEATURE [App::DocumentObjectGroupPython] G4_P  # scripted group (container) (typed FeaturePython)
  Dunit = g/cm3
  Dvalue = 2.2
  Group = -> [P_element013]
  conduct = 2
  density = 1
  expand = 3
  formula = P
  name = G4_P
  specific = 4
FEATURE [App::DocumentObjectGroupPython] S_element023  label="S_element : 007"  # scripted group (container) (typed FeaturePython)
  n = 1
  ref = S_element
FEATURE [App::DocumentObjectGroupPython] G4_S  # scripted group (container) (typed FeaturePython)
  Dunit = g/cm3
  Dvalue = 2
  Group = -> [S_element023]
  conduct = 2
  density = 1
  expand = 3
  formula = S
  name = G4_S
  specific = 4
FEATURE [App::DocumentObjectGroupPython] Cl_element029  label="Cl_element : 015"  # scripted group (container) (typed FeaturePython)
  n = 1
  ref = Cl_element
FEATURE [App::DocumentObjectGroupPython] G4_Cl  # scripted group (container) (typed FeaturePython)
  Dunit = g/cm3
  Dvalue = 0.00299473
  Group = -> [Cl_element029]
  conduct = 2
  density = 1
  expand = 3
  formula = Cl
  name = G4_Cl
  specific = 4
FEATURE [App::DocumentObjectGroupPython] Ar_element002  label="Ar_element : 1"  # scripted group (container) (typed FeaturePython)
  n = 1
  ref = Ar_element
FEATURE [App::DocumentObjectGroupPython] G4_Ar  # scripted group (container) (typed FeaturePython)
  Dunit = g/cm3
  Dvalue = 0.00166201
  Group = -> [Ar_element002]
  conduct = 2
  density = 1
  expand = 3
  formula = Ar
  name = G4_Ar
  specific = 4
FEATURE [App::DocumentObjectGroupPython] K_element013  label="K_element : 003"  # scripted group (container) (typed FeaturePython)
  n = 1
  ref = K_element
FEATURE [App::DocumentObjectGroupPython] G4_K  # scripted group (container) (typed FeaturePython)
  Dunit = g/cm3
  Dvalue = 0.862
  Group = -> [K_element013]
  conduct = 2
  density = 1
  expand = 3
  formula = K
  name = G4_K
  specific = 4
FEATURE [App::DocumentObjectGroupPython] Ca_element014  label="Ca_element : 007"  # scripted group (container) (typed FeaturePython)
  n = 1
  ref = Ca_element
FEATURE [App::DocumentObjectGroupPython] G4_Ca  # scripted group (container) (typed FeaturePython)
  Dunit = g/cm3
  Dvalue = 1.55
  Group = -> [Ca_element014]
  conduct = 2
  density = 1
  expand = 3
  formula = Ca
  name = G4_Ca
  specific = 4
FEATURE [App::DocumentObjectGroupPython] Sc_element001  label="Sc_element : 1"  # scripted group (container) (typed FeaturePython)
  n = 1
  ref = Sc_element
FEATURE [App::DocumentObjectGroupPython] G4_Sc  # scripted group (container) (typed FeaturePython)
  Dunit = g/cm3
  Dvalue = 2.989
  Group = -> [Sc_element001]
  conduct = 2
  density = 1
  expand = 3
  formula = Sc
  name = G4_Sc
  specific = 4
FEATURE [App::DocumentObjectGroupPython] Ti_element004  label="Ti_element : 002"  # scripted group (container) (typed FeaturePython)
  n = 1
  ref = Ti_element
FEATURE [App::DocumentObjectGroupPython] G4_Ti  # scripted group (container) (typed FeaturePython)
  Dunit = g/cm3
  Dvalue = 4.54
  Group = -> [Ti_element004]
  conduct = 2
  density = 1
  expand = 3
  formula = Ti
  name = G4_Ti
  specific = 4
FEATURE [App::DocumentObjectGroupPython] V_element001  label="V_element : 1"  # scripted group (container) (typed FeaturePython)
  n = 1
  ref = V_element
FEATURE [App::DocumentObjectGroupPython] G4_V  # scripted group (container) (typed FeaturePython)
  Dunit = g/cm3
  Dvalue = 6.11
  Group = -> [V_element001]
  conduct = 2
  density = 1
  expand = 3
  formula = V
  name = G4_V
  specific = 4
FEATURE [App::DocumentObjectGroupPython] Cr_element001  label="Cr_element : 1"  # scripted group (container) (typed FeaturePython)
  n = 1
  ref = Cr_element
FEATURE [App::DocumentObjectGroupPython] G4_Cr  # scripted group (container) (typed FeaturePython)
  Dunit = g/cm3
  Dvalue = 7.18
  Group = -> [Cr_element001]
  conduct = 2
  density = 1
  expand = 3
  formula = Cr
  name = G4_Cr
  specific = 4
FEATURE [App::DocumentObjectGroupPython] Mn_element001  label="Mn_element : 1"  # scripted group (container) (typed FeaturePython)
  n = 1
  ref = Mn_element
FEATURE [App::DocumentObjectGroupPython] G4_Mn  # scripted group (container) (typed FeaturePython)
  Dunit = g/cm3
  Dvalue = 7.44
  Group = -> [Mn_element001]
  conduct = 2
  density = 1
  expand = 3
  formula = Mn
  name = G4_Mn
  specific = 4
FEATURE [App::DocumentObjectGroupPython] Fe_element007  label="Fe_element : 004"  # scripted group (container) (typed FeaturePython)
  n = 1
  ref = Fe_element
FEATURE [App::DocumentObjectGroupPython] G4_Fe  # scripted group (container) (typed FeaturePython)
  Dunit = g/cm3
  Dvalue = 7.874
  Group = -> [Fe_element007]
  conduct = 2
  density = 1
  expand = 3
  formula = Fe
  name = G4_Fe
  specific = 4
FEATURE [App::DocumentObjectGroupPython] Co_element001  label="Co_element : 1"  # scripted group (container) (typed FeaturePython)
  n = 1
  ref = Co_element
FEATURE [App::DocumentObjectGroupPython] G4_Co  # scripted group (container) (typed FeaturePython)
  Dunit = g/cm3
  Dvalue = 8.9
  Group = -> [Co_element001]
  conduct = 2
  density = 1
  expand = 3
  formula = Co
  name = G4_Co
  specific = 4
FEATURE [App::DocumentObjectGroupPython] Ni_element001  label="Ni_element : 1"  # scripted group (container) (typed FeaturePython)
  n = 1
  ref = Ni_element
FEATURE [App::DocumentObjectGroupPython] G4_Ni  # scripted group (container) (typed FeaturePython)
  Dunit = g/cm3
  Dvalue = 8.902
  Group = -> [Ni_element001]
  conduct = 2
  density = 1
  expand = 3
  formula = Ni
  name = G4_Ni
  specific = 4
FEATURE [App::DocumentObjectGroupPython] Cu_element001  label="Cu_element : 1"  # scripted group (container) (typed FeaturePython)
  n = 1
  ref = Cu_element
FEATURE [App::DocumentObjectGroupPython] G4_Cu  # scripted group (container) (typed FeaturePython)
  Dunit = g/cm3
  Dvalue = 8.96
  Group = -> [Cu_element001]
  conduct = 2
  density = 1
  expand = 3
  formula = Cu
  name = G4_Cu
  specific = 4
FEATURE [App::DocumentObjectGroupPython] Zn_element001  label="Zn_element : 1"  # scripted group (container) (typed FeaturePython)
  n = 1
  ref = Zn_element
FEATURE [App::DocumentObjectGroupPython] G4_Zn  # scripted group (container) (typed FeaturePython)
  Dunit = g/cm3
  Dvalue = 7.133
  Group = -> [Zn_element001]
  conduct = 2
  density = 1
  expand = 3
  formula = Zn
  name = G4_Zn
  specific = 4
FEATURE [App::DocumentObjectGroupPython] Ga_element002  label="Ga_element : 002"  # scripted group (container) (typed FeaturePython)
  n = 1
  ref = Ga_element
FEATURE [App::DocumentObjectGroupPython] G4_Ga  # scripted group (container) (typed FeaturePython)
  Dunit = g/cm3
  Dvalue = 5.904
  Group = -> [Ga_element002]
  conduct = 2
  density = 1
  expand = 3
  formula = Ga
  name = G4_Ga
  specific = 4
FEATURE [App::DocumentObjectGroupPython] Ge_element002  label="Ge_element : 1"  # scripted group (container) (typed FeaturePython)
  n = 1
  ref = Ge_element
FEATURE [App::DocumentObjectGroupPython] G4_Ge  # scripted group (container) (typed FeaturePython)
  Dunit = g/cm3
  Dvalue = 5.323
  Group = -> [Ge_element002]
  conduct = 2
  density = 1
  expand = 3
  formula = Ge
  name = G4_Ge
  specific = 4
FEATURE [App::DocumentObjectGroupPython] As_element003  label="As_element : 002"  # scripted group (container) (typed FeaturePython)
  n = 1
  ref = As_element
FEATURE [App::DocumentObjectGroupPython] G4_As  # scripted group (container) (typed FeaturePython)
  Dunit = g/cm3
  Dvalue = 5.73
  Group = -> [As_element003]
  conduct = 2
  density = 1
  expand = 3
  formula = As
  name = G4_As
  specific = 4
FEATURE [App::DocumentObjectGroupPython] Se_element001  label="Se_element : 1"  # scripted group (container) (typed FeaturePython)
  n = 1
  ref = Se_element
FEATURE [App::DocumentObjectGroupPython] G4_Se  # scripted group (container) (typed FeaturePython)
  Dunit = g/cm3
  Dvalue = 4.5
  Group = -> [Se_element001]
  conduct = 2
  density = 1
  expand = 3
  formula = Se
  name = G4_Se
  specific = 4
FEATURE [App::DocumentObjectGroupPython] Br_element007  label="Br_element : 004"  # scripted group (container) (typed FeaturePython)
  n = 1
  ref = Br_element
FEATURE [App::DocumentObjectGroupPython] G4_Br  # scripted group (container) (typed FeaturePython)
  Dunit = g/cm3
  Dvalue = 0.0070721
  Group = -> [Br_element007]
  conduct = 2
  density = 1
  expand = 3
  formula = Br
  name = G4_Br
  specific = 4
FEATURE [App::DocumentObjectGroupPython] Kr_element001  label="Kr_element : 1"  # scripted group (container) (typed FeaturePython)
  n = 1
  ref = Kr_element
FEATURE [App::DocumentObjectGroupPython] G4_Kr  # scripted group (container) (typed FeaturePython)
  Dunit = g/cm3
  Dvalue = 0.00347832
  Group = -> [Kr_element001]
  conduct = 2
  density = 1
  expand = 3
  formula = Kr
  name = G4_Kr
  specific = 4
FEATURE [App::DocumentObjectGroupPython] Rb_element001  label="Rb_element : 1"  # scripted group (container) (typed FeaturePython)
  n = 1
  ref = Rb_element
FEATURE [App::DocumentObjectGroupPython] G4_Rb  # scripted group (container) (typed FeaturePython)
  Dunit = g/cm3
  Dvalue = 1.532
  Group = -> [Rb_element001]
  conduct = 2
  density = 1
  expand = 3
  formula = Rb
  name = G4_Rb
  specific = 4
FEATURE [App::DocumentObjectGroupPython] Sr_element001  label="Sr_element : 1"  # scripted group (container) (typed FeaturePython)
  n = 1
  ref = Sr_element
FEATURE [App::DocumentObjectGroupPython] G4_Sr  # scripted group (container) (typed FeaturePython)
  Dunit = g/cm3
  Dvalue = 2.54
  Group = -> [Sr_element001]
  conduct = 2
  density = 1
  expand = 3
  formula = Sr
  name = G4_Sr
  specific = 4
FEATURE [App::DocumentObjectGroupPython] Y_element001  label="Y_element : 1"  # scripted group (container) (typed FeaturePython)
  n = 1
  ref = Y_element
FEATURE [App::DocumentObjectGroupPython] G4_Y  # scripted group (container) (typed FeaturePython)
  Dunit = g/cm3
  Dvalue = 4.469
  Group = -> [Y_element001]
  conduct = 2
  density = 1
  expand = 3
  formula = Y
  name = G4_Y
  specific = 4
FEATURE [App::DocumentObjectGroupPython] Zr_element001  label="Zr_element : 1"  # scripted group (container) (typed FeaturePython)
  n = 1
  ref = Zr_element
FEATURE [App::DocumentObjectGroupPython] G4_Zr  # scripted group (container) (typed FeaturePython)
  Dunit = g/cm3
  Dvalue = 6.506
  Group = -> [Zr_element001]
  conduct = 2
  density = 1
  expand = 3
  formula = Zr
  name = G4_Zr
  specific = 4
FEATURE [App::DocumentObjectGroupPython] Nb_element001  label="Nb_element : 1"  # scripted group (container) (typed FeaturePython)
  n = 1
  ref = Nb_element
FEATURE [App::DocumentObjectGroupPython] G4_Nb  # scripted group (container) (typed FeaturePython)
  Dunit = g/cm3
  Dvalue = 8.57
  Group = -> [Nb_element001]
  conduct = 2
  density = 1
  expand = 3
  formula = Nb
  name = G4_Nb
  specific = 4
FEATURE [App::DocumentObjectGroupPython] Mo_element001  label="Mo_element : 1"  # scripted group (container) (typed FeaturePython)
  n = 1
  ref = Mo_element
FEATURE [App::DocumentObjectGroupPython] G4_Mo  # scripted group (container) (typed FeaturePython)
  Dunit = g/cm3
  Dvalue = 10.22
  Group = -> [Mo_element001]
  conduct = 2
  density = 1
  expand = 3
  formula = Mo
  name = G4_Mo
  specific = 4
FEATURE [App::DocumentObjectGroupPython] Tc_element001  label="Tc_element : 1"  # scripted group (container) (typed FeaturePython)
  n = 1
  ref = Tc_element
FEATURE [App::DocumentObjectGroupPython] G4_Tc  # scripted group (container) (typed FeaturePython)
  Dunit = g/cm3
  Dvalue = 11.5
  Group = -> [Tc_element001]
  conduct = 2
  density = 1
  expand = 3
  formula = Tc
  name = G4_Tc
  specific = 4
FEATURE [App::DocumentObjectGroupPython] Ru_element001  label="Ru_element : 1"  # scripted group (container) (typed FeaturePython)
  n = 1
  ref = Ru_element
FEATURE [App::DocumentObjectGroupPython] G4_Ru  # scripted group (container) (typed FeaturePython)
  Dunit = g/cm3
  Dvalue = 12.41
  Group = -> [Ru_element001]
  conduct = 2
  density = 1
  expand = 3
  formula = Ru
  name = G4_Ru
  specific = 4
FEATURE [App::DocumentObjectGroupPython] Rh_element001  label="Rh_element : 1"  # scripted group (container) (typed FeaturePython)
  n = 1
  ref = Rh_element
FEATURE [App::DocumentObjectGroupPython] G4_Rh  # scripted group (container) (typed FeaturePython)
  Dunit = g/cm3
  Dvalue = 12.41
  Group = -> [Rh_element001]
  conduct = 2
  density = 1
  expand = 3
  formula = Rh
  name = G4_Rh
  specific = 4
FEATURE [App::DocumentObjectGroupPython] Pd_element001  label="Pd_element : 1"  # scripted group (container) (typed FeaturePython)
  n = 1
  ref = Pd_element
FEATURE [App::DocumentObjectGroupPython] G4_Pd  # scripted group (container) (typed FeaturePython)
  Dunit = g/cm3
  Dvalue = 12.02
  Group = -> [Pd_element001]
  conduct = 2
  density = 1
  expand = 3
  formula = Pd
  name = G4_Pd
  specific = 4
FEATURE [App::DocumentObjectGroupPython] Ag_element006  label="Ag_element : 004"  # scripted group (container) (typed FeaturePython)
  n = 1
  ref = Ag_element
FEATURE [App::DocumentObjectGroupPython] G4_Ag  # scripted group (container) (typed FeaturePython)
  Dunit = g/cm3
  Dvalue = 10.5
  Group = -> [Ag_element006]
  conduct = 2
  density = 1
  expand = 3
  formula = Ag
  name = G4_Ag
  specific = 4
FEATURE [App::DocumentObjectGroupPython] Cd_element003  label="Cd_element : 003"  # scripted group (container) (typed FeaturePython)
  n = 1
  ref = Cd_element
FEATURE [App::DocumentObjectGroupPython] G4_Cd  # scripted group (container) (typed FeaturePython)
  Dunit = g/cm3
  Dvalue = 8.65
  Group = -> [Cd_element003]
  conduct = 2
  density = 1
  expand = 3
  formula = Cd
  name = G4_Cd
  specific = 4
FEATURE [App::DocumentObjectGroupPython] In_element001  label="In_element : 1"  # scripted group (container) (typed FeaturePython)
  n = 1
  ref = In_element
FEATURE [App::DocumentObjectGroupPython] G4_In  # scripted group (container) (typed FeaturePython)
  Dunit = g/cm3
  Dvalue = 7.31
  Group = -> [In_element001]
  conduct = 2
  density = 1
  expand = 3
  formula = In
  name = G4_In
  specific = 4
FEATURE [App::DocumentObjectGroupPython] Sn_element001  label="Sn_element : 1"  # scripted group (container) (typed FeaturePython)
  n = 1
  ref = Sn_element
FEATURE [App::DocumentObjectGroupPython] G4_Sn  # scripted group (container) (typed FeaturePython)
  Dunit = g/cm3
  Dvalue = 7.31
  Group = -> [Sn_element001]
  conduct = 2
  density = 1
  expand = 3
  formula = Sn
  name = G4_Sn
  specific = 4
FEATURE [App::DocumentObjectGroupPython] Sb_element001  label="Sb_element : 1"  # scripted group (container) (typed FeaturePython)
  n = 1
  ref = Sb_element
FEATURE [App::DocumentObjectGroupPython] G4_Sb  # scripted group (container) (typed FeaturePython)
  Dunit = g/cm3
  Dvalue = 6.691
  Group = -> [Sb_element001]
  conduct = 2
  density = 1
  expand = 3
  formula = Sb
  name = G4_Sb
  specific = 4
FEATURE [App::DocumentObjectGroupPython] Te_element002  label="Te_element : 002"  # scripted group (container) (typed FeaturePython)
  n = 1
  ref = Te_element
FEATURE [App::DocumentObjectGroupPython] G4_Te  # scripted group (container) (typed FeaturePython)
  Dunit = g/cm3
  Dvalue = 6.24
  Group = -> [Te_element002]
  conduct = 2
  density = 1
  expand = 3
  formula = Te
  name = G4_Te
  specific = 4
FEATURE [App::DocumentObjectGroupPython] I_element010  label="I_element : 006"  # scripted group (container) (typed FeaturePython)
  n = 1
  ref = I_element
FEATURE [App::DocumentObjectGroupPython] G4_I  # scripted group (container) (typed FeaturePython)
  Dunit = g/cm3
  Dvalue = 4.93
  Group = -> [I_element010]
  conduct = 2
  density = 1
  expand = 3
  formula = I
  name = G4_I
  specific = 4
FEATURE [App::DocumentObjectGroupPython] Xe_element001  label="Xe_element : 1"  # scripted group (container) (typed FeaturePython)
  n = 1
  ref = Xe_element
FEATURE [App::DocumentObjectGroupPython] G4_Xe  # scripted group (container) (typed FeaturePython)
  Dunit = g/cm3
  Dvalue = 0.00548536
  Group = -> [Xe_element001]
  conduct = 2
  density = 1
  expand = 3
  formula = Xe
  name = G4_Xe
  specific = 4
FEATURE [App::DocumentObjectGroupPython] Cs_element003  label="Cs_element : 003"  # scripted group (container) (typed FeaturePython)
  n = 1
  ref = Cs_element
FEATURE [App::DocumentObjectGroupPython] G4_Cs  # scripted group (container) (typed FeaturePython)
  Dunit = g/cm3
  Dvalue = 1.873
  Group = -> [Cs_element003]
  conduct = 2
  density = 1
  expand = 3
  formula = Cs
  name = G4_Cs
  specific = 4
FEATURE [App::DocumentObjectGroupPython] Ba_element003  label="Ba_element : 003"  # scripted group (container) (typed FeaturePython)
  n = 1
  ref = Ba_element
FEATURE [App::DocumentObjectGroupPython] G4_Ba  # scripted group (container) (typed FeaturePython)
  Dunit = g/cm3
  Dvalue = 3.5
  Group = -> [Ba_element003]
  conduct = 2
  density = 1
  expand = 3
  formula = Ba
  name = G4_Ba
  specific = 4
FEATURE [App::DocumentObjectGroupPython] La_element003  label="La_element : 003"  # scripted group (container) (typed FeaturePython)
  n = 1
  ref = La_element
FEATURE [App::DocumentObjectGroupPython] G4_La  # scripted group (container) (typed FeaturePython)
  Dunit = g/cm3
  Dvalue = 6.154
  Group = -> [La_element003]
  conduct = 2
  density = 1
  expand = 3
  formula = La
  name = G4_La
  specific = 4
FEATURE [App::DocumentObjectGroupPython] Ce_element002  label="Ce_element : 1"  # scripted group (container) (typed FeaturePython)
  n = 1
  ref = Ce_element
FEATURE [App::DocumentObjectGroupPython] G4_Ce  # scripted group (container) (typed FeaturePython)
  Dunit = g/cm3
  Dvalue = 6.657
  Group = -> [Ce_element002]
  conduct = 2
  density = 1
  expand = 3
  formula = Ce
  name = G4_Ce
  specific = 4
FEATURE [App::DocumentObjectGroupPython] Pr_element001  label="Pr_element : 1"  # scripted group (container) (typed FeaturePython)
  n = 1
  ref = Pr_element
FEATURE [App::DocumentObjectGroupPython] G4_Pr  # scripted group (container) (typed FeaturePython)
  Dunit = g/cm3
  Dvalue = 6.71
  Group = -> [Pr_element001]
  conduct = 2
  density = 1
  expand = 3
  formula = Pr
  name = G4_Pr
  specific = 4
FEATURE [App::DocumentObjectGroupPython] Nd_element001  label="Nd_element : 1"  # scripted group (container) (typed FeaturePython)
  n = 1
  ref = Nd_element
FEATURE [App::DocumentObjectGroupPython] G4_Nd  # scripted group (container) (typed FeaturePython)
  Dunit = g/cm3
  Dvalue = 6.9
  Group = -> [Nd_element001]
  conduct = 2
  density = 1
  expand = 3
  formula = Nd
  name = G4_Nd
  specific = 4
FEATURE [App::DocumentObjectGroupPython] Pm_element001  label="Pm_element : 1"  # scripted group (container) (typed FeaturePython)
  n = 1
  ref = Pm_element
FEATURE [App::DocumentObjectGroupPython] G4_Pm  # scripted group (container) (typed FeaturePython)
  Dunit = g/cm3
  Dvalue = 7.22
  Group = -> [Pm_element001]
  conduct = 2
  density = 1
  expand = 3
  formula = Pm
  name = G4_Pm
  specific = 4
FEATURE [App::DocumentObjectGroupPython] Sm_element001  label="Sm_element : 1"  # scripted group (container) (typed FeaturePython)
  n = 1
  ref = Sm_element
FEATURE [App::DocumentObjectGroupPython] G4_Sm  # scripted group (container) (typed FeaturePython)
  Dunit = g/cm3
  Dvalue = 7.46
  Group = -> [Sm_element001]
  conduct = 2
  density = 1
  expand = 3
  formula = Sm
  name = G4_Sm
  specific = 4
FEATURE [App::DocumentObjectGroupPython] Eu_element001  label="Eu_element : 1"  # scripted group (container) (typed FeaturePython)
  n = 1
  ref = Eu_element
FEATURE [App::DocumentObjectGroupPython] G4_Eu  # scripted group (container) (typed FeaturePython)
  Dunit = g/cm3
  Dvalue = 5.243
  Group = -> [Eu_element001]
  conduct = 2
  density = 1
  expand = 3
  formula = Eu
  name = G4_Eu
  specific = 4
FEATURE [App::DocumentObjectGroupPython] Gd_element002  label="Gd_element : 1"  # scripted group (container) (typed FeaturePython)
  n = 1
  ref = Gd_element
FEATURE [App::DocumentObjectGroupPython] G4_Gd  # scripted group (container) (typed FeaturePython)
  Dunit = g/cm3
  Dvalue = 7.9004
  Group = -> [Gd_element002]
  conduct = 2
  density = 1
  expand = 3
  formula = Gd
  name = G4_Gd
  specific = 4
FEATURE [App::DocumentObjectGroupPython] Tb_element001  label="Tb_element : 1"  # scripted group (container) (typed FeaturePython)
  n = 1
  ref = Tb_element
FEATURE [App::DocumentObjectGroupPython] G4_Tb  # scripted group (container) (typed FeaturePython)
  Dunit = g/cm3
  Dvalue = 8.229
  Group = -> [Tb_element001]
  conduct = 2
  density = 1
  expand = 3
  formula = Tb
  name = G4_Tb
  specific = 4
FEATURE [App::DocumentObjectGroupPython] Dy_element001  label="Dy_element : 1"  # scripted group (container) (typed FeaturePython)
  n = 1
  ref = Dy_element
FEATURE [App::DocumentObjectGroupPython] G4_Dy  # scripted group (container) (typed FeaturePython)
  Dunit = g/cm3
  Dvalue = 8.55
  Group = -> [Dy_element001]
  conduct = 2
  density = 1
  expand = 3
  formula = Dy
  name = G4_Dy
  specific = 4
FEATURE [App::DocumentObjectGroupPython] Ho_element001  label="Ho_element : 1"  # scripted group (container) (typed FeaturePython)
  n = 1
  ref = Ho_element
FEATURE [App::DocumentObjectGroupPython] G4_Ho  # scripted group (container) (typed FeaturePython)
  Dunit = g/cm3
  Dvalue = 8.795
  Group = -> [Ho_element001]
  conduct = 2
  density = 1
  expand = 3
  formula = Ho
  name = G4_Ho
  specific = 4
FEATURE [App::DocumentObjectGroupPython] Er_element001  label="Er_element : 1"  # scripted group (container) (typed FeaturePython)
  n = 1
  ref = Er_element
FEATURE [App::DocumentObjectGroupPython] G4_Er  # scripted group (container) (typed FeaturePython)
  Dunit = g/cm3
  Dvalue = 9.066
  Group = -> [Er_element001]
  conduct = 2
  density = 1
  expand = 3
  formula = Er
  name = G4_Er
  specific = 4
FEATURE [App::DocumentObjectGroupPython] Tm_element001  label="Tm_element : 1"  # scripted group (container) (typed FeaturePython)
  n = 1
  ref = Tm_element
FEATURE [App::DocumentObjectGroupPython] G4_Tm  # scripted group (container) (typed FeaturePython)
  Dunit = g/cm3
  Dvalue = 9.321
  Group = -> [Tm_element001]
  conduct = 2
  density = 1
  expand = 3
  formula = Tm
  name = G4_Tm
  specific = 4
FEATURE [App::DocumentObjectGroupPython] Yb_element001  label="Yb_element : 1"  # scripted group (container) (typed FeaturePython)
  n = 1
  ref = Yb_element
FEATURE [App::DocumentObjectGroupPython] G4_Yb  # scripted group (container) (typed FeaturePython)
  Dunit = g/cm3
  Dvalue = 6.73
  Group = -> [Yb_element001]
  conduct = 2
  density = 1
  expand = 3
  formula = Yb
  name = G4_Yb
  specific = 4
FEATURE [App::DocumentObjectGroupPython] Lu_element001  label="Lu_element : 1"  # scripted group (container) (typed FeaturePython)
  n = 1
  ref = Lu_element
FEATURE [App::DocumentObjectGroupPython] G4_Lu  # scripted group (container) (typed FeaturePython)
  Dunit = g/cm3
  Dvalue = 9.84
  Group = -> [Lu_element001]
  conduct = 2
  density = 1
  expand = 3
  formula = Lu
  name = G4_Lu
  specific = 4
FEATURE [App::DocumentObjectGroupPython] Hf_element001  label="Hf_element : 1"  # scripted group (container) (typed FeaturePython)
  n = 1
  ref = Hf_element
FEATURE [App::DocumentObjectGroupPython] G4_Hf  # scripted group (container) (typed FeaturePython)
  Dunit = g/cm3
  Dvalue = 13.31
  Group = -> [Hf_element001]
  conduct = 2
  density = 1
  expand = 3
  formula = Hf
  name = G4_Hf
  specific = 4
FEATURE [App::DocumentObjectGroupPython] Ta_element001  label="Ta_element : 1"  # scripted group (container) (typed FeaturePython)
  n = 1
  ref = Ta_element
FEATURE [App::DocumentObjectGroupPython] G4_Ta  # scripted group (container) (typed FeaturePython)
  Dunit = g/cm3
  Dvalue = 16.654
  Group = -> [Ta_element001]
  conduct = 2
  density = 1
  expand = 3
  formula = Ta
  name = G4_Ta
  specific = 4
FEATURE [App::DocumentObjectGroupPython] W_element004  label="W_element : 004"  # scripted group (container) (typed FeaturePython)
  n = 1
  ref = W_element
FEATURE [App::DocumentObjectGroupPython] G4_W  # scripted group (container) (typed FeaturePython)
  Dunit = g/cm3
  Dvalue = 19.3
  Group = -> [W_element004]
  conduct = 2
  density = 1
  expand = 3
  formula = W
  name = G4_W
  specific = 4
FEATURE [App::DocumentObjectGroupPython] Re_element001  label="Re_element : 1"  # scripted group (container) (typed FeaturePython)
  n = 1
  ref = Re_element
FEATURE [App::DocumentObjectGroupPython] G4_Re  # scripted group (container) (typed FeaturePython)
  Dunit = g/cm3
  Dvalue = 21.02
  Group = -> [Re_element001]
  conduct = 2
  density = 1
  expand = 3
  formula = Re
  name = G4_Re
  specific = 4
FEATURE [App::DocumentObjectGroupPython] Os_element001  label="Os_element : 1"  # scripted group (container) (typed FeaturePython)
  n = 1
  ref = Os_element
FEATURE [App::DocumentObjectGroupPython] G4_Os  # scripted group (container) (typed FeaturePython)
  Dunit = g/cm3
  Dvalue = 22.57
  Group = -> [Os_element001]
  conduct = 2
  density = 1
  expand = 3
  formula = Os
  name = G4_Os
  specific = 4
FEATURE [App::DocumentObjectGroupPython] Ir_element001  label="Ir_element : 1"  # scripted group (container) (typed FeaturePython)
  n = 1
  ref = Ir_element
FEATURE [App::DocumentObjectGroupPython] G4_Ir  # scripted group (container) (typed FeaturePython)
  Dunit = g/cm3
  Dvalue = 22.42
  Group = -> [Ir_element001]
  conduct = 2
  density = 1
  expand = 3
  formula = Ir
  name = G4_Ir
  specific = 4
FEATURE [App::DocumentObjectGroupPython] Pt_element001  label="Pt_element : 1"  # scripted group (container) (typed FeaturePython)
  n = 1
  ref = Pt_element
FEATURE [App::DocumentObjectGroupPython] G4_Pt  # scripted group (container) (typed FeaturePython)
  Dunit = g/cm3
  Dvalue = 21.45
  Group = -> [Pt_element001]
  conduct = 2
  density = 1
  expand = 3
  formula = Pt
  name = G4_Pt
  specific = 4
FEATURE [App::DocumentObjectGroupPython] Au_element001  label="Au_element : 1"  # scripted group (container) (typed FeaturePython)
  n = 1
  ref = Au_element
FEATURE [App::DocumentObjectGroupPython] G4_Au  # scripted group (container) (typed FeaturePython)
  Dunit = g/cm3
  Dvalue = 19.32
  Group = -> [Au_element001]
  conduct = 2
  density = 1
  expand = 3
  formula = Au
  name = G4_Au
  specific = 4
FEATURE [App::DocumentObjectGroupPython] Hg_element002  label="Hg_element : 002"  # scripted group (container) (typed FeaturePython)
  n = 1
  ref = Hg_element
FEATURE [App::DocumentObjectGroupPython] G4_Hg  # scripted group (container) (typed FeaturePython)
  Dunit = g/cm3
  Dvalue = 13.546
  Group = -> [Hg_element002]
  conduct = 2
  density = 1
  expand = 3
  formula = Hg
  name = G4_Hg
  specific = 4
FEATURE [App::DocumentObjectGroupPython] Tl_element002  label="Tl_element : 002"  # scripted group (container) (typed FeaturePython)
  n = 1
  ref = Tl_element
FEATURE [App::DocumentObjectGroupPython] G4_Tl  # scripted group (container) (typed FeaturePython)
  Dunit = g/cm3
  Dvalue = 11.72
  Group = -> [Tl_element002]
  conduct = 2
  density = 1
  expand = 3
  formula = Tl
  name = G4_Tl
  specific = 4
FEATURE [App::DocumentObjectGroupPython] Pb_element003  label="Pb_element : 1"  # scripted group (container) (typed FeaturePython)
  n = 1
  ref = Pb_element
FEATURE [App::DocumentObjectGroupPython] G4_Pb  # scripted group (container) (typed FeaturePython)
  Dunit = g/cm3
  Dvalue = 11.35
  Group = -> [Pb_element003]
  conduct = 2
  density = 1
  expand = 3
  formula = Pb
  name = G4_Pb
  specific = 4
FEATURE [App::DocumentObjectGroupPython] Bi_element002  label="Bi_element : 1"  # scripted group (container) (typed FeaturePython)
  n = 1
  ref = Bi_element
FEATURE [App::DocumentObjectGroupPython] G4_Bi  # scripted group (container) (typed FeaturePython)
  Dunit = g/cm3
  Dvalue = 9.747
  Group = -> [Bi_element002]
  conduct = 2
  density = 1
  expand = 3
  formula = Bi
  name = G4_Bi
  specific = 4
FEATURE [App::DocumentObjectGroupPython] Po_element001  label="Po_element : 1"  # scripted group (container) (typed FeaturePython)
  n = 1
  ref = Po_element
FEATURE [App::DocumentObjectGroupPython] G4_Po  # scripted group (container) (typed FeaturePython)
  Dunit = g/cm3
  Dvalue = 9.32
  Group = -> [Po_element001]
  conduct = 2
  density = 1
  expand = 3
  formula = Po
  name = G4_Po
  specific = 4
FEATURE [App::DocumentObjectGroupPython] At_element001  label="At_element : 1"  # scripted group (container) (typed FeaturePython)
  n = 1
  ref = At_element
FEATURE [App::DocumentObjectGroupPython] G4_At  # scripted group (container) (typed FeaturePython)
  Dunit = g/cm3
  Dvalue = 9.32
  Group = -> [At_element001]
  conduct = 2
  density = 1
  expand = 3
  formula = At
  name = G4_At
  specific = 4
FEATURE [App::DocumentObjectGroupPython] Rn_element001  label="Rn_element : 1"  # scripted group (container) (typed FeaturePython)
  n = 1
  ref = Rn_element
FEATURE [App::DocumentObjectGroupPython] G4_Rn  # scripted group (container) (typed FeaturePython)
  Dunit = g/cm3
  Dvalue = 0.00900662
  Group = -> [Rn_element001]
  conduct = 2
  density = 1
  expand = 3
  formula = Rn
  name = G4_Rn
  specific = 4
FEATURE [App::DocumentObjectGroupPython] Fr_element001  label="Fr_element : 1"  # scripted group (container) (typed FeaturePython)
  n = 1
  ref = Fr_element
FEATURE [App::DocumentObjectGroupPython] G4_Fr  # scripted group (container) (typed FeaturePython)
  Dunit = g/cm3
  Dvalue = 1
  Group = -> [Fr_element001]
  conduct = 2
  density = 1
  expand = 3
  formula = Fr
  name = G4_Fr
  specific = 4
FEATURE [App::DocumentObjectGroupPython] Ra_element001  label="Ra_element : 1"  # scripted group (container) (typed FeaturePython)
  n = 1
  ref = Ra_element
FEATURE [App::DocumentObjectGroupPython] G4_Ra  # scripted group (container) (typed FeaturePython)
  Dunit = g/cm3
  Dvalue = 5
  Group = -> [Ra_element001]
  conduct = 2
  density = 1
  expand = 3
  formula = Ra
  name = G4_Ra
  specific = 4
FEATURE [App::DocumentObjectGroupPython] Ac_element001  label="Ac_element : 1"  # scripted group (container) (typed FeaturePython)
  n = 1
  ref = Ac_element
FEATURE [App::DocumentObjectGroupPython] G4_Ac  # scripted group (container) (typed FeaturePython)
  Dunit = g/cm3
  Dvalue = 10.07
  Group = -> [Ac_element001]
  conduct = 2
  density = 1
  expand = 3
  formula = Ac
  name = G4_Ac
  specific = 4
FEATURE [App::DocumentObjectGroupPython] Th_element001  label="Th_element : 1"  # scripted group (container) (typed FeaturePython)
  n = 1
  ref = Th_element
FEATURE [App::DocumentObjectGroupPython] G4_Th  # scripted group (container) (typed FeaturePython)
  Dunit = g/cm3
  Dvalue = 11.72
  Group = -> [Th_element001]
  conduct = 2
  density = 1
  expand = 3
  formula = Th
  name = G4_Th
  specific = 4
FEATURE [App::DocumentObjectGroupPython] Pa_element001  label="Pa_element : 1"  # scripted group (container) (typed FeaturePython)
  n = 1
  ref = Pa_element
FEATURE [App::DocumentObjectGroupPython] G4_Pa  # scripted group (container) (typed FeaturePython)
  Dunit = g/cm3
  Dvalue = 15.37
  Group = -> [Pa_element001]
  conduct = 2
  density = 1
  expand = 3
  formula = Pa
  name = G4_Pa
  specific = 4
FEATURE [App::DocumentObjectGroupPython] U_element004  label="U_element : 004"  # scripted group (container) (typed FeaturePython)
  n = 1
  ref = U_element
FEATURE [App::DocumentObjectGroupPython] G4_U  # scripted group (container) (typed FeaturePython)
  Dunit = g/cm3
  Dvalue = 18.95
  Group = -> [U_element004]
  conduct = 2
  density = 1
  expand = 3
  formula = U
  name = G4_U
  specific = 4
FEATURE [App::DocumentObjectGroupPython] Np_element001  label="Np_element : 1"  # scripted group (container) (typed FeaturePython)
  n = 1
  ref = Np_element
FEATURE [App::DocumentObjectGroupPython] G4_Np  # scripted group (container) (typed FeaturePython)
  Dunit = g/cm3
  Dvalue = 20.25
  Group = -> [Np_element001]
  conduct = 2
  density = 1
  expand = 3
  formula = Np
  name = G4_Np
  specific = 4
FEATURE [App::DocumentObjectGroupPython] Pu_element002  label="Pu_element : 002"  # scripted group (container) (typed FeaturePython)
  n = 1
  ref = Pu_element
FEATURE [App::DocumentObjectGroupPython] G4_Pu  # scripted group (container) (typed FeaturePython)
  Dunit = g/cm3
  Dvalue = 19.84
  Group = -> [Pu_element002]
  conduct = 2
  density = 1
  expand = 3
  formula = Pu
  name = G4_Pu
  specific = 4
FEATURE [App::DocumentObjectGroupPython] Am_element001  label="Am_element : 1"  # scripted group (container) (typed FeaturePython)
  n = 1
  ref = Am_element
FEATURE [App::DocumentObjectGroupPython] G4_Am  # scripted group (container) (typed FeaturePython)
  Dunit = g/cm3
  Dvalue = 13.67
  Group = -> [Am_element001]
  conduct = 2
  density = 1
  expand = 3
  formula = Am
  name = G4_Am
  specific = 4
FEATURE [App::DocumentObjectGroupPython] Cm_element001  label="Cm_element : 1"  # scripted group (container) (typed FeaturePython)
  n = 1
  ref = Cm_element
FEATURE [App::DocumentObjectGroupPython] G4_Cm  # scripted group (container) (typed FeaturePython)
  Dunit = g/cm3
  Dvalue = 13.51
  Group = -> [Cm_element001]
  conduct = 2
  density = 1
  expand = 3
  formula = Cm
  name = G4_Cm
  specific = 4
FEATURE [App::DocumentObjectGroupPython] Bk_element001  label="Bk_element : 1"  # scripted group (container) (typed FeaturePython)
  n = 1
  ref = Bk_element
FEATURE [App::DocumentObjectGroupPython] G4_Bk  # scripted group (container) (typed FeaturePython)
  Dunit = g/cm3
  Dvalue = 14
  Group = -> [Bk_element001]
  conduct = 2
  density = 1
  expand = 3
  formula = Bk
  name = G4_Bk
  specific = 4
FEATURE [App::DocumentObjectGroupPython] Cf_element001  label="Cf_element : 1"  # scripted group (container) (typed FeaturePython)
  n = 1
  ref = Cf_element
FEATURE [App::DocumentObjectGroupPython] G4_Cf  # scripted group (container) (typed FeaturePython)
  Dunit = g/cm3
  Dvalue = 10
  Group = -> [Cf_element001]
  conduct = 2
  density = 1
  expand = 3
  formula = Cf
  name = G4_Cf
  specific = 4
FEATURE [App::DocumentObjectGroupPython] Element  # scripted group (container) (typed FeaturePython)
  Group = -> [G4_H,G4_He,G4_Li,G4_Be,G4_B,G4_C,G4_N,G4_O,G4_F,G4_Ne,G4_Na,G4_Mg,G4_Al,G4_Si,G4_P,G4_S,G4_Cl,G4_Ar,G4_K,G4_Ca,G4_Sc,G4_Ti,G4_V,G4_Cr,G4_Mn,G4_Fe,G4_Co,G4_Ni,G4_Cu,G4_Zn,G4_Ga,G4_Ge,G4_As,G4_Se,G4_Br,G4_Kr,G4_Rb,G4_Sr,G4_Y,G4_Zr,G4_Nb,G4_Mo,G4_Tc,G4_Ru,G4_Rh,G4_Pd,G4_Ag,G4_Cd,G4_In,G4_Sn,G4_Sb,G4_Te,G4_I,G4_Xe,G4_Cs,G4_Ba,G4_La,G4_Ce,G4_Pr,G4_Nd,G4_Pm,G4_Sm,G4_Eu,G4_Gd,G4_Tb,G4_Dy,G4_Ho,G4_Er,+30 more]
FEATURE [App::DocumentObjectGroupPython] H_element114  label="H_element : 063"  # scripted group (container) (typed FeaturePython)
  n = 2
  ref = H_element
FEATURE [App::DocumentObjectGroupPython] G4_lH2  # scripted group (container) (typed FeaturePython)
  Dunit = g/cm3
  Dvalue = 0.0708
  Group = -> [H_element114]
  conduct = 2
  density = 1
  expand = 3
  formula = G4_lH2
  name = G4_lH2
  specific = 4
FEATURE [App::DocumentObjectGroupPython] N_element049  label="N_element : 022"  # scripted group (container) (typed FeaturePython)
  n = 2
  ref = N_element
FEATURE [App::DocumentObjectGroupPython] G4_lN2  # scripted group (container) (typed FeaturePython)
  Dunit = g/cm3
  Dvalue = 0.807
  Group = -> [N_element049]
  conduct = 2
  density = 1
  expand = 3
  formula = G4_lN2
  name = G4_lN2
  specific = 4
FEATURE [App::DocumentObjectGroupPython] O_element106  label="O_element : 060"  # scripted group (container) (typed FeaturePython)
  n = 2
  ref = O_element
FEATURE [App::DocumentObjectGroupPython] G4_lO2  # scripted group (container) (typed FeaturePython)
  Dunit = g/cm3
  Dvalue = 1.141
  Group = -> [O_element106]
  conduct = 2
  density = 1
  expand = 3
  formula = G4_lO2
  name = G4_lO2
  specific = 4
FEATURE [App::DocumentObjectGroupPython] Ar  label="Ar : 1"  # scripted group (container) (typed FeaturePython)
  n = 1
  ref = Ar
FEATURE [App::DocumentObjectGroupPython] G4_lAr  # scripted group (container) (typed FeaturePython)
  Dunit = g/cm3
  Dvalue = 1.396
  Group = -> [Ar]
  conduct = 2
  density = 1
  expand = 3
  formula = G4_lAr
  name = G4_lAr
  specific = 4
FEATURE [App::DocumentObjectGroupPython] Br  label="Br : 1"  # scripted group (container) (typed FeaturePython)
  n = 1
  ref = Br
FEATURE [App::DocumentObjectGroupPython] G4_lBr  # scripted group (container) (typed FeaturePython)
  Dunit = g/cm3
  Dvalue = 3.1028
  Group = -> [Br]
  conduct = 2
  density = 1
  expand = 3
  formula = G4_lBr
  name = G4_lBr
  specific = 4
FEATURE [App::DocumentObjectGroupPython] Kr  label="Kr : 1"  # scripted group (container) (typed FeaturePython)
  n = 1
  ref = Kr
FEATURE [App::DocumentObjectGroupPython] G4_lKr  # scripted group (container) (typed FeaturePython)
  Dunit = g/cm3
  Dvalue = 2.418
  Group = -> [Kr]
  conduct = 2
  density = 1
  expand = 3
  formula = G4_lKr
  name = G4_lKr
  specific = 4
FEATURE [App::DocumentObjectGroupPython] Xe  label="Xe : 1"  # scripted group (container) (typed FeaturePython)
  n = 1
  ref = Xe
FEATURE [App::DocumentObjectGroupPython] G4_lXe  # scripted group (container) (typed FeaturePython)
  Dunit = g/cm3
  Dvalue = 2.953
  Group = -> [Xe]
  conduct = 2
  density = 1
  expand = 3
  formula = G4_lXe
  name = G4_lXe
  specific = 4
FEATURE [App::DocumentObjectGroupPython] O_element107  label="O_element : 061"  # scripted group (container) (typed FeaturePython)
  n = 4
  ref = O_element
FEATURE [App::DocumentObjectGroupPython] Pb_element004  label="Pb_element : 002"  # scripted group (container) (typed FeaturePython)
  n = 1
  ref = Pb_element
FEATURE [App::DocumentObjectGroupPython] W_element005  label="W_element : 005"  # scripted group (container) (typed FeaturePython)
  n = 1
  ref = W_element
FEATURE [App::DocumentObjectGroupPython] G4_PbWO4  # scripted group (container) (typed FeaturePython)
  Dunit = g/cm3
  Dvalue = 8.28
  Group = -> [O_element107,Pb_element004,W_element005]
  conduct = 2
  density = 1
  expand = 3
  formula = G4_PbWO4
  name = G4_PbWO4
  specific = 4
FEATURE [App::DocumentObjectGroupPython] alactic  label="alactic : 1"  # scripted group (container) (typed FeaturePython)
  n = 1
  ref = alactic
FEATURE [App::DocumentObjectGroupPython] G4_Galactic  # scripted group (container) (typed FeaturePython)
  Dunit = g/cm3
  Dvalue = 0
  Group = -> [alactic]
  conduct = 2
  density = 1
  expand = 3
  formula = G4_Galactic
  name = G4_Galactic
  specific = 4
FEATURE [App::DocumentObjectGroupPython] RAPHITE_POROUS  label="RAPHITE_POROUS : 1"  # scripted group (container) (typed FeaturePython)
  n = 1
  ref = RAPHITE_POROUS
FEATURE [App::DocumentObjectGroupPython] G4_GRAPHITE_POROUS  # scripted group (container) (typed FeaturePython)
  Dunit = g/cm3
  Dvalue = 1.7
  Group = -> [RAPHITE_POROUS]
  conduct = 2
  density = 1
  expand = 3
  formula = G4_GRAPHITE_POROUS
  name = G4_GRAPHITE_POROUS
  specific = 4
FEATURE [App::DocumentObjectGroupPython] H_element115  label="H_element : 0.150"  # scripted group (container) (typed FeaturePython)
  n = 0.080538
FEATURE [App::DocumentObjectGroupPython] C_element125  label="C_element : 0.600"  # scripted group (container) (typed FeaturePython)
  n = 0.599848
FEATURE [App::DocumentObjectGroupPython] O_element108  label="O_element : 0.320"  # scripted group (container) (typed FeaturePython)
  n = 0.319614
FEATURE [App::DocumentObjectGroupPython] G4_LUCITE  # scripted group (container) (typed FeaturePython)
  Dunit = g/cm3
  Dvalue = 1.19
  Group = -> [H_element115,C_element125,O_element108]
  conduct = 2
  density = 1
  expand = 3
  formula = G4_LUCITE
  name = G4_LUCITE
  specific = 4
FEATURE [App::DocumentObjectGroupPython] Cu_element002  label="Cu_element : 62"  # scripted group (container) (typed FeaturePython)
  n = 62
  ref = Cu_element
FEATURE [App::DocumentObjectGroupPython] Zn_element002  label="Zn_element : 35"  # scripted group (container) (typed FeaturePython)
  n = 35
  ref = Zn_element
FEATURE [App::DocumentObjectGroupPython] Pb_element005  label="Pb_element : 3"  # scripted group (container) (typed FeaturePython)
  n = 3
  ref = Pb_element
FEATURE [App::DocumentObjectGroupPython] G4_BRASS  # scripted group (container) (typed FeaturePython)
  Dunit = g/cm3
  Dvalue = 8.52
  Group = -> [Cu_element002,Zn_element002,Pb_element005]
  conduct = 2
  density = 1
  expand = 3
  formula = G4_BRASS
  name = G4_BRASS
  specific = 4
FEATURE [App::DocumentObjectGroupPython] Cu_element003  label="Cu_element : 89"  # scripted group (container) (typed FeaturePython)
  n = 89
  ref = Cu_element
FEATURE [App::DocumentObjectGroupPython] Zn_element003  label="Zn_element : 9"  # scripted group (container) (typed FeaturePython)
  n = 9
  ref = Zn_element
FEATURE [App::DocumentObjectGroupPython] Pb_element006  label="Pb_element : 2"  # scripted group (container) (typed FeaturePython)
  n = 2
  ref = Pb_element
FEATURE [App::DocumentObjectGroupPython] G4_BRONZE  # scripted group (container) (typed FeaturePython)
  Dunit = g/cm3
  Dvalue = 8.82
  Group = -> [Cu_element003,Zn_element003,Pb_element006]
  conduct = 2
  density = 1
  expand = 3
  formula = G4_BRONZE
  name = G4_BRONZE
  specific = 4
FEATURE [App::DocumentObjectGroupPython] Fe_element008  label="Fe_element : 74"  # scripted group (container) (typed FeaturePython)
  n = 74
  ref = Fe_element
FEATURE [App::DocumentObjectGroupPython] Cr_element002  label="Cr_element : 18"  # scripted group (container) (typed FeaturePython)
  n = 18
  ref = Cr_element
FEATURE [App::DocumentObjectGroupPython] Ni_element002  label="Ni_element : 8"  # scripted group (container) (typed FeaturePython)
  n = 8
  ref = Ni_element
FEATURE [App::DocumentObjectGroupPython] G4_STAINLESS_STEEL  label="G4_STAINLESS-STEEL"  # scripted group (container) (typed FeaturePython)
  Dunit = g/cm3
  Dvalue = 8
  Group = -> [Fe_element008,Cr_element002,Ni_element002]
  conduct = 2
  density = 1
  expand = 3
  formula = G4_STAINLESS-STEEL
  name = G4_STAINLESS-STEEL
  specific = 4
FEATURE [App::DocumentObjectGroupPython] H_element116  label="H_element : 064"  # scripted group (container) (typed FeaturePython)
  n = 18
  ref = H_element
FEATURE [App::DocumentObjectGroupPython] C_element126  label="C_element : 071"  # scripted group (container) (typed FeaturePython)
  n = 12
  ref = C_element
FEATURE [App::DocumentObjectGroupPython] O_element109  label="O_element : 062"  # scripted group (container) (typed FeaturePython)
  n = 7
  ref = O_element
FEATURE [App::DocumentObjectGroupPython] G4_CR39  # scripted group (container) (typed FeaturePython)
  Dunit = g/cm3
  Dvalue = 1.32
  Group = -> [H_element116,C_element126,O_element109]
  conduct = 2
  density = 1
  expand = 3
  formula = G4_CR39
  name = G4_CR39
  specific = 4
FEATURE [App::DocumentObjectGroupPython] H_element117  label="H_element : 38"  # scripted group (container) (typed FeaturePython)
  n = 38
  ref = H_element
FEATURE [App::DocumentObjectGroupPython] C_element127  label="C_element : 072"  # scripted group (container) (typed FeaturePython)
  n = 18
  ref = C_element
FEATURE [App::DocumentObjectGroupPython] O_element110  label="O_element : 063"  # scripted group (container) (typed FeaturePython)
  n = 1
  ref = O_element
FEATURE [App::DocumentObjectGroupPython] G4_OCTADECANOL  # scripted group (container) (typed FeaturePython)
  Dunit = g/cm3
  Dvalue = 0.812
  Group = -> [H_element117,C_element127,O_element110]
  conduct = 2
  density = 1
  expand = 3
  formula = G4_OCTADECANOL
  name = G4_OCTADECANOL
  specific = 4
FEATURE [App::DocumentObjectGroupPython] HEP  # scripted group (container) (typed FeaturePython)
  Group = -> [G4_lH2,G4_lN2,G4_lO2,G4_lAr,G4_lBr,G4_lKr,G4_lXe,G4_PbWO4,G4_Galactic,G4_GRAPHITE_POROUS,G4_LUCITE,G4_BRASS,G4_BRONZE,G4_STAINLESS_STEEL,G4_CR39,G4_OCTADECANOL]
FEATURE [App::DocumentObjectGroupPython] C_element128  label="C_element : 073"  # scripted group (container) (typed FeaturePython)
  n = 14
  ref = C_element
FEATURE [App::DocumentObjectGroupPython] H_element118  label="H_element : 065"  # scripted group (container) (typed FeaturePython)
  n = 10
  ref = H_element
FEATURE [App::DocumentObjectGroupPython] O_element111  label="O_element : 064"  # scripted group (container) (typed FeaturePython)
  n = 2
  ref = O_element
FEATURE [App::DocumentObjectGroupPython] N_element050  label="N_element : 023"  # scripted group (container) (typed FeaturePython)
  n = 2
  ref = N_element
FEATURE [App::DocumentObjectGroupPython] G4_KEVLAR  # scripted group (container) (typed FeaturePython)
  Dunit = g/cm3
  Dvalue = 1.44
  Group = -> [C_element128,H_element118,O_element111,N_element050]
  conduct = 2
  density = 1
  expand = 3
  formula = G4_KEVLAR
  name = G4_KEVLAR
  specific = 4
FEATURE [App::DocumentObjectGroupPython] C_element129  label="C_element : 074"  # scripted group (container) (typed FeaturePython)
  n = 10
  ref = C_element
FEATURE [App::DocumentObjectGroupPython] H_element119  label="H_element : 066"  # scripted group (container) (typed FeaturePython)
  n = 8
  ref = H_element
FEATURE [App::DocumentObjectGroupPython] O_element112  label="O_element : 065"  # scripted group (container) (typed FeaturePython)
  n = 4
  ref = O_element
FEATURE [App::DocumentObjectGroupPython] G4_DACRON  # scripted group (container) (typed FeaturePython)
  Dunit = g/cm3
  Dvalue = 1.4
  Group = -> [C_element129,H_element119,O_element112]
  conduct = 2
  density = 1
  expand = 3
  formula = G4_DACRON
  name = G4_DACRON
  specific = 4
FEATURE [App::DocumentObjectGroupPython] C_element130  label="C_element : 075"  # scripted group (container) (typed FeaturePython)
  n = 4
  ref = C_element
FEATURE [App::DocumentObjectGroupPython] H_element120  label="H_element : 067"  # scripted group (container) (typed FeaturePython)
  n = 5
  ref = H_element
FEATURE [App::DocumentObjectGroupPython] Cl_element030  label="Cl_element : 016"  # scripted group (container) (typed FeaturePython)
  n = 1
  ref = Cl_element
FEATURE [App::DocumentObjectGroupPython] G4_NEOPRENE  # scripted group (container) (typed FeaturePython)
  Dunit = g/cm3
  Dvalue = 1.23
  Group = -> [C_element130,H_element120,Cl_element030]
  conduct = 2
  density = 1
  expand = 3
  formula = G4_NEOPRENE
  name = G4_NEOPRENE
  specific = 4
FEATURE [App::DocumentObjectGroupPython] Space  # scripted group (container) (typed FeaturePython)
  Group = -> [G4_KEVLAR,G4_DACRON,G4_NEOPRENE]
FEATURE [App::DocumentObjectGroupPython] H_element121  label="H_element : 068"  # scripted group (container) (typed FeaturePython)
  n = 5
  ref = H_element
FEATURE [App::DocumentObjectGroupPython] C_element131  label="C_element : 076"  # scripted group (container) (typed FeaturePython)
  n = 4
  ref = C_element
FEATURE [App::DocumentObjectGroupPython] N_element051  label="N_element : 3"  # scripted group (container) (typed FeaturePython)
  n = 3
  ref = N_element
FEATURE [App::DocumentObjectGroupPython] O_element113  label="O_element : 066"  # scripted group (container) (typed FeaturePython)
  n = 1
  ref = O_element
FEATURE [App::DocumentObjectGroupPython] G4_CYTOSINE  # scripted group (container) (typed FeaturePython)
  Dunit = g/cm3
  Dvalue = 1.55
  Group = -> [H_element121,C_element131,N_element051,O_element113]
  conduct = 2
  density = 1
  expand = 3
  formula = G4_CYTOSINE
  name = G4_CYTOSINE
  specific = 4
FEATURE [App::DocumentObjectGroupPython] H_element122  label="H_element : 069"  # scripted group (container) (typed FeaturePython)
  n = 6
  ref = H_element
FEATURE [App::DocumentObjectGroupPython] C_element132  label="C_element : 077"  # scripted group (container) (typed FeaturePython)
  n = 5
  ref = C_element
FEATURE [App::DocumentObjectGroupPython] N_element052  label="N_element : 024"  # scripted group (container) (typed FeaturePython)
  n = 2
  ref = N_element
FEATURE [App::DocumentObjectGroupPython] O_element114  label="O_element : 067"  # scripted group (container) (typed FeaturePython)
  n = 2
  ref = O_element
FEATURE [App::DocumentObjectGroupPython] G4_THYMINE  # scripted group (container) (typed FeaturePython)
  Dunit = g/cm3
  Dvalue = 1.23
  Group = -> [H_element122,C_element132,N_element052,O_element114]
  conduct = 2
  density = 1
  expand = 3
  formula = G4_THYMINE
  name = G4_THYMINE
  specific = 4
FEATURE [App::DocumentObjectGroupPython] H_element123  label="H_element : 070"  # scripted group (container) (typed FeaturePython)
  n = 4
  ref = H_element
FEATURE [App::DocumentObjectGroupPython] C_element133  label="C_element : 078"  # scripted group (container) (typed FeaturePython)
  n = 4
  ref = C_element
FEATURE [App::DocumentObjectGroupPython] N_element053  label="N_element : 025"  # scripted group (container) (typed FeaturePython)
  n = 2
  ref = N_element
FEATURE [App::DocumentObjectGroupPython] O_element115  label="O_element : 068"  # scripted group (container) (typed FeaturePython)
  n = 2
  ref = O_element
FEATURE [App::DocumentObjectGroupPython] G4_URACIL  # scripted group (container) (typed FeaturePython)
  Dunit = g/cm3
  Dvalue = 1.32
  Group = -> [H_element123,C_element133,N_element053,O_element115]
  conduct = 2
  density = 1
  expand = 3
  formula = G4_URACIL
  name = G4_URACIL
  specific = 4
FEATURE [App::DocumentObjectGroupPython] H_element124  label="H_element : 071"  # scripted group (container) (typed FeaturePython)
  n = 4
  ref = H_element
FEATURE [App::DocumentObjectGroupPython] C_element134  label="C_element : 079"  # scripted group (container) (typed FeaturePython)
  n = 5
  ref = C_element
FEATURE [App::DocumentObjectGroupPython] N_element054  label="N_element : 026"  # scripted group (container) (typed FeaturePython)
  n = 5
  ref = N_element
FEATURE [App::DocumentObjectGroupPython] G4_DNA_ADENINE  # scripted group (container) (typed FeaturePython)
  Dunit = g/cm3
  Dvalue = 1
  Group = -> [H_element124,C_element134,N_element054]
  conduct = 2
  density = 1
  expand = 3
  formula = G4_DNA_ADENINE
  name = G4_DNA_ADENINE
  specific = 4
FEATURE [App::DocumentObjectGroupPython] H_element125  label="H_element : 072"  # scripted group (container) (typed FeaturePython)
  n = 4
  ref = H_element
FEATURE [App::DocumentObjectGroupPython] C_element135  label="C_element : 080"  # scripted group (container) (typed FeaturePython)
  n = 5
  ref = C_element
FEATURE [App::DocumentObjectGroupPython] N_element055  label="N_element : 027"  # scripted group (container) (typed FeaturePython)
  n = 5
  ref = N_element
FEATURE [App::DocumentObjectGroupPython] O_element116  label="O_element : 069"  # scripted group (container) (typed FeaturePython)
  n = 1
  ref = O_element
FEATURE [App::DocumentObjectGroupPython] G4_DNA_GUANINE  # scripted group (container) (typed FeaturePython)
  Dunit = g/cm3
  Dvalue = 1
  Group = -> [H_element125,C_element135,N_element055,O_element116]
  conduct = 2
  density = 1
  expand = 3
  formula = G4_DNA_GUANINE
  name = G4_DNA_GUANINE
  specific = 4
FEATURE [App::DocumentObjectGroupPython] H_element126  label="H_element : 073"  # scripted group (container) (typed FeaturePython)
  n = 4
  ref = H_element
FEATURE [App::DocumentObjectGroupPython] C_element136  label="C_element : 081"  # scripted group (container) (typed FeaturePython)
  n = 4
  ref = C_element
FEATURE [App::DocumentObjectGroupPython] N_element056  label="N_element : 028"  # scripted group (container) (typed FeaturePython)
  n = 3
  ref = N_element
FEATURE [App::DocumentObjectGroupPython] O_element117  label="O_element : 070"  # scripted group (container) (typed FeaturePython)
  n = 1
  ref = O_element
FEATURE [App::DocumentObjectGroupPython] G4_DNA_CYTOSINE  # scripted group (container) (typed FeaturePython)
  Dunit = g/cm3
  Dvalue = 1
  Group = -> [H_element126,C_element136,N_element056,O_element117]
  conduct = 2
  density = 1
  expand = 3
  formula = G4_DNA_CYTOSINE
  name = G4_DNA_CYTOSINE
  specific = 4
FEATURE [App::DocumentObjectGroupPython] H_element127  label="H_element : 074"  # scripted group (container) (typed FeaturePython)
  n = 5
  ref = H_element
FEATURE [App::DocumentObjectGroupPython] C_element137  label="C_element : 082"  # scripted group (container) (typed FeaturePython)
  n = 5
  ref = C_element
FEATURE [App::DocumentObjectGroupPython] N_element057  label="N_element : 029"  # scripted group (container) (typed FeaturePython)
  n = 2
  ref = N_element
FEATURE [App::DocumentObjectGroupPython] O_element118  label="O_element : 071"  # scripted group (container) (typed FeaturePython)
  n = 2
  ref = O_element
FEATURE [App::DocumentObjectGroupPython] G4_DNA_THYMINE  # scripted group (container) (typed FeaturePython)
  Dunit = g/cm3
  Dvalue = 1
  Group = -> [H_element127,C_element137,N_element057,O_element118]
  conduct = 2
  density = 1
  expand = 3
  formula = G4_DNA_THYMINE
  name = G4_DNA_THYMINE
  specific = 4
FEATURE [App::DocumentObjectGroupPython] H_element128  label="H_element : 075"  # scripted group (container) (typed FeaturePython)
  n = 3
  ref = H_element
FEATURE [App::DocumentObjectGroupPython] C_element138  label="C_element : 083"  # scripted group (container) (typed FeaturePython)
  n = 4
  ref = C_element
FEATURE [App::DocumentObjectGroupPython] N_element058  label="N_element : 030"  # scripted group (container) (typed FeaturePython)
  n = 2
  ref = N_element
FEATURE [App::DocumentObjectGroupPython] O_element119  label="O_element : 072"  # scripted group (container) (typed FeaturePython)
  n = 2
  ref = O_element
FEATURE [App::DocumentObjectGroupPython] G4_DNA_URACIL  # scripted group (container) (typed FeaturePython)
  Dunit = g/cm3
  Dvalue = 1
  Group = -> [H_element128,C_element138,N_element058,O_element119]
  conduct = 2
  density = 1
  expand = 3
  formula = G4_DNA_URACIL
  name = G4_DNA_URACIL
  specific = 4
FEATURE [App::DocumentObjectGroupPython] H_element129  label="H_element : 076"  # scripted group (container) (typed FeaturePython)
  n = 10
  ref = H_element
FEATURE [App::DocumentObjectGroupPython] C_element139  label="C_element : 084"  # scripted group (container) (typed FeaturePython)
  n = 10
  ref = C_element
FEATURE [App::DocumentObjectGroupPython] N_element059  label="N_element : 031"  # scripted group (container) (typed FeaturePython)
  n = 5
  ref = N_element
FEATURE [App::DocumentObjectGroupPython] O_element120  label="O_element : 073"  # scripted group (container) (typed FeaturePython)
  n = 4
  ref = O_element
FEATURE [App::DocumentObjectGroupPython] G4_DNA_ADENOSINE  # scripted group (container) (typed FeaturePython)
  Dunit = g/cm3
  Dvalue = 1
  Group = -> [H_element129,C_element139,N_element059,O_element120]
  conduct = 2
  density = 1
  expand = 3
  formula = G4_DNA_ADENOSINE
  name = G4_DNA_ADENOSINE
  specific = 4
FEATURE [App::DocumentObjectGroupPython] H_element130  label="H_element : 077"  # scripted group (container) (typed FeaturePython)
  n = 10
  ref = H_element
FEATURE [App::DocumentObjectGroupPython] C_element140  label="C_element : 085"  # scripted group (container) (typed FeaturePython)
  n = 10
  ref = C_element
FEATURE [App::DocumentObjectGroupPython] N_element060  label="N_element : 032"  # scripted group (container) (typed FeaturePython)
  n = 5
  ref = N_element
FEATURE [App::DocumentObjectGroupPython] O_element121  label="O_element : 074"  # scripted group (container) (typed FeaturePython)
  n = 5
  ref = O_element
FEATURE [App::DocumentObjectGroupPython] G4_DNA_GUANOSINE  # scripted group (container) (typed FeaturePython)
  Dunit = g/cm3
  Dvalue = 1
  Group = -> [H_element130,C_element140,N_element060,O_element121]
  conduct = 2
  density = 1
  expand = 3
  formula = G4_DNA_GUANOSINE
  name = G4_DNA_GUANOSINE
  specific = 4
FEATURE [App::DocumentObjectGroupPython] H_element131  label="H_element : 078"  # scripted group (container) (typed FeaturePython)
  n = 10
  ref = H_element
FEATURE [App::DocumentObjectGroupPython] C_element141  label="C_element : 086"  # scripted group (container) (typed FeaturePython)
  n = 9
  ref = C_element
FEATURE [App::DocumentObjectGroupPython] N_element061  label="N_element : 033"  # scripted group (container) (typed FeaturePython)
  n = 3
  ref = N_element
FEATURE [App::DocumentObjectGroupPython] O_element122  label="O_element : 075"  # scripted group (container) (typed FeaturePython)
  n = 5
  ref = O_element
FEATURE [App::DocumentObjectGroupPython] G4_DNA_CYTIDINE  # scripted group (container) (typed FeaturePython)
  Dunit = g/cm3
  Dvalue = 1
  Group = -> [H_element131,C_element141,N_element061,O_element122]
  conduct = 2
  density = 1
  expand = 3
  formula = G4_DNA_CYTIDINE
  name = G4_DNA_CYTIDINE
  specific = 4
FEATURE [App::DocumentObjectGroupPython] H_element132  label="H_element : 079"  # scripted group (container) (typed FeaturePython)
  n = 9
  ref = H_element
FEATURE [App::DocumentObjectGroupPython] C_element142  label="C_element : 087"  # scripted group (container) (typed FeaturePython)
  n = 9
  ref = C_element
FEATURE [App::DocumentObjectGroupPython] N_element062  label="N_element : 034"  # scripted group (container) (typed FeaturePython)
  n = 2
  ref = N_element
FEATURE [App::DocumentObjectGroupPython] O_element123  label="O_element : 076"  # scripted group (container) (typed FeaturePython)
  n = 6
  ref = O_element
FEATURE [App::DocumentObjectGroupPython] G4_DNA_URIDINE  # scripted group (container) (typed FeaturePython)
  Dunit = g/cm3
  Dvalue = 1
  Group = -> [H_element132,C_element142,N_element062,O_element123]
  conduct = 2
  density = 1
  expand = 3
  formula = G4_DNA_URIDINE
  name = G4_DNA_URIDINE
  specific = 4
FEATURE [App::DocumentObjectGroupPython] H_element133  label="H_element : 080"  # scripted group (container) (typed FeaturePython)
  n = 11
  ref = H_element
FEATURE [App::DocumentObjectGroupPython] C_element143  label="C_element : 088"  # scripted group (container) (typed FeaturePython)
  n = 10
  ref = C_element
FEATURE [App::DocumentObjectGroupPython] N_element063  label="N_element : 035"  # scripted group (container) (typed FeaturePython)
  n = 2
  ref = N_element
FEATURE [App::DocumentObjectGroupPython] O_element124  label="O_element : 077"  # scripted group (container) (typed FeaturePython)
  n = 6
  ref = O_element
FEATURE [App::DocumentObjectGroupPython] G4_DNA_METHYLURIDINE  # scripted group (container) (typed FeaturePython)
  Dunit = g/cm3
  Dvalue = 1
  Group = -> [H_element133,C_element143,N_element063,O_element124]
  conduct = 2
  density = 1
  expand = 3
  formula = G4_DNA_METHYLURIDINE
  name = G4_DNA_METHYLURIDINE
  specific = 4
FEATURE [App::DocumentObjectGroupPython] P_element014  label="P_element : 003"  # scripted group (container) (typed FeaturePython)
  n = 1
  ref = P_element
FEATURE [App::DocumentObjectGroupPython] O_element125  label="O_element : 078"  # scripted group (container) (typed FeaturePython)
  n = 3
  ref = O_element
FEATURE [App::DocumentObjectGroupPython] G4_DNA_MONOPHOSPHATE  # scripted group (container) (typed FeaturePython)
  Dunit = g/cm3
  Dvalue = 1
  Group = -> [P_element014,O_element125]
  conduct = 2
  density = 1
  expand = 3
  formula = G4_DNA_MONOPHOSPHATE
  name = G4_DNA_MONOPHOSPHATE
  specific = 4
FEATURE [App::DocumentObjectGroupPython] H_element134  label="H_element : 081"  # scripted group (container) (typed FeaturePython)
  n = 10
  ref = H_element
FEATURE [App::DocumentObjectGroupPython] C_element144  label="C_element : 089"  # scripted group (container) (typed FeaturePython)
  n = 10
  ref = C_element
FEATURE [App::DocumentObjectGroupPython] N_element064  label="N_element : 036"  # scripted group (container) (typed FeaturePython)
  n = 5
  ref = N_element
FEATURE [App::DocumentObjectGroupPython] O_element126  label="O_element : 079"  # scripted group (container) (typed FeaturePython)
  n = 7
  ref = O_element
FEATURE [App::DocumentObjectGroupPython] P_element015  label="P_element : 004"  # scripted group (container) (typed FeaturePython)
  n = 1
  ref = P_element
FEATURE [App::DocumentObjectGroupPython] G4_DNA_A  # scripted group (container) (typed FeaturePython)
  Dunit = g/cm3
  Dvalue = 1
  Group = -> [H_element134,C_element144,N_element064,O_element126,P_element015]
  conduct = 2
  density = 1
  expand = 3
  formula = G4_DNA_A
  name = G4_DNA_A
  specific = 4
FEATURE [App::DocumentObjectGroupPython] H_element135  label="H_element : 082"  # scripted group (container) (typed FeaturePython)
  n = 10
  ref = H_element
FEATURE [App::DocumentObjectGroupPython] C_element145  label="C_element : 090"  # scripted group (container) (typed FeaturePython)
  n = 10
  ref = C_element
FEATURE [App::DocumentObjectGroupPython] N_element065  label="N_element : 037"  # scripted group (container) (typed FeaturePython)
  n = 5
  ref = N_element
FEATURE [App::DocumentObjectGroupPython] O_element127  label="O_element : 8"  # scripted group (container) (typed FeaturePython)
  n = 8
  ref = O_element
FEATURE [App::DocumentObjectGroupPython] P_element016  label="P_element : 005"  # scripted group (container) (typed FeaturePython)
  n = 1
  ref = P_element
FEATURE [App::DocumentObjectGroupPython] G4_DNA_G  # scripted group (container) (typed FeaturePython)
  Dunit = g/cm3
  Dvalue = 1
  Group = -> [H_element135,C_element145,N_element065,O_element127,P_element016]
  conduct = 2
  density = 1
  expand = 3
  formula = G4_DNA_G
  name = G4_DNA_G
  specific = 4
FEATURE [App::DocumentObjectGroupPython] H_element136  label="H_element : 083"  # scripted group (container) (typed FeaturePython)
  n = 10
  ref = H_element
FEATURE [App::DocumentObjectGroupPython] C_element146  label="C_element : 091"  # scripted group (container) (typed FeaturePython)
  n = 9
  ref = C_element
FEATURE [App::DocumentObjectGroupPython] N_element066  label="N_element : 038"  # scripted group (container) (typed FeaturePython)
  n = 3
  ref = N_element
FEATURE [App::DocumentObjectGroupPython] O_element128  label="O_element : 080"  # scripted group (container) (typed FeaturePython)
  n = 8
  ref = O_element
FEATURE [App::DocumentObjectGroupPython] P_element017  label="P_element : 006"  # scripted group (container) (typed FeaturePython)
  n = 1
  ref = P_element
FEATURE [App::DocumentObjectGroupPython] G4_DNA_C  # scripted group (container) (typed FeaturePython)
  Dunit = g/cm3
  Dvalue = 1
  Group = -> [H_element136,C_element146,N_element066,O_element128,P_element017]
  conduct = 2
  density = 1
  expand = 3
  formula = G4_DNA_C
  name = G4_DNA_C
  specific = 4
FEATURE [App::DocumentObjectGroupPython] H_element137  label="H_element : 084"  # scripted group (container) (typed FeaturePython)
  n = 9
  ref = H_element
FEATURE [App::DocumentObjectGroupPython] C_element147  label="C_element : 092"  # scripted group (container) (typed FeaturePython)
  n = 9
  ref = C_element
FEATURE [App::DocumentObjectGroupPython] N_element067  label="N_element : 039"  # scripted group (container) (typed FeaturePython)
  n = 2
  ref = N_element
FEATURE [App::DocumentObjectGroupPython] O_element129  label="O_element : 9"  # scripted group (container) (typed FeaturePython)
  n = 9
  ref = O_element
FEATURE [App::DocumentObjectGroupPython] P_element018  label="P_element : 007"  # scripted group (container) (typed FeaturePython)
  n = 1
  ref = P_element
FEATURE [App::DocumentObjectGroupPython] G4_DNA_U  # scripted group (container) (typed FeaturePython)
  Dunit = g/cm3
  Dvalue = 1
  Group = -> [H_element137,C_element147,N_element067,O_element129,P_element018]
  conduct = 2
  density = 1
  expand = 3
  formula = G4_DNA_U
  name = G4_DNA_U
  specific = 4
FEATURE [App::DocumentObjectGroupPython] H_element138  label="H_element : 085"  # scripted group (container) (typed FeaturePython)
  n = 11
  ref = H_element
FEATURE [App::DocumentObjectGroupPython] C_element148  label="C_element : 093"  # scripted group (container) (typed FeaturePython)
  n = 10
  ref = C_element
FEATURE [App::DocumentObjectGroupPython] N_element068  label="N_element : 040"  # scripted group (container) (typed FeaturePython)
  n = 2
  ref = N_element
FEATURE [App::DocumentObjectGroupPython] O_element130  label="O_element : 081"  # scripted group (container) (typed FeaturePython)
  n = 9
  ref = O_element
FEATURE [App::DocumentObjectGroupPython] P_element019  label="P_element : 008"  # scripted group (container) (typed FeaturePython)
  n = 1
  ref = P_element
FEATURE [App::DocumentObjectGroupPython] G4_DNA_MU  # scripted group (container) (typed FeaturePython)
  Dunit = g/cm3
  Dvalue = 1
  Group = -> [H_element138,C_element148,N_element068,O_element130,P_element019]
  conduct = 2
  density = 1
  expand = 3
  formula = G4_DNA_MU
  name = G4_DNA_MU
  specific = 4
FEATURE [App::DocumentObjectGroupPython] BioChemical  # scripted group (container) (typed FeaturePython)
  Group = -> [G4_CYTOSINE,G4_THYMINE,G4_URACIL,G4_DNA_ADENINE,G4_DNA_GUANINE,G4_DNA_CYTOSINE,G4_DNA_THYMINE,G4_DNA_URACIL,G4_DNA_ADENOSINE,G4_DNA_GUANOSINE,G4_DNA_CYTIDINE,G4_DNA_URIDINE,G4_DNA_METHYLURIDINE,G4_DNA_MONOPHOSPHATE,G4_DNA_A,G4_DNA_G,G4_DNA_C,G4_DNA_U,G4_DNA_MU]
FEATURE [App::DocumentObjectGroupPython] G4Materials  # scripted group (container) (typed FeaturePython)
  Group = -> [NIST,Element,HEP,Space,BioChemical]
  version = 1
FEATURE [App::DocumentObjectGroupPython] Geant4  # scripted group (container) (typed FeaturePython)
  Group = -> [G4Isotopes,G4Elements,G4Materials]
FEATURE [App::DocumentObjectGroupPython] Materials  # scripted group (container) (typed FeaturePython)
  Group = -> [Geant4]
FEATURE [Part::FeaturePython] GDMLBox_WorldBox  # WARN: FeaturePython — macro-defined, semantics opaque (R4)
  lunit = 2
  material = 5
  x = 273
  y = 273
  z = 130
FEATURE [Part::FeaturePython] GDMLBox_Box  # WARN: FeaturePython — macro-defined, semantics opaque (R4)
  Placement = pos=(20,0,0) rot=(0,0,1;0rad)
  lunit = 2
  material = 0
  x = 10
  y = 10
  z = 10
FEATURE [Part::FeaturePython] GDMLTube  # WARN: FeaturePython — macro-defined, semantics opaque (R4)
  Placement = pos=(17,-4,0) rot=(0,0,1;0rad)
  aunit = 1
  deltaphi = 90
  lunit = 2
  material = 0
  rmax = 7
  rmin = 5
  startphi = 0
  z = 7
FEATURE [App::Part] LV_Tube
  Group = -> [GDMLTube]
  Origin = -> Origin003
  SkinSurface = 0
FEATURE [App::Part] LV_Box
  Group = -> [GDMLBox_Box,LV_Tube]
  Origin = -> Origin002
FEATURE [Part::FeaturePython] Array  # Draft array (typed FeaturePython)
  AlwaysSyncPlacement = false
  Angle = 180
  ArrayType = 1
  Axis = (0,0,1)
  Base = -> LV_Box
  Center = (0,0,0)
  Count = 5
  ExpandArray = false
  Fuse = false
  IntervalAxis = (0,0,0)
  IntervalX = (100,0,0)
  IntervalY = (0,100,0)
  IntervalZ = (0,0,100)
  NumberCircles = 3
  NumberPolar = 5
  NumberX = 2
  NumberY = 2
  NumberZ = 1
  PlacementList = 5 placements: [(0,0,0),(0,0,0),(0,0,0),(0,0,0),(0,0,0)]
  RadialDistance = 50
  ScaleList = (5) [(1,1,1),(1,1,1),(1,1,1),(1,1,1),(1,1,1)]
  Symmetry = 1
  TangentialDistance = 25
FEATURE [App::Part] Part  label="experiment"
  Group = -> [LV_Box,Array]
  Origin = -> Origin001
FEATURE [App::Part] worldVOL
  Group = -> [GDMLBox_WorldBox,Part]
  Origin = -> Origin
